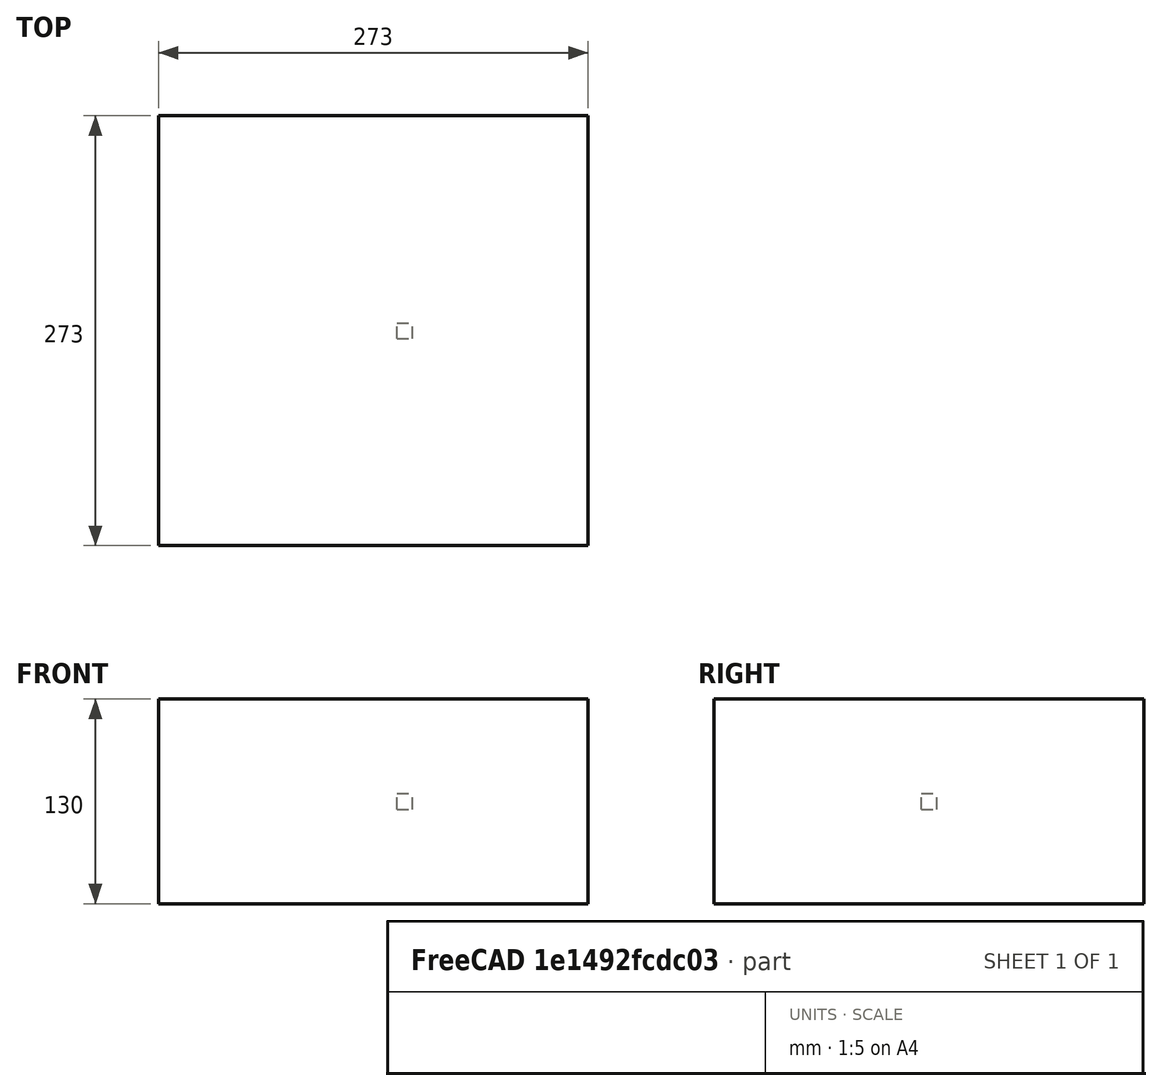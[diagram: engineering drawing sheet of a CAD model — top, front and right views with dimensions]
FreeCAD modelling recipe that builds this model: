
FCSTD DOCUMENT  (FreeCAD 0.20RUnknown)
Label: polarArray-4
License: All rights reserved
LicenseURL: http://en.wikipedia.org/wiki/All_rights_reserved
objects: App::DocumentObjectGroupPython×1251, Part::FeaturePython×3, App::Part×3
note: 2 computed .brp shape members not serialized (recipe doc carries the construction recipe); baked Part::Feature solids carry a one-line shape summary decoded from their .brp

FEATURE [App::DocumentObjectGroupPython] HALFPI  # scripted group (container) (typed FeaturePython)
  name = HALFPI
  value = pi/2.
FEATURE [App::DocumentObjectGroupPython] PI  # scripted group (container) (typed FeaturePython)
  name = PI
  value = 1.*pi
FEATURE [App::DocumentObjectGroupPython] TWOPI  # scripted group (container) (typed FeaturePython)
  name = TWOPI
  value = 2.*pi
FEATURE [App::DocumentObjectGroupPython] Constants  # scripted group (container) (typed FeaturePython)
  Group = -> [HALFPI,PI,TWOPI]
FEATURE [App::DocumentObjectGroupPython] Variables  # scripted group (container) (typed FeaturePython)
FEATURE [App::DocumentObjectGroupPython] Quantities  # scripted group (container) (typed FeaturePython)
FEATURE [App::DocumentObjectGroupPython] Isotopes  # scripted group (container) (typed FeaturePython)
FEATURE [App::DocumentObjectGroupPython] Elements  # scripted group (container) (typed FeaturePython)
FEATURE [App::DocumentObjectGroupPython] Matrix  # scripted group (container) (typed FeaturePython)
FEATURE [App::DocumentObjectGroupPython] Surfaces  # scripted group (container) (typed FeaturePython)
FEATURE [App::DocumentObjectGroupPython] Opticals  # scripted group (container) (typed FeaturePython)
  Group = -> [Matrix,Surfaces]
FEATURE [App::DocumentObjectGroupPython] G4Isotopes  # scripted group (container) (typed FeaturePython)
FEATURE [App::DocumentObjectGroupPython] H_element  # scripted group (container) (typed FeaturePython)
  Z = 1
  atom_value = 1.008
  formula = H
  name = H_element
FEATURE [App::DocumentObjectGroupPython] He_element  # scripted group (container) (typed FeaturePython)
  Z = 2
  atom_value = 4.0026
  formula = He
  name = He_element
FEATURE [App::DocumentObjectGroupPython] Li_element  # scripted group (container) (typed FeaturePython)
  Z = 3
  atom_value = 6.94
  formula = Li
  name = Li_element
FEATURE [App::DocumentObjectGroupPython] Be_element  # scripted group (container) (typed FeaturePython)
  Z = 4
  atom_value = 9.01218
  formula = Be
  name = Be_element
FEATURE [App::DocumentObjectGroupPython] B_element  # scripted group (container) (typed FeaturePython)
  Z = 5
  atom_value = 10.81
  formula = B
  name = B_element
FEATURE [App::DocumentObjectGroupPython] C_element  # scripted group (container) (typed FeaturePython)
  Z = 6
  atom_value = 12.011
  formula = C
  name = C_element
FEATURE [App::DocumentObjectGroupPython] N_element  # scripted group (container) (typed FeaturePython)
  Z = 7
  atom_value = 14.007
  formula = N
  name = N_element
FEATURE [App::DocumentObjectGroupPython] O_element  # scripted group (container) (typed FeaturePython)
  Z = 8
  atom_value = 15.999
  formula = O
  name = O_element
FEATURE [App::DocumentObjectGroupPython] F_element  # scripted group (container) (typed FeaturePython)
  Z = 9
  atom_value = 18.9984
  formula = F
  name = F_element
FEATURE [App::DocumentObjectGroupPython] Ne_element  # scripted group (container) (typed FeaturePython)
  Z = 10
  atom_value = 20.1797
  formula = Ne
  name = Ne_element
FEATURE [App::DocumentObjectGroupPython] Na_element  # scripted group (container) (typed FeaturePython)
  Z = 11
  atom_value = 22.9898
  formula = Na
  name = Na_element
FEATURE [App::DocumentObjectGroupPython] Mg_element  # scripted group (container) (typed FeaturePython)
  Z = 12
  atom_value = 24.305
  formula = Mg
  name = Mg_element
FEATURE [App::DocumentObjectGroupPython] Al_element  # scripted group (container) (typed FeaturePython)
  Z = 13
  atom_value = 26.9815
  formula = Al
  name = Al_element
FEATURE [App::DocumentObjectGroupPython] Si_element  # scripted group (container) (typed FeaturePython)
  Z = 14
  atom_value = 28.085
  formula = Si
  name = Si_element
FEATURE [App::DocumentObjectGroupPython] P_element  # scripted group (container) (typed FeaturePython)
  Z = 15
  atom_value = 30.9738
  formula = P
  name = P_element
FEATURE [App::DocumentObjectGroupPython] S_element  # scripted group (container) (typed FeaturePython)
  Z = 16
  atom_value = 32.06
  formula = S
  name = S_element
FEATURE [App::DocumentObjectGroupPython] Cl_element  # scripted group (container) (typed FeaturePython)
  Z = 17
  atom_value = 35.45
  formula = Cl
  name = Cl_element
FEATURE [App::DocumentObjectGroupPython] Ar_element  # scripted group (container) (typed FeaturePython)
  Z = 18
  atom_value = 39.95
  formula = Ar
  name = Ar_element
FEATURE [App::DocumentObjectGroupPython] K_element  # scripted group (container) (typed FeaturePython)
  Z = 19
  atom_value = 39.0983
  formula = K
  name = K_element
FEATURE [App::DocumentObjectGroupPython] Ca_element  # scripted group (container) (typed FeaturePython)
  Z = 20
  atom_value = 40.078
  formula = Ca
  name = Ca_element
FEATURE [App::DocumentObjectGroupPython] Sc_element  # scripted group (container) (typed FeaturePython)
  Z = 21
  atom_value = 44.9559
  formula = Sc
  name = Sc_element
FEATURE [App::DocumentObjectGroupPython] Ti_element  # scripted group (container) (typed FeaturePython)
  Z = 22
  atom_value = 47.867
  formula = Ti
  name = Ti_element
FEATURE [App::DocumentObjectGroupPython] V_element  # scripted group (container) (typed FeaturePython)
  Z = 23
  atom_value = 50.9415
  formula = V
  name = V_element
FEATURE [App::DocumentObjectGroupPython] Cr_element  # scripted group (container) (typed FeaturePython)
  Z = 24
  atom_value = 51.9961
  formula = Cr
  name = Cr_element
FEATURE [App::DocumentObjectGroupPython] Mn_element  # scripted group (container) (typed FeaturePython)
  Z = 25
  atom_value = 54.938
  formula = Mn
  name = Mn_element
FEATURE [App::DocumentObjectGroupPython] Fe_element  # scripted group (container) (typed FeaturePython)
  Z = 26
  atom_value = 55.845
  formula = Fe
  name = Fe_element
FEATURE [App::DocumentObjectGroupPython] Co_element  # scripted group (container) (typed FeaturePython)
  Z = 27
  atom_value = 58.9332
  formula = Co
  name = Co_element
FEATURE [App::DocumentObjectGroupPython] Ni_element  # scripted group (container) (typed FeaturePython)
  Z = 28
  atom_value = 58.6934
  formula = Ni
  name = Ni_element
FEATURE [App::DocumentObjectGroupPython] Cu_element  # scripted group (container) (typed FeaturePython)
  Z = 29
  atom_value = 63.546
  formula = Cu
  name = Cu_element
FEATURE [App::DocumentObjectGroupPython] Zn_element  # scripted group (container) (typed FeaturePython)
  Z = 30
  atom_value = 65.38
  formula = Zn
  name = Zn_element
FEATURE [App::DocumentObjectGroupPython] Ga_element  # scripted group (container) (typed FeaturePython)
  Z = 31
  atom_value = 69.723
  formula = Ga
  name = Ga_element
FEATURE [App::DocumentObjectGroupPython] Ge_element  # scripted group (container) (typed FeaturePython)
  Z = 32
  atom_value = 72.63
  formula = Ge
  name = Ge_element
FEATURE [App::DocumentObjectGroupPython] As_element  # scripted group (container) (typed FeaturePython)
  Z = 33
  atom_value = 74.9216
  formula = As
  name = As_element
FEATURE [App::DocumentObjectGroupPython] Se_element  # scripted group (container) (typed FeaturePython)
  Z = 34
  atom_value = 78.971
  formula = Se
  name = Se_element
FEATURE [App::DocumentObjectGroupPython] Br_element  # scripted group (container) (typed FeaturePython)
  Z = 35
  atom_value = 79.904
  formula = Br
  name = Br_element
FEATURE [App::DocumentObjectGroupPython] Kr_element  # scripted group (container) (typed FeaturePython)
  Z = 36
  atom_value = 83.798
  formula = Kr
  name = Kr_element
FEATURE [App::DocumentObjectGroupPython] Rb_element  # scripted group (container) (typed FeaturePython)
  Z = 37
  atom_value = 85.4678
  formula = Rb
  name = Rb_element
FEATURE [App::DocumentObjectGroupPython] Sr_element  # scripted group (container) (typed FeaturePython)
  Z = 38
  atom_value = 87.62
  formula = Sr
  name = Sr_element
FEATURE [App::DocumentObjectGroupPython] Y_element  # scripted group (container) (typed FeaturePython)
  Z = 39
  atom_value = 88.9058
  formula = Y
  name = Y_element
FEATURE [App::DocumentObjectGroupPython] Zr_element  # scripted group (container) (typed FeaturePython)
  Z = 40
  atom_value = 91.224
  formula = Zr
  name = Zr_element
FEATURE [App::DocumentObjectGroupPython] Nb_element  # scripted group (container) (typed FeaturePython)
  Z = 41
  atom_value = 92.9064
  formula = Nb
  name = Nb_element
FEATURE [App::DocumentObjectGroupPython] Mo_element  # scripted group (container) (typed FeaturePython)
  Z = 42
  atom_value = 95.95
  formula = Mo
  name = Mo_element
FEATURE [App::DocumentObjectGroupPython] Tc_element  # scripted group (container) (typed FeaturePython)
  Z = 43
  atom_value = 97
  formula = Tc
  name = Tc_element
FEATURE [App::DocumentObjectGroupPython] Ru_element  # scripted group (container) (typed FeaturePython)
  Z = 44
  atom_value = 101.07
  formula = Ru
  name = Ru_element
FEATURE [App::DocumentObjectGroupPython] Rh_element  # scripted group (container) (typed FeaturePython)
  Z = 45
  atom_value = 102.905
  formula = Rh
  name = Rh_element
FEATURE [App::DocumentObjectGroupPython] Pd_element  # scripted group (container) (typed FeaturePython)
  Z = 46
  atom_value = 106.42
  formula = Pd
  name = Pd_element
FEATURE [App::DocumentObjectGroupPython] Ag_element  # scripted group (container) (typed FeaturePython)
  Z = 47
  atom_value = 107.868
  formula = Ag
  name = Ag_element
FEATURE [App::DocumentObjectGroupPython] Cd_element  # scripted group (container) (typed FeaturePython)
  Z = 48
  atom_value = 112.414
  formula = Cd
  name = Cd_element
FEATURE [App::DocumentObjectGroupPython] In_element  # scripted group (container) (typed FeaturePython)
  Z = 49
  atom_value = 114.818
  formula = In
  name = In_element
FEATURE [App::DocumentObjectGroupPython] Sn_element  # scripted group (container) (typed FeaturePython)
  Z = 50
  atom_value = 118.71
  formula = Sn
  name = Sn_element
FEATURE [App::DocumentObjectGroupPython] Sb_element  # scripted group (container) (typed FeaturePython)
  Z = 51
  atom_value = 121.76
  formula = Sb
  name = Sb_element
FEATURE [App::DocumentObjectGroupPython] Te_element  # scripted group (container) (typed FeaturePython)
  Z = 52
  atom_value = 127.6
  formula = Te
  name = Te_element
FEATURE [App::DocumentObjectGroupPython] I_element  # scripted group (container) (typed FeaturePython)
  Z = 53
  atom_value = 126.904
  formula = I
  name = I_element
FEATURE [App::DocumentObjectGroupPython] Xe_element  # scripted group (container) (typed FeaturePython)
  Z = 54
  atom_value = 131.293
  formula = Xe
  name = Xe_element
FEATURE [App::DocumentObjectGroupPython] Cs_element  # scripted group (container) (typed FeaturePython)
  Z = 55
  atom_value = 132.905
  formula = Cs
  name = Cs_element
FEATURE [App::DocumentObjectGroupPython] Ba_element  # scripted group (container) (typed FeaturePython)
  Z = 56
  atom_value = 137.327
  formula = Ba
  name = Ba_element
FEATURE [App::DocumentObjectGroupPython] La_element  # scripted group (container) (typed FeaturePython)
  Z = 57
  atom_value = 138.905
  formula = La
  name = La_element
FEATURE [App::DocumentObjectGroupPython] Ce_element  # scripted group (container) (typed FeaturePython)
  Z = 58
  atom_value = 140.116
  formula = Ce
  name = Ce_element
FEATURE [App::DocumentObjectGroupPython] Pr_element  # scripted group (container) (typed FeaturePython)
  Z = 59
  atom_value = 140.908
  formula = Pr
  name = Pr_element
FEATURE [App::DocumentObjectGroupPython] Nd_element  # scripted group (container) (typed FeaturePython)
  Z = 60
  atom_value = 144.242
  formula = Nd
  name = Nd_element
FEATURE [App::DocumentObjectGroupPython] Pm_element  # scripted group (container) (typed FeaturePython)
  Z = 61
  atom_value = 145
  formula = Pm
  name = Pm_element
FEATURE [App::DocumentObjectGroupPython] Sm_element  # scripted group (container) (typed FeaturePython)
  Z = 62
  atom_value = 150.36
  formula = Sm
  name = Sm_element
FEATURE [App::DocumentObjectGroupPython] Eu_element  # scripted group (container) (typed FeaturePython)
  Z = 63
  atom_value = 151.964
  formula = Eu
  name = Eu_element
FEATURE [App::DocumentObjectGroupPython] Gd_element  # scripted group (container) (typed FeaturePython)
  Z = 64
  atom_value = 157.25
  formula = Gd
  name = Gd_element
FEATURE [App::DocumentObjectGroupPython] Tb_element  # scripted group (container) (typed FeaturePython)
  Z = 65
  atom_value = 158.925
  formula = Tb
  name = Tb_element
FEATURE [App::DocumentObjectGroupPython] Dy_element  # scripted group (container) (typed FeaturePython)
  Z = 66
  atom_value = 162.5
  formula = Dy
  name = Dy_element
FEATURE [App::DocumentObjectGroupPython] Ho_element  # scripted group (container) (typed FeaturePython)
  Z = 67
  atom_value = 164.93
  formula = Ho
  name = Ho_element
FEATURE [App::DocumentObjectGroupPython] Er_element  # scripted group (container) (typed FeaturePython)
  Z = 68
  atom_value = 167.259
  formula = Er
  name = Er_element
FEATURE [App::DocumentObjectGroupPython] Tm_element  # scripted group (container) (typed FeaturePython)
  Z = 69
  atom_value = 168.934
  formula = Tm
  name = Tm_element
FEATURE [App::DocumentObjectGroupPython] Yb_element  # scripted group (container) (typed FeaturePython)
  Z = 70
  atom_value = 173.045
  formula = Yb
  name = Yb_element
FEATURE [App::DocumentObjectGroupPython] Lu_element  # scripted group (container) (typed FeaturePython)
  Z = 71
  atom_value = 174.967
  formula = Lu
  name = Lu_element
FEATURE [App::DocumentObjectGroupPython] Hf_element  # scripted group (container) (typed FeaturePython)
  Z = 72
  atom_value = 178.49
  formula = Hf
  name = Hf_element
FEATURE [App::DocumentObjectGroupPython] Ta_element  # scripted group (container) (typed FeaturePython)
  Z = 73
  atom_value = 180.948
  formula = Ta
  name = Ta_element
FEATURE [App::DocumentObjectGroupPython] W_element  # scripted group (container) (typed FeaturePython)
  Z = 74
  atom_value = 183.84
  formula = W
  name = W_element
FEATURE [App::DocumentObjectGroupPython] Re_element  # scripted group (container) (typed FeaturePython)
  Z = 75
  atom_value = 186.207
  formula = Re
  name = Re_element
FEATURE [App::DocumentObjectGroupPython] Os_element  # scripted group (container) (typed FeaturePython)
  Z = 76
  atom_value = 190.23
  formula = Os
  name = Os_element
FEATURE [App::DocumentObjectGroupPython] Ir_element  # scripted group (container) (typed FeaturePython)
  Z = 77
  atom_value = 192.217
  formula = Ir
  name = Ir_element
FEATURE [App::DocumentObjectGroupPython] Pt_element  # scripted group (container) (typed FeaturePython)
  Z = 78
  atom_value = 195.084
  formula = Pt
  name = Pt_element
FEATURE [App::DocumentObjectGroupPython] Au_element  # scripted group (container) (typed FeaturePython)
  Z = 79
  atom_value = 196.967
  formula = Au
  name = Au_element
FEATURE [App::DocumentObjectGroupPython] Hg_element  # scripted group (container) (typed FeaturePython)
  Z = 80
  atom_value = 200.592
  formula = Hg
  name = Hg_element
FEATURE [App::DocumentObjectGroupPython] Tl_element  # scripted group (container) (typed FeaturePython)
  Z = 81
  atom_value = 204.38
  formula = Tl
  name = Tl_element
FEATURE [App::DocumentObjectGroupPython] Pb_element  # scripted group (container) (typed FeaturePython)
  Z = 82
  atom_value = 207.2
  formula = Pb
  name = Pb_element
FEATURE [App::DocumentObjectGroupPython] Bi_element  # scripted group (container) (typed FeaturePython)
  Z = 83
  atom_value = 208.98
  formula = Bi
  name = Bi_element
FEATURE [App::DocumentObjectGroupPython] Po_element  # scripted group (container) (typed FeaturePython)
  Z = 84
  atom_value = 209
  formula = Po
  name = Po_element
FEATURE [App::DocumentObjectGroupPython] At_element  # scripted group (container) (typed FeaturePython)
  Z = 85
  atom_value = 210
  formula = At
  name = At_element
FEATURE [App::DocumentObjectGroupPython] Rn_element  # scripted group (container) (typed FeaturePython)
  Z = 86
  atom_value = 222
  formula = Rn
  name = Rn_element
FEATURE [App::DocumentObjectGroupPython] Fr_element  # scripted group (container) (typed FeaturePython)
  Z = 87
  atom_value = 223
  formula = Fr
  name = Fr_element
FEATURE [App::DocumentObjectGroupPython] Ra_element  # scripted group (container) (typed FeaturePython)
  Z = 88
  atom_value = 226
  formula = Ra
  name = Ra_element
FEATURE [App::DocumentObjectGroupPython] Ac_element  # scripted group (container) (typed FeaturePython)
  Z = 89
  atom_value = 227
  formula = Ac
  name = Ac_element
FEATURE [App::DocumentObjectGroupPython] Th_element  # scripted group (container) (typed FeaturePython)
  Z = 90
  atom_value = 232.038
  formula = Th
  name = Th_element
FEATURE [App::DocumentObjectGroupPython] Pa_element  # scripted group (container) (typed FeaturePython)
  Z = 91
  atom_value = 231.036
  formula = Pa
  name = Pa_element
FEATURE [App::DocumentObjectGroupPython] U_element  # scripted group (container) (typed FeaturePython)
  Z = 92
  atom_value = 238.029
  formula = U
  name = U_element
FEATURE [App::DocumentObjectGroupPython] Np_element  # scripted group (container) (typed FeaturePython)
  Z = 93
  atom_value = 237
  formula = Np
  name = Np_element
FEATURE [App::DocumentObjectGroupPython] Pu_element  # scripted group (container) (typed FeaturePython)
  Z = 94
  atom_value = 244
  formula = Pu
  name = Pu_element
FEATURE [App::DocumentObjectGroupPython] Am_element  # scripted group (container) (typed FeaturePython)
  Z = 95
  atom_value = 243
  formula = Am
  name = Am_element
FEATURE [App::DocumentObjectGroupPython] Cm_element  # scripted group (container) (typed FeaturePython)
  Z = 96
  atom_value = 247
  formula = Cm
  name = Cm_element
FEATURE [App::DocumentObjectGroupPython] Bk_element  # scripted group (container) (typed FeaturePython)
  Z = 97
  atom_value = 247
  formula = Bk
  name = Bk_element
FEATURE [App::DocumentObjectGroupPython] Cf_element  # scripted group (container) (typed FeaturePython)
  Z = 98
  atom_value = 251
  formula = Cf
  name = Cf_element
FEATURE [App::DocumentObjectGroupPython] G4Elements  # scripted group (container) (typed FeaturePython)
  Group = -> [H_element,He_element,Li_element,Be_element,B_element,C_element,N_element,O_element,F_element,Ne_element,Na_element,Mg_element,Al_element,Si_element,P_element,S_element,Cl_element,Ar_element,K_element,Ca_element,Sc_element,Ti_element,V_element,Cr_element,Mn_element,Fe_element,Co_element,Ni_element,Cu_element,Zn_element,Ga_element,Ge_element,As_element,Se_element,Br_element,Kr_element,Rb_element,+61 more]
FEATURE [App::DocumentObjectGroupPython] H_element001  label="H_element : 0.101"  # scripted group (container) (typed FeaturePython)
  n = 0.101327
FEATURE [App::DocumentObjectGroupPython] C_element001  label="C_element : 0.775"  # scripted group (container) (typed FeaturePython)
  n = 0.7755
FEATURE [App::DocumentObjectGroupPython] N_element001  label="N_element : 0.035"  # scripted group (container) (typed FeaturePython)
  n = 0.035057
FEATURE [App::DocumentObjectGroupPython] O_element001  label="O_element : 0.052"  # scripted group (container) (typed FeaturePython)
  n = 0.0523159
FEATURE [App::DocumentObjectGroupPython] F_element001  label="F_element : 0.017"  # scripted group (container) (typed FeaturePython)
  n = 0.017422
FEATURE [App::DocumentObjectGroupPython] Ca_element001  label="Ca_element : 0.018"  # scripted group (container) (typed FeaturePython)
  n = 0.018378
FEATURE [App::DocumentObjectGroupPython] G4_A_150_TISSUE  label="G4_A-150_TISSUE"  # scripted group (container) (typed FeaturePython)
  Dunit = g/cm3
  Dvalue = 1.127
  Group = -> [H_element001,C_element001,N_element001,O_element001,F_element001,Ca_element001]
  conduct = 2
  density = 1
  expand = 3
  formula = G4_A-150_TISSUE
  name = G4_A-150_TISSUE
  specific = 4
FEATURE [App::DocumentObjectGroupPython] C_element002  label="C_element : 3"  # scripted group (container) (typed FeaturePython)
  n = 3
  ref = C_element
FEATURE [App::DocumentObjectGroupPython] H_element002  label="H_element : 6"  # scripted group (container) (typed FeaturePython)
  n = 6
  ref = H_element
FEATURE [App::DocumentObjectGroupPython] O_element002  label="O_element : 1"  # scripted group (container) (typed FeaturePython)
  n = 1
  ref = O_element
FEATURE [App::DocumentObjectGroupPython] G4_ACETONE  # scripted group (container) (typed FeaturePython)
  Dunit = g/cm3
  Dvalue = 0.7899
  Group = -> [C_element002,H_element002,O_element002]
  conduct = 2
  density = 1
  expand = 3
  formula = G4_ACETONE
  name = G4_ACETONE
  specific = 4
FEATURE [App::DocumentObjectGroupPython] C_element003  label="C_element : 2"  # scripted group (container) (typed FeaturePython)
  n = 2
  ref = C_element
FEATURE [App::DocumentObjectGroupPython] H_element003  label="H_element : 2"  # scripted group (container) (typed FeaturePython)
  n = 2
  ref = H_element
FEATURE [App::DocumentObjectGroupPython] G4_ACETYLENE  # scripted group (container) (typed FeaturePython)
  Dunit = g/cm3
  Dvalue = 0.0010967
  Group = -> [C_element003,H_element003]
  conduct = 2
  density = 1
  expand = 3
  formula = G4_ACETYLENE
  name = G4_ACETYLENE
  specific = 4
FEATURE [App::DocumentObjectGroupPython] C_element004  label="C_element : 5"  # scripted group (container) (typed FeaturePython)
  n = 5
  ref = C_element
FEATURE [App::DocumentObjectGroupPython] H_element004  label="H_element : 5"  # scripted group (container) (typed FeaturePython)
  n = 5
  ref = H_element
FEATURE [App::DocumentObjectGroupPython] N_element002  label="N_element : 5"  # scripted group (container) (typed FeaturePython)
  n = 5
  ref = N_element
FEATURE [App::DocumentObjectGroupPython] G4_ADENINE  # scripted group (container) (typed FeaturePython)
  Dunit = g/cm3
  Dvalue = 1.6
  Group = -> [C_element004,H_element004,N_element002]
  conduct = 2
  density = 1
  expand = 3
  formula = G4_ADENINE
  name = G4_ADENINE
  specific = 4
FEATURE [App::DocumentObjectGroupPython] H_element005  label="H_element : 0.114"  # scripted group (container) (typed FeaturePython)
  n = 0.114
FEATURE [App::DocumentObjectGroupPython] C_element005  label="C_element : 0.598"  # scripted group (container) (typed FeaturePython)
  n = 0.598
FEATURE [App::DocumentObjectGroupPython] N_element003  label="N_element : 0.007"  # scripted group (container) (typed FeaturePython)
  n = 0.007
FEATURE [App::DocumentObjectGroupPython] O_element003  label="O_element : 0.278"  # scripted group (container) (typed FeaturePython)
  n = 0.278
FEATURE [App::DocumentObjectGroupPython] Na_element001  label="Na_element : 0.001"  # scripted group (container) (typed FeaturePython)
  n = 0.001
FEATURE [App::DocumentObjectGroupPython] S_element001  label="S_element : 0.001"  # scripted group (container) (typed FeaturePython)
  n = 0.001
FEATURE [App::DocumentObjectGroupPython] Cl_element001  label="Cl_element : 0.001"  # scripted group (container) (typed FeaturePython)
  n = 0.001
FEATURE [App::DocumentObjectGroupPython] G4_ADIPOSE_TISSUE_ICRP  # scripted group (container) (typed FeaturePython)
  Dunit = g/cm3
  Dvalue = 0.95
  Group = -> [H_element005,C_element005,N_element003,O_element003,Na_element001,S_element001,Cl_element001]
  conduct = 2
  density = 1
  expand = 3
  formula = G4_ADIPOSE_TISSUE_ICRP
  name = G4_ADIPOSE_TISSUE_ICRP
  specific = 4
FEATURE [App::DocumentObjectGroupPython] C_element006  label="C_element : 0.000"  # scripted group (container) (typed FeaturePython)
  n = 0.000124
FEATURE [App::DocumentObjectGroupPython] N_element004  label="N_element : 0.755"  # scripted group (container) (typed FeaturePython)
  n = 0.755268
FEATURE [App::DocumentObjectGroupPython] O_element004  label="O_element : 0.232"  # scripted group (container) (typed FeaturePython)
  n = 0.231781
FEATURE [App::DocumentObjectGroupPython] Ar_element001  label="Ar_element : 0.013"  # scripted group (container) (typed FeaturePython)
  n = 0.012827
FEATURE [App::DocumentObjectGroupPython] G4_AIR  # scripted group (container) (typed FeaturePython)
  Dunit = g/cm3
  Dvalue = 0.00120479
  Group = -> [C_element006,N_element004,O_element004,Ar_element001]
  conduct = 2
  density = 1
  expand = 3
  formula = G4_AIR
  name = G4_AIR
  specific = 4
FEATURE [App::DocumentObjectGroupPython] C_element007  label="C_element : 006"  # scripted group (container) (typed FeaturePython)
  n = 3
  ref = C_element
FEATURE [App::DocumentObjectGroupPython] H_element006  label="H_element : 7"  # scripted group (container) (typed FeaturePython)
  n = 7
  ref = H_element
FEATURE [App::DocumentObjectGroupPython] N_element005  label="N_element : 1"  # scripted group (container) (typed FeaturePython)
  n = 1
  ref = N_element
FEATURE [App::DocumentObjectGroupPython] O_element005  label="O_element : 2"  # scripted group (container) (typed FeaturePython)
  n = 2
  ref = O_element
FEATURE [App::DocumentObjectGroupPython] G4_ALANINE  # scripted group (container) (typed FeaturePython)
  Dunit = g/cm3
  Dvalue = 1.42
  Group = -> [C_element007,H_element006,N_element005,O_element005]
  conduct = 2
  density = 1
  expand = 3
  formula = G4_ALANINE
  name = G4_ALANINE
  specific = 4
FEATURE [App::DocumentObjectGroupPython] Al_element001  label="Al_element : 2"  # scripted group (container) (typed FeaturePython)
  n = 2
  ref = Al_element
FEATURE [App::DocumentObjectGroupPython] O_element006  label="O_element : 3"  # scripted group (container) (typed FeaturePython)
  n = 3
  ref = O_element
FEATURE [App::DocumentObjectGroupPython] G4_ALUMINUM_OXIDE  # scripted group (container) (typed FeaturePython)
  Dunit = g/cm3
  Dvalue = 3.97
  Group = -> [Al_element001,O_element006]
  conduct = 2
  density = 1
  expand = 3
  formula = G4_ALUMINUM_OXIDE
  name = G4_ALUMINUM_OXIDE
  specific = 4
FEATURE [App::DocumentObjectGroupPython] H_element007  label="H_element : 0.106"  # scripted group (container) (typed FeaturePython)
  n = 0.10593
FEATURE [App::DocumentObjectGroupPython] C_element008  label="C_element : 0.789"  # scripted group (container) (typed FeaturePython)
  n = 0.788974
FEATURE [App::DocumentObjectGroupPython] O_element007  label="O_element : 0.105"  # scripted group (container) (typed FeaturePython)
  n = 0.105096
FEATURE [App::DocumentObjectGroupPython] G4_AMBER  # scripted group (container) (typed FeaturePython)
  Dunit = g/cm3
  Dvalue = 1.1
  Group = -> [H_element007,C_element008,O_element007]
  conduct = 2
  density = 1
  expand = 3
  formula = G4_AMBER
  name = G4_AMBER
  specific = 4
FEATURE [App::DocumentObjectGroupPython] N_element006  label="N_element : 006"  # scripted group (container) (typed FeaturePython)
  n = 1
  ref = N_element
FEATURE [App::DocumentObjectGroupPython] H_element008  label="H_element : 3"  # scripted group (container) (typed FeaturePython)
  n = 3
  ref = H_element
FEATURE [App::DocumentObjectGroupPython] G4_AMMONIA  # scripted group (container) (typed FeaturePython)
  Dunit = g/cm3
  Dvalue = 0.000826019
  Group = -> [N_element006,H_element008]
  conduct = 2
  density = 1
  expand = 3
  formula = G4_AMMONIA
  name = G4_AMMONIA
  specific = 4
FEATURE [App::DocumentObjectGroupPython] C_element009  label="C_element : 6"  # scripted group (container) (typed FeaturePython)
  n = 6
  ref = C_element
FEATURE [App::DocumentObjectGroupPython] H_element009  label="H_element : 008"  # scripted group (container) (typed FeaturePython)
  n = 7
  ref = H_element
FEATURE [App::DocumentObjectGroupPython] N_element007  label="N_element : 007"  # scripted group (container) (typed FeaturePython)
  n = 1
  ref = N_element
FEATURE [App::DocumentObjectGroupPython] G4_ANILINE  # scripted group (container) (typed FeaturePython)
  Dunit = g/cm3
  Dvalue = 1.0235
  Group = -> [C_element009,H_element009,N_element007]
  conduct = 2
  density = 1
  expand = 3
  formula = G4_ANILINE
  name = G4_ANILINE
  specific = 4
FEATURE [App::DocumentObjectGroupPython] C_element010  label="C_element : 14"  # scripted group (container) (typed FeaturePython)
  n = 14
  ref = C_element
FEATURE [App::DocumentObjectGroupPython] H_element010  label="H_element : 10"  # scripted group (container) (typed FeaturePython)
  n = 10
  ref = H_element
FEATURE [App::DocumentObjectGroupPython] G4_ANTHRACENE  # scripted group (container) (typed FeaturePython)
  Dunit = g/cm3
  Dvalue = 1.283
  Group = -> [C_element010,H_element010]
  conduct = 2
  density = 1
  expand = 3
  formula = G4_ANTHRACENE
  name = G4_ANTHRACENE
  specific = 4
FEATURE [App::DocumentObjectGroupPython] H_element011  label="H_element : 0.065"  # scripted group (container) (typed FeaturePython)
  n = 0.0654709
FEATURE [App::DocumentObjectGroupPython] C_element011  label="C_element : 0.537"  # scripted group (container) (typed FeaturePython)
  n = 0.536944
FEATURE [App::DocumentObjectGroupPython] N_element008  label="N_element : 0.021"  # scripted group (container) (typed FeaturePython)
  n = 0.0215
FEATURE [App::DocumentObjectGroupPython] O_element008  label="O_element : 0.032"  # scripted group (container) (typed FeaturePython)
  n = 0.032085
FEATURE [App::DocumentObjectGroupPython] F_element002  label="F_element : 0.167"  # scripted group (container) (typed FeaturePython)
  n = 0.167411
FEATURE [App::DocumentObjectGroupPython] Ca_element002  label="Ca_element : 0.177"  # scripted group (container) (typed FeaturePython)
  n = 0.176589
FEATURE [App::DocumentObjectGroupPython] G4_B_100_BONE  label="G4_B-100_BONE"  # scripted group (container) (typed FeaturePython)
  Dunit = g/cm3
  Dvalue = 1.45
  Group = -> [H_element011,C_element011,N_element008,O_element008,F_element002,Ca_element002]
  conduct = 2
  density = 1
  expand = 3
  formula = G4_B-100_BONE
  name = G4_B-100_BONE
  specific = 4
FEATURE [App::DocumentObjectGroupPython] H_element012  label="H_element : 0.057"  # scripted group (container) (typed FeaturePython)
  n = 0.057441
FEATURE [App::DocumentObjectGroupPython] C_element012  label="C_element : 0.790"  # scripted group (container) (typed FeaturePython)
  n = 0.774591
FEATURE [App::DocumentObjectGroupPython] O_element009  label="O_element : 0.168"  # scripted group (container) (typed FeaturePython)
  n = 0.167968
FEATURE [App::DocumentObjectGroupPython] G4_BAKELITE  # scripted group (container) (typed FeaturePython)
  Dunit = g/cm3
  Dvalue = 1.25
  Group = -> [H_element012,C_element012,O_element009]
  conduct = 2
  density = 1
  expand = 3
  formula = G4_BAKELITE
  name = G4_BAKELITE
  specific = 4
FEATURE [App::DocumentObjectGroupPython] Ba_element001  label="Ba_element : 1"  # scripted group (container) (typed FeaturePython)
  n = 1
  ref = Ba_element
FEATURE [App::DocumentObjectGroupPython] F_element003  label="F_element : 2"  # scripted group (container) (typed FeaturePython)
  n = 2
  ref = F_element
FEATURE [App::DocumentObjectGroupPython] G4_BARIUM_FLUORIDE  # scripted group (container) (typed FeaturePython)
  Dunit = g/cm3
  Dvalue = 4.89
  Group = -> [Ba_element001,F_element003]
  conduct = 2
  density = 1
  expand = 3
  formula = G4_BARIUM_FLUORIDE
  name = G4_BARIUM_FLUORIDE
  specific = 4
FEATURE [App::DocumentObjectGroupPython] Ba_element002  label="Ba_element : 002"  # scripted group (container) (typed FeaturePython)
  n = 1
  ref = Ba_element
FEATURE [App::DocumentObjectGroupPython] S_element002  label="S_element : 1"  # scripted group (container) (typed FeaturePython)
  n = 1
  ref = S_element
FEATURE [App::DocumentObjectGroupPython] O_element010  label="O_element : 4"  # scripted group (container) (typed FeaturePython)
  n = 4
  ref = O_element
FEATURE [App::DocumentObjectGroupPython] G4_BARIUM_SULFATE  # scripted group (container) (typed FeaturePython)
  Dunit = g/cm3
  Dvalue = 4.5
  Group = -> [Ba_element002,S_element002,O_element010]
  conduct = 2
  density = 1
  expand = 3
  formula = G4_BARIUM_SULFATE
  name = G4_BARIUM_SULFATE
  specific = 4
FEATURE [App::DocumentObjectGroupPython] C_element013  label="C_element : 007"  # scripted group (container) (typed FeaturePython)
  n = 6
  ref = C_element
FEATURE [App::DocumentObjectGroupPython] H_element013  label="H_element : 009"  # scripted group (container) (typed FeaturePython)
  n = 6
  ref = H_element
FEATURE [App::DocumentObjectGroupPython] G4_BENZENE  # scripted group (container) (typed FeaturePython)
  Dunit = g/cm3
  Dvalue = 0.87865
  Group = -> [C_element013,H_element013]
  conduct = 2
  density = 1
  expand = 3
  formula = G4_BENZENE
  name = G4_BENZENE
  specific = 4
FEATURE [App::DocumentObjectGroupPython] Be_element001  label="Be_element : 1"  # scripted group (container) (typed FeaturePython)
  n = 1
  ref = Be_element
FEATURE [App::DocumentObjectGroupPython] O_element011  label="O_element : 005"  # scripted group (container) (typed FeaturePython)
  n = 1
  ref = O_element
FEATURE [App::DocumentObjectGroupPython] G4_BERYLLIUM_OXIDE  # scripted group (container) (typed FeaturePython)
  Dunit = g/cm3
  Dvalue = 3.01
  Group = -> [Be_element001,O_element011]
  conduct = 2
  density = 1
  expand = 3
  formula = G4_BERYLLIUM_OXIDE
  name = G4_BERYLLIUM_OXIDE
  specific = 4
FEATURE [App::DocumentObjectGroupPython] Bi_element001  label="Bi_element : 4"  # scripted group (container) (typed FeaturePython)
  n = 4
  ref = Bi_element
FEATURE [App::DocumentObjectGroupPython] Ge_element001  label="Ge_element : 3"  # scripted group (container) (typed FeaturePython)
  n = 3
  ref = Ge_element
FEATURE [App::DocumentObjectGroupPython] O_element012  label="O_element : 12"  # scripted group (container) (typed FeaturePython)
  n = 12
  ref = O_element
FEATURE [App::DocumentObjectGroupPython] G4_BGO  # scripted group (container) (typed FeaturePython)
  Dunit = g/cm3
  Dvalue = 7.13
  Group = -> [Bi_element001,Ge_element001,O_element012]
  conduct = 2
  density = 1
  expand = 3
  formula = G4_BGO
  name = G4_BGO
  specific = 4
FEATURE [App::DocumentObjectGroupPython] H_element014  label="H_element : 0.102"  # scripted group (container) (typed FeaturePython)
  n = 0.102
FEATURE [App::DocumentObjectGroupPython] C_element014  label="C_element : 0.110"  # scripted group (container) (typed FeaturePython)
  n = 0.11
FEATURE [App::DocumentObjectGroupPython] N_element009  label="N_element : 0.033"  # scripted group (container) (typed FeaturePython)
  n = 0.033
FEATURE [App::DocumentObjectGroupPython] O_element013  label="O_element : 0.745"  # scripted group (container) (typed FeaturePython)
  n = 0.745
FEATURE [App::DocumentObjectGroupPython] Na_element002  label="Na_element : 0.002"  # scripted group (container) (typed FeaturePython)
  n = 0.001
FEATURE [App::DocumentObjectGroupPython] P_element001  label="P_element : 0.001"  # scripted group (container) (typed FeaturePython)
  n = 0.001
FEATURE [App::DocumentObjectGroupPython] S_element003  label="S_element : 0.002"  # scripted group (container) (typed FeaturePython)
  n = 0.002
FEATURE [App::DocumentObjectGroupPython] Cl_element002  label="Cl_element : 0.003"  # scripted group (container) (typed FeaturePython)
  n = 0.003
FEATURE [App::DocumentObjectGroupPython] K_element001  label="K_element : 0.002"  # scripted group (container) (typed FeaturePython)
  n = 0.002
FEATURE [App::DocumentObjectGroupPython] Fe_element001  label="Fe_element : 0.001"  # scripted group (container) (typed FeaturePython)
  n = 0.001
FEATURE [App::DocumentObjectGroupPython] G4_BLOOD_ICRP  # scripted group (container) (typed FeaturePython)
  Dunit = g/cm3
  Dvalue = 1.06
  Group = -> [H_element014,C_element014,N_element009,O_element013,Na_element002,P_element001,S_element003,Cl_element002,K_element001,Fe_element001]
  conduct = 2
  density = 1
  expand = 3
  formula = G4_BLOOD_ICRP
  name = G4_BLOOD_ICRP
  specific = 4
FEATURE [App::DocumentObjectGroupPython] H_element015  label="H_element : 0.064"  # scripted group (container) (typed FeaturePython)
  n = 0.064
FEATURE [App::DocumentObjectGroupPython] C_element015  label="C_element : 0.278"  # scripted group (container) (typed FeaturePython)
  n = 0.278
FEATURE [App::DocumentObjectGroupPython] N_element010  label="N_element : 0.027"  # scripted group (container) (typed FeaturePython)
  n = 0.027
FEATURE [App::DocumentObjectGroupPython] O_element014  label="O_element : 0.410"  # scripted group (container) (typed FeaturePython)
  n = 0.41
FEATURE [App::DocumentObjectGroupPython] Mg_element001  label="Mg_element : 0.002"  # scripted group (container) (typed FeaturePython)
  n = 0.002
FEATURE [App::DocumentObjectGroupPython] P_element002  label="P_element : 0.070"  # scripted group (container) (typed FeaturePython)
  n = 0.07
FEATURE [App::DocumentObjectGroupPython] S_element004  label="S_element : 0.003"  # scripted group (container) (typed FeaturePython)
  n = 0.002
FEATURE [App::DocumentObjectGroupPython] Ca_element003  label="Ca_element : 0.147"  # scripted group (container) (typed FeaturePython)
  n = 0.147
FEATURE [App::DocumentObjectGroupPython] G4_BONE_COMPACT_ICRU  # scripted group (container) (typed FeaturePython)
  Dunit = g/cm3
  Dvalue = 1.85
  Group = -> [H_element015,C_element015,N_element010,O_element014,Mg_element001,P_element002,S_element004,Ca_element003]
  conduct = 2
  density = 1
  expand = 3
  formula = G4_BONE_COMPACT_ICRU
  name = G4_BONE_COMPACT_ICRU
  specific = 4
FEATURE [App::DocumentObjectGroupPython] H_element016  label="H_element : 0.034"  # scripted group (container) (typed FeaturePython)
  n = 0.034
FEATURE [App::DocumentObjectGroupPython] C_element016  label="C_element : 0.155"  # scripted group (container) (typed FeaturePython)
  n = 0.155
FEATURE [App::DocumentObjectGroupPython] N_element011  label="N_element : 0.042"  # scripted group (container) (typed FeaturePython)
  n = 0.042
FEATURE [App::DocumentObjectGroupPython] O_element015  label="O_element : 0.435"  # scripted group (container) (typed FeaturePython)
  n = 0.435
FEATURE [App::DocumentObjectGroupPython] Na_element003  label="Na_element : 0.003"  # scripted group (container) (typed FeaturePython)
  n = 0.001
FEATURE [App::DocumentObjectGroupPython] Mg_element002  label="Mg_element : 0.003"  # scripted group (container) (typed FeaturePython)
  n = 0.002
FEATURE [App::DocumentObjectGroupPython] P_element003  label="P_element : 0.103"  # scripted group (container) (typed FeaturePython)
  n = 0.103
FEATURE [App::DocumentObjectGroupPython] S_element005  label="S_element : 0.004"  # scripted group (container) (typed FeaturePython)
  n = 0.003
FEATURE [App::DocumentObjectGroupPython] Ca_element004  label="Ca_element : 0.225"  # scripted group (container) (typed FeaturePython)
  n = 0.225
FEATURE [App::DocumentObjectGroupPython] G4_BONE_CORTICAL_ICRP  # scripted group (container) (typed FeaturePython)
  Dunit = g/cm3
  Dvalue = 1.92
  Group = -> [H_element016,C_element016,N_element011,O_element015,Na_element003,Mg_element002,P_element003,S_element005,Ca_element004]
  conduct = 2
  density = 1
  expand = 3
  formula = G4_BONE_CORTICAL_ICRP
  name = G4_BONE_CORTICAL_ICRP
  specific = 4
FEATURE [App::DocumentObjectGroupPython] B_element001  label="B_element : 4"  # scripted group (container) (typed FeaturePython)
  n = 4
  ref = B_element
FEATURE [App::DocumentObjectGroupPython] C_element017  label="C_element : 1"  # scripted group (container) (typed FeaturePython)
  n = 1
  ref = C_element
FEATURE [App::DocumentObjectGroupPython] G4_BORON_CARBIDE  # scripted group (container) (typed FeaturePython)
  Dunit = g/cm3
  Dvalue = 2.52
  Group = -> [B_element001,C_element017]
  conduct = 2
  density = 1
  expand = 3
  formula = G4_BORON_CARBIDE
  name = G4_BORON_CARBIDE
  specific = 4
FEATURE [App::DocumentObjectGroupPython] B_element002  label="B_element : 2"  # scripted group (container) (typed FeaturePython)
  n = 2
  ref = B_element
FEATURE [App::DocumentObjectGroupPython] O_element016  label="O_element : 006"  # scripted group (container) (typed FeaturePython)
  n = 3
  ref = O_element
FEATURE [App::DocumentObjectGroupPython] G4_BORON_OXIDE  # scripted group (container) (typed FeaturePython)
  Dunit = g/cm3
  Dvalue = 1.812
  Group = -> [B_element002,O_element016]
  conduct = 2
  density = 1
  expand = 3
  formula = G4_BORON_OXIDE
  name = G4_BORON_OXIDE
  specific = 4
FEATURE [App::DocumentObjectGroupPython] H_element017  label="H_element : 0.107"  # scripted group (container) (typed FeaturePython)
  n = 0.107
FEATURE [App::DocumentObjectGroupPython] C_element018  label="C_element : 0.145"  # scripted group (container) (typed FeaturePython)
  n = 0.145
FEATURE [App::DocumentObjectGroupPython] N_element012  label="N_element : 0.022"  # scripted group (container) (typed FeaturePython)
  n = 0.022
FEATURE [App::DocumentObjectGroupPython] O_element017  label="O_element : 0.712"  # scripted group (container) (typed FeaturePython)
  n = 0.712
FEATURE [App::DocumentObjectGroupPython] Na_element004  label="Na_element : 0.004"  # scripted group (container) (typed FeaturePython)
  n = 0.002
FEATURE [App::DocumentObjectGroupPython] P_element004  label="P_element : 0.004"  # scripted group (container) (typed FeaturePython)
  n = 0.004
FEATURE [App::DocumentObjectGroupPython] S_element006  label="S_element : 0.005"  # scripted group (container) (typed FeaturePython)
  n = 0.002
FEATURE [App::DocumentObjectGroupPython] Cl_element003  label="Cl_element : 0.004"  # scripted group (container) (typed FeaturePython)
  n = 0.003
FEATURE [App::DocumentObjectGroupPython] K_element002  label="K_element : 0.003"  # scripted group (container) (typed FeaturePython)
  n = 0.003
FEATURE [App::DocumentObjectGroupPython] G4_BRAIN_ICRP  # scripted group (container) (typed FeaturePython)
  Dunit = g/cm3
  Dvalue = 1.04
  Group = -> [H_element017,C_element018,N_element012,O_element017,Na_element004,P_element004,S_element006,Cl_element003,K_element002]
  conduct = 2
  density = 1
  expand = 3
  formula = G4_BRAIN_ICRP
  name = G4_BRAIN_ICRP
  specific = 4
FEATURE [App::DocumentObjectGroupPython] C_element019  label="C_element : 4"  # scripted group (container) (typed FeaturePython)
  n = 4
  ref = C_element
FEATURE [App::DocumentObjectGroupPython] H_element018  label="H_element : 010"  # scripted group (container) (typed FeaturePython)
  n = 10
  ref = H_element
FEATURE [App::DocumentObjectGroupPython] G4_BUTANE  # scripted group (container) (typed FeaturePython)
  Dunit = g/cm3
  Dvalue = 0.00249343
  Group = -> [C_element019,H_element018]
  conduct = 2
  density = 1
  expand = 3
  formula = G4_BUTANE
  name = G4_BUTANE
  specific = 4
FEATURE [App::DocumentObjectGroupPython] C_element020  label="C_element : 008"  # scripted group (container) (typed FeaturePython)
  n = 4
  ref = C_element
FEATURE [App::DocumentObjectGroupPython] H_element019  label="H_element : 011"  # scripted group (container) (typed FeaturePython)
  n = 10
  ref = H_element
FEATURE [App::DocumentObjectGroupPython] O_element018  label="O_element : 007"  # scripted group (container) (typed FeaturePython)
  n = 1
  ref = O_element
FEATURE [App::DocumentObjectGroupPython] G4_N_BUTYL_ALCOHOL  label="G4_N-BUTYL_ALCOHOL"  # scripted group (container) (typed FeaturePython)
  Dunit = g/cm3
  Dvalue = 0.8098
  Group = -> [C_element020,H_element019,O_element018]
  conduct = 2
  density = 1
  expand = 3
  formula = G4_N-BUTYL_ALCOHOL
  name = G4_N-BUTYL_ALCOHOL
  specific = 4
FEATURE [App::DocumentObjectGroupPython] H_element020  label="H_element : 0.025"  # scripted group (container) (typed FeaturePython)
  n = 0.02468
FEATURE [App::DocumentObjectGroupPython] C_element021  label="C_element : 0.502"  # scripted group (container) (typed FeaturePython)
  n = 0.501611
FEATURE [App::DocumentObjectGroupPython] O_element019  label="O_element : 0.005"  # scripted group (container) (typed FeaturePython)
  n = 0.004527
FEATURE [App::DocumentObjectGroupPython] F_element004  label="F_element : 0.465"  # scripted group (container) (typed FeaturePython)
  n = 0.465209
FEATURE [App::DocumentObjectGroupPython] Si_element001  label="Si_element : 0.004"  # scripted group (container) (typed FeaturePython)
  n = 0.003973
FEATURE [App::DocumentObjectGroupPython] G4_C_552  label="G4_C-552"  # scripted group (container) (typed FeaturePython)
  Dunit = g/cm3
  Dvalue = 1.76
  Group = -> [H_element020,C_element021,O_element019,F_element004,Si_element001]
  conduct = 2
  density = 1
  expand = 3
  formula = G4_C-552
  name = G4_C-552
  specific = 4
FEATURE [App::DocumentObjectGroupPython] Cd_element001  label="Cd_element : 1"  # scripted group (container) (typed FeaturePython)
  n = 1
  ref = Cd_element
FEATURE [App::DocumentObjectGroupPython] Te_element001  label="Te_element : 1"  # scripted group (container) (typed FeaturePython)
  n = 1
  ref = Te_element
FEATURE [App::DocumentObjectGroupPython] G4_CADMIUM_TELLURIDE  # scripted group (container) (typed FeaturePython)
  Dunit = g/cm3
  Dvalue = 6.2
  Group = -> [Cd_element001,Te_element001]
  conduct = 2
  density = 1
  expand = 3
  formula = G4_CADMIUM_TELLURIDE
  name = G4_CADMIUM_TELLURIDE
  specific = 4
FEATURE [App::DocumentObjectGroupPython] Cd_element002  label="Cd_element : 002"  # scripted group (container) (typed FeaturePython)
  n = 1
  ref = Cd_element
FEATURE [App::DocumentObjectGroupPython] W_element001  label="W_element : 1"  # scripted group (container) (typed FeaturePython)
  n = 1
  ref = W_element
FEATURE [App::DocumentObjectGroupPython] O_element020  label="O_element : 008"  # scripted group (container) (typed FeaturePython)
  n = 4
  ref = O_element
FEATURE [App::DocumentObjectGroupPython] G4_CADMIUM_TUNGSTATE  # scripted group (container) (typed FeaturePython)
  Dunit = g/cm3
  Dvalue = 7.9
  Group = -> [Cd_element002,W_element001,O_element020]
  conduct = 2
  density = 1
  expand = 3
  formula = G4_CADMIUM_TUNGSTATE
  name = G4_CADMIUM_TUNGSTATE
  specific = 4
FEATURE [App::DocumentObjectGroupPython] Ca_element005  label="Ca_element : 1"  # scripted group (container) (typed FeaturePython)
  n = 1
  ref = Ca_element
FEATURE [App::DocumentObjectGroupPython] C_element022  label="C_element : 009"  # scripted group (container) (typed FeaturePython)
  n = 1
  ref = C_element
FEATURE [App::DocumentObjectGroupPython] O_element021  label="O_element : 009"  # scripted group (container) (typed FeaturePython)
  n = 3
  ref = O_element
FEATURE [App::DocumentObjectGroupPython] G4_CALCIUM_CARBONATE  # scripted group (container) (typed FeaturePython)
  Dunit = g/cm3
  Dvalue = 2.8
  Group = -> [Ca_element005,C_element022,O_element021]
  conduct = 2
  density = 1
  expand = 3
  formula = G4_CALCIUM_CARBONATE
  name = G4_CALCIUM_CARBONATE
  specific = 4
FEATURE [App::DocumentObjectGroupPython] Ca_element006  label="Ca_element : 002"  # scripted group (container) (typed FeaturePython)
  n = 1
  ref = Ca_element
FEATURE [App::DocumentObjectGroupPython] F_element005  label="F_element : 003"  # scripted group (container) (typed FeaturePython)
  n = 2
  ref = F_element
FEATURE [App::DocumentObjectGroupPython] G4_CALCIUM_FLUORIDE  # scripted group (container) (typed FeaturePython)
  Dunit = g/cm3
  Dvalue = 3.18
  Group = -> [Ca_element006,F_element005]
  conduct = 2
  density = 1
  expand = 3
  formula = G4_CALCIUM_FLUORIDE
  name = G4_CALCIUM_FLUORIDE
  specific = 4
FEATURE [App::DocumentObjectGroupPython] Ca_element007  label="Ca_element : 003"  # scripted group (container) (typed FeaturePython)
  n = 1
  ref = Ca_element
FEATURE [App::DocumentObjectGroupPython] O_element022  label="O_element : 010"  # scripted group (container) (typed FeaturePython)
  n = 1
  ref = O_element
FEATURE [App::DocumentObjectGroupPython] G4_CALCIUM_OXIDE  # scripted group (container) (typed FeaturePython)
  Dunit = g/cm3
  Dvalue = 3.3
  Group = -> [Ca_element007,O_element022]
  conduct = 2
  density = 1
  expand = 3
  formula = G4_CALCIUM_OXIDE
  name = G4_CALCIUM_OXIDE
  specific = 4
FEATURE [App::DocumentObjectGroupPython] Ca_element008  label="Ca_element : 004"  # scripted group (container) (typed FeaturePython)
  n = 1
  ref = Ca_element
FEATURE [App::DocumentObjectGroupPython] S_element007  label="S_element : 002"  # scripted group (container) (typed FeaturePython)
  n = 1
  ref = S_element
FEATURE [App::DocumentObjectGroupPython] O_element023  label="O_element : 011"  # scripted group (container) (typed FeaturePython)
  n = 4
  ref = O_element
FEATURE [App::DocumentObjectGroupPython] G4_CALCIUM_SULFATE  # scripted group (container) (typed FeaturePython)
  Dunit = g/cm3
  Dvalue = 2.96
  Group = -> [Ca_element008,S_element007,O_element023]
  conduct = 2
  density = 1
  expand = 3
  formula = G4_CALCIUM_SULFATE
  name = G4_CALCIUM_SULFATE
  specific = 4
FEATURE [App::DocumentObjectGroupPython] Ca_element009  label="Ca_element : 005"  # scripted group (container) (typed FeaturePython)
  n = 1
  ref = Ca_element
FEATURE [App::DocumentObjectGroupPython] W_element002  label="W_element : 002"  # scripted group (container) (typed FeaturePython)
  n = 1
  ref = W_element
FEATURE [App::DocumentObjectGroupPython] O_element024  label="O_element : 012"  # scripted group (container) (typed FeaturePython)
  n = 4
  ref = O_element
FEATURE [App::DocumentObjectGroupPython] G4_CALCIUM_TUNGSTATE  # scripted group (container) (typed FeaturePython)
  Dunit = g/cm3
  Dvalue = 6.062
  Group = -> [Ca_element009,W_element002,O_element024]
  conduct = 2
  density = 1
  expand = 3
  formula = G4_CALCIUM_TUNGSTATE
  name = G4_CALCIUM_TUNGSTATE
  specific = 4
FEATURE [App::DocumentObjectGroupPython] C_element023  label="C_element : 010"  # scripted group (container) (typed FeaturePython)
  n = 1
  ref = C_element
FEATURE [App::DocumentObjectGroupPython] O_element025  label="O_element : 013"  # scripted group (container) (typed FeaturePython)
  n = 2
  ref = O_element
FEATURE [App::DocumentObjectGroupPython] G4_CARBON_DIOXIDE  # scripted group (container) (typed FeaturePython)
  Dunit = g/cm3
  Dvalue = 0.00184212
  Group = -> [C_element023,O_element025]
  conduct = 2
  density = 1
  expand = 3
  formula = G4_CARBON_DIOXIDE
  name = G4_CARBON_DIOXIDE
  specific = 4
FEATURE [App::DocumentObjectGroupPython] C_element024  label="C_element : 011"  # scripted group (container) (typed FeaturePython)
  n = 1
  ref = C_element
FEATURE [App::DocumentObjectGroupPython] Cl_element004  label="Cl_element : 4"  # scripted group (container) (typed FeaturePython)
  n = 4
  ref = Cl_element
FEATURE [App::DocumentObjectGroupPython] G4_CARBON_TETRACHLORIDE  # scripted group (container) (typed FeaturePython)
  Dunit = g/cm3
  Dvalue = 1.594
  Group = -> [C_element024,Cl_element004]
  conduct = 2
  density = 1
  expand = 3
  formula = G4_CARBON_TETRACHLORIDE
  name = G4_CARBON_TETRACHLORIDE
  specific = 4
FEATURE [App::DocumentObjectGroupPython] C_element025  label="C_element : 012"  # scripted group (container) (typed FeaturePython)
  n = 6
  ref = C_element
FEATURE [App::DocumentObjectGroupPython] H_element021  label="H_element : 012"  # scripted group (container) (typed FeaturePython)
  n = 10
  ref = H_element
FEATURE [App::DocumentObjectGroupPython] O_element026  label="O_element : 5"  # scripted group (container) (typed FeaturePython)
  n = 5
  ref = O_element
FEATURE [App::DocumentObjectGroupPython] G4_CELLULOSE_CELLOPHANE  # scripted group (container) (typed FeaturePython)
  Dunit = g/cm3
  Dvalue = 1.42
  Group = -> [C_element025,H_element021,O_element026]
  conduct = 2
  density = 1
  expand = 3
  formula = G4_CELLULOSE_CELLOPHANE
  name = G4_CELLULOSE_CELLOPHANE
  specific = 4
FEATURE [App::DocumentObjectGroupPython] H_element022  label="H_element : 0.067"  # scripted group (container) (typed FeaturePython)
  n = 0.067125
FEATURE [App::DocumentObjectGroupPython] C_element026  label="C_element : 0.545"  # scripted group (container) (typed FeaturePython)
  n = 0.545403
FEATURE [App::DocumentObjectGroupPython] O_element027  label="O_element : 0.387"  # scripted group (container) (typed FeaturePython)
  n = 0.387472
FEATURE [App::DocumentObjectGroupPython] G4_CELLULOSE_BUTYRATE  # scripted group (container) (typed FeaturePython)
  Dunit = g/cm3
  Dvalue = 1.2
  Group = -> [H_element022,C_element026,O_element027]
  conduct = 2
  density = 1
  expand = 3
  formula = G4_CELLULOSE_BUTYRATE
  name = G4_CELLULOSE_BUTYRATE
  specific = 4
FEATURE [App::DocumentObjectGroupPython] H_element023  label="H_element : 0.029"  # scripted group (container) (typed FeaturePython)
  n = 0.029216
FEATURE [App::DocumentObjectGroupPython] C_element027  label="C_element : 0.271"  # scripted group (container) (typed FeaturePython)
  n = 0.271296
FEATURE [App::DocumentObjectGroupPython] N_element013  label="N_element : 0.121"  # scripted group (container) (typed FeaturePython)
  n = 0.121276
FEATURE [App::DocumentObjectGroupPython] O_element028  label="O_element : 0.578"  # scripted group (container) (typed FeaturePython)
  n = 0.578212
FEATURE [App::DocumentObjectGroupPython] G4_CELLULOSE_NITRATE  # scripted group (container) (typed FeaturePython)
  Dunit = g/cm3
  Dvalue = 1.49
  Group = -> [H_element023,C_element027,N_element013,O_element028]
  conduct = 2
  density = 1
  expand = 3
  formula = G4_CELLULOSE_NITRATE
  name = G4_CELLULOSE_NITRATE
  specific = 4
FEATURE [App::DocumentObjectGroupPython] H_element024  label="H_element : 0.108"  # scripted group (container) (typed FeaturePython)
  n = 0.107596
FEATURE [App::DocumentObjectGroupPython] N_element014  label="N_element : 0.001"  # scripted group (container) (typed FeaturePython)
  n = 0.0008
FEATURE [App::DocumentObjectGroupPython] O_element029  label="O_element : 0.875"  # scripted group (container) (typed FeaturePython)
  n = 0.874976
FEATURE [App::DocumentObjectGroupPython] S_element008  label="S_element : 0.015"  # scripted group (container) (typed FeaturePython)
  n = 0.014627
FEATURE [App::DocumentObjectGroupPython] Ce_element001  label="Ce_element : 0.002"  # scripted group (container) (typed FeaturePython)
  n = 0.002001
FEATURE [App::DocumentObjectGroupPython] G4_CERIC_SULFATE  # scripted group (container) (typed FeaturePython)
  Dunit = g/cm3
  Dvalue = 1.03
  Group = -> [H_element024,N_element014,O_element029,S_element008,Ce_element001]
  conduct = 2
  density = 1
  expand = 3
  formula = G4_CERIC_SULFATE
  name = G4_CERIC_SULFATE
  specific = 4
FEATURE [App::DocumentObjectGroupPython] Cs_element001  label="Cs_element : 1"  # scripted group (container) (typed FeaturePython)
  n = 1
  ref = Cs_element
FEATURE [App::DocumentObjectGroupPython] F_element006  label="F_element : 1"  # scripted group (container) (typed FeaturePython)
  n = 1
  ref = F_element
FEATURE [App::DocumentObjectGroupPython] G4_CESIUM_FLUORIDE  # scripted group (container) (typed FeaturePython)
  Dunit = g/cm3
  Dvalue = 4.115
  Group = -> [Cs_element001,F_element006]
  conduct = 2
  density = 1
  expand = 3
  formula = G4_CESIUM_FLUORIDE
  name = G4_CESIUM_FLUORIDE
  specific = 4
FEATURE [App::DocumentObjectGroupPython] Cs_element002  label="Cs_element : 002"  # scripted group (container) (typed FeaturePython)
  n = 1
  ref = Cs_element
FEATURE [App::DocumentObjectGroupPython] I_element001  label="I_element : 1"  # scripted group (container) (typed FeaturePython)
  n = 1
  ref = I_element
FEATURE [App::DocumentObjectGroupPython] G4_CESIUM_IODIDE  # scripted group (container) (typed FeaturePython)
  Dunit = g/cm3
  Dvalue = 4.51
  Group = -> [Cs_element002,I_element001]
  conduct = 2
  density = 1
  expand = 3
  formula = G4_CESIUM_IODIDE
  name = G4_CESIUM_IODIDE
  specific = 4
FEATURE [App::DocumentObjectGroupPython] C_element028  label="C_element : 013"  # scripted group (container) (typed FeaturePython)
  n = 6
  ref = C_element
FEATURE [App::DocumentObjectGroupPython] H_element025  label="H_element : 013"  # scripted group (container) (typed FeaturePython)
  n = 5
  ref = H_element
FEATURE [App::DocumentObjectGroupPython] Cl_element005  label="Cl_element : 1"  # scripted group (container) (typed FeaturePython)
  n = 1
  ref = Cl_element
FEATURE [App::DocumentObjectGroupPython] G4_CHLOROBENZENE  # scripted group (container) (typed FeaturePython)
  Dunit = g/cm3
  Dvalue = 1.1058
  Group = -> [C_element028,H_element025,Cl_element005]
  conduct = 2
  density = 1
  expand = 3
  formula = G4_CHLOROBENZENE
  name = G4_CHLOROBENZENE
  specific = 4
FEATURE [App::DocumentObjectGroupPython] C_element029  label="C_element : 014"  # scripted group (container) (typed FeaturePython)
  n = 1
  ref = C_element
FEATURE [App::DocumentObjectGroupPython] H_element026  label="H_element : 1"  # scripted group (container) (typed FeaturePython)
  n = 1
  ref = H_element
FEATURE [App::DocumentObjectGroupPython] Cl_element006  label="Cl_element : 3"  # scripted group (container) (typed FeaturePython)
  n = 3
  ref = Cl_element
FEATURE [App::DocumentObjectGroupPython] G4_CHLOROFORM  # scripted group (container) (typed FeaturePython)
  Dunit = g/cm3
  Dvalue = 1.4832
  Group = -> [C_element029,H_element026,Cl_element006]
  conduct = 2
  density = 1
  expand = 3
  formula = G4_CHLOROFORM
  name = G4_CHLOROFORM
  specific = 4
FEATURE [App::DocumentObjectGroupPython] H_element027  label="H_element : 0.010"  # scripted group (container) (typed FeaturePython)
  n = 0.01
FEATURE [App::DocumentObjectGroupPython] C_element030  label="C_element : 0.001"  # scripted group (container) (typed FeaturePython)
  n = 0.001
FEATURE [App::DocumentObjectGroupPython] O_element030  label="O_element : 0.529"  # scripted group (container) (typed FeaturePython)
  n = 0.529107
FEATURE [App::DocumentObjectGroupPython] Na_element005  label="Na_element : 0.016"  # scripted group (container) (typed FeaturePython)
  n = 0.016
FEATURE [App::DocumentObjectGroupPython] Mg_element003  label="Mg_element : 0.004"  # scripted group (container) (typed FeaturePython)
  n = 0.002
FEATURE [App::DocumentObjectGroupPython] Al_element002  label="Al_element : 0.034"  # scripted group (container) (typed FeaturePython)
  n = 0.033872
FEATURE [App::DocumentObjectGroupPython] Si_element002  label="Si_element : 0.337"  # scripted group (container) (typed FeaturePython)
  n = 0.337021
FEATURE [App::DocumentObjectGroupPython] K_element003  label="K_element : 0.013"  # scripted group (container) (typed FeaturePython)
  n = 0.013
FEATURE [App::DocumentObjectGroupPython] Ca_element010  label="Ca_element : 0.044"  # scripted group (container) (typed FeaturePython)
  n = 0.044
FEATURE [App::DocumentObjectGroupPython] Fe_element002  label="Fe_element : 0.014"  # scripted group (container) (typed FeaturePython)
  n = 0.014
FEATURE [App::DocumentObjectGroupPython] G4_CONCRETE  # scripted group (container) (typed FeaturePython)
  Dunit = g/cm3
  Dvalue = 2.3
  Group = -> [H_element027,C_element030,O_element030,Na_element005,Mg_element003,Al_element002,Si_element002,K_element003,Ca_element010,Fe_element002]
  conduct = 2
  density = 1
  expand = 3
  formula = G4_CONCRETE
  name = G4_CONCRETE
  specific = 4
FEATURE [App::DocumentObjectGroupPython] C_element031  label="C_element : 015"  # scripted group (container) (typed FeaturePython)
  n = 6
  ref = C_element
FEATURE [App::DocumentObjectGroupPython] H_element028  label="H_element : 12"  # scripted group (container) (typed FeaturePython)
  n = 12
  ref = H_element
FEATURE [App::DocumentObjectGroupPython] G4_CYCLOHEXANE  # scripted group (container) (typed FeaturePython)
  Dunit = g/cm3
  Dvalue = 0.779
  Group = -> [C_element031,H_element028]
  conduct = 2
  density = 1
  expand = 3
  formula = G4_CYCLOHEXANE
  name = G4_CYCLOHEXANE
  specific = 4
FEATURE [App::DocumentObjectGroupPython] C_element032  label="C_element : 016"  # scripted group (container) (typed FeaturePython)
  n = 6
  ref = C_element
FEATURE [App::DocumentObjectGroupPython] H_element029  label="H_element : 4"  # scripted group (container) (typed FeaturePython)
  n = 4
  ref = H_element
FEATURE [App::DocumentObjectGroupPython] Cl_element007  label="Cl_element : 2"  # scripted group (container) (typed FeaturePython)
  n = 2
  ref = Cl_element
FEATURE [App::DocumentObjectGroupPython] G4_1_2_DICHLOROBENZENE  label="G4_1.2-DICHLOROBENZENE"  # scripted group (container) (typed FeaturePython)
  Dunit = g/cm3
  Dvalue = 1.3048
  Group = -> [C_element032,H_element029,Cl_element007]
  conduct = 2
  density = 1
  expand = 3
  formula = G4_1.2-DICHLOROBENZENE
  name = G4_1.2-DICHLOROBENZENE
  specific = 4
FEATURE [App::DocumentObjectGroupPython] C_element033  label="C_element : 017"  # scripted group (container) (typed FeaturePython)
  n = 4
  ref = C_element
FEATURE [App::DocumentObjectGroupPython] H_element030  label="H_element : 8"  # scripted group (container) (typed FeaturePython)
  n = 8
  ref = H_element
FEATURE [App::DocumentObjectGroupPython] O_element031  label="O_element : 014"  # scripted group (container) (typed FeaturePython)
  n = 1
  ref = O_element
FEATURE [App::DocumentObjectGroupPython] Cl_element008  label="Cl_element : 005"  # scripted group (container) (typed FeaturePython)
  n = 2
  ref = Cl_element
FEATURE [App::DocumentObjectGroupPython] G4_DICHLORODIETHYL_ETHER  # scripted group (container) (typed FeaturePython)
  Dunit = g/cm3
  Dvalue = 1.2199
  Group = -> [C_element033,H_element030,O_element031,Cl_element008]
  conduct = 2
  density = 1
  expand = 3
  formula = G4_DICHLORODIETHYL_ETHER
  name = G4_DICHLORODIETHYL_ETHER
  specific = 4
FEATURE [App::DocumentObjectGroupPython] C_element034  label="C_element : 018"  # scripted group (container) (typed FeaturePython)
  n = 2
  ref = C_element
FEATURE [App::DocumentObjectGroupPython] H_element031  label="H_element : 014"  # scripted group (container) (typed FeaturePython)
  n = 4
  ref = H_element
FEATURE [App::DocumentObjectGroupPython] Cl_element009  label="Cl_element : 006"  # scripted group (container) (typed FeaturePython)
  n = 2
  ref = Cl_element
FEATURE [App::DocumentObjectGroupPython] G4_1_2_DICHLOROETHANE  label="G4_1.2-DICHLOROETHANE"  # scripted group (container) (typed FeaturePython)
  Dunit = g/cm3
  Dvalue = 1.2351
  Group = -> [C_element034,H_element031,Cl_element009]
  conduct = 2
  density = 1
  expand = 3
  formula = G4_1.2-DICHLOROETHANE
  name = G4_1.2-DICHLOROETHANE
  specific = 4
FEATURE [App::DocumentObjectGroupPython] C_element035  label="C_element : 019"  # scripted group (container) (typed FeaturePython)
  n = 4
  ref = C_element
FEATURE [App::DocumentObjectGroupPython] H_element032  label="H_element : 015"  # scripted group (container) (typed FeaturePython)
  n = 10
  ref = H_element
FEATURE [App::DocumentObjectGroupPython] O_element032  label="O_element : 015"  # scripted group (container) (typed FeaturePython)
  n = 1
  ref = O_element
FEATURE [App::DocumentObjectGroupPython] G4_DIETHYL_ETHER  # scripted group (container) (typed FeaturePython)
  Dunit = g/cm3
  Dvalue = 0.71378
  Group = -> [C_element035,H_element032,O_element032]
  conduct = 2
  density = 1
  expand = 3
  formula = G4_DIETHYL_ETHER
  name = G4_DIETHYL_ETHER
  specific = 4
FEATURE [App::DocumentObjectGroupPython] C_element036  label="C_element : 020"  # scripted group (container) (typed FeaturePython)
  n = 3
  ref = C_element
FEATURE [App::DocumentObjectGroupPython] H_element033  label="H_element : 016"  # scripted group (container) (typed FeaturePython)
  n = 7
  ref = H_element
FEATURE [App::DocumentObjectGroupPython] N_element015  label="N_element : 008"  # scripted group (container) (typed FeaturePython)
  n = 1
  ref = N_element
FEATURE [App::DocumentObjectGroupPython] O_element033  label="O_element : 016"  # scripted group (container) (typed FeaturePython)
  n = 1
  ref = O_element
FEATURE [App::DocumentObjectGroupPython] G4_N_N_DIMETHYL_FORMAMIDE  label="G4_N.N-DIMETHYL_FORMAMIDE"  # scripted group (container) (typed FeaturePython)
  Dunit = g/cm3
  Dvalue = 0.9487
  Group = -> [C_element036,H_element033,N_element015,O_element033]
  conduct = 2
  density = 1
  expand = 3
  formula = G4_N.N-DIMETHYL_FORMAMIDE
  name = G4_N.N-DIMETHYL_FORMAMIDE
  specific = 4
FEATURE [App::DocumentObjectGroupPython] C_element037  label="C_element : 021"  # scripted group (container) (typed FeaturePython)
  n = 2
  ref = C_element
FEATURE [App::DocumentObjectGroupPython] H_element034  label="H_element : 017"  # scripted group (container) (typed FeaturePython)
  n = 6
  ref = H_element
FEATURE [App::DocumentObjectGroupPython] O_element034  label="O_element : 017"  # scripted group (container) (typed FeaturePython)
  n = 1
  ref = O_element
FEATURE [App::DocumentObjectGroupPython] S_element009  label="S_element : 003"  # scripted group (container) (typed FeaturePython)
  n = 1
  ref = S_element
FEATURE [App::DocumentObjectGroupPython] G4_DIMETHYL_SULFOXIDE  # scripted group (container) (typed FeaturePython)
  Dunit = g/cm3
  Dvalue = 1.1014
  Group = -> [C_element037,H_element034,O_element034,S_element009]
  conduct = 2
  density = 1
  expand = 3
  formula = G4_DIMETHYL_SULFOXIDE
  name = G4_DIMETHYL_SULFOXIDE
  specific = 4
FEATURE [App::DocumentObjectGroupPython] C_element038  label="C_element : 022"  # scripted group (container) (typed FeaturePython)
  n = 2
  ref = C_element
FEATURE [App::DocumentObjectGroupPython] H_element035  label="H_element : 018"  # scripted group (container) (typed FeaturePython)
  n = 6
  ref = H_element
FEATURE [App::DocumentObjectGroupPython] G4_ETHANE  # scripted group (container) (typed FeaturePython)
  Dunit = g/cm3
  Dvalue = 0.00125324
  Group = -> [C_element038,H_element035]
  conduct = 2
  density = 1
  expand = 3
  formula = G4_ETHANE
  name = G4_ETHANE
  specific = 4
FEATURE [App::DocumentObjectGroupPython] C_element039  label="C_element : 023"  # scripted group (container) (typed FeaturePython)
  n = 2
  ref = C_element
FEATURE [App::DocumentObjectGroupPython] H_element036  label="H_element : 019"  # scripted group (container) (typed FeaturePython)
  n = 6
  ref = H_element
FEATURE [App::DocumentObjectGroupPython] O_element035  label="O_element : 018"  # scripted group (container) (typed FeaturePython)
  n = 1
  ref = O_element
FEATURE [App::DocumentObjectGroupPython] G4_ETHYL_ALCOHOL  # scripted group (container) (typed FeaturePython)
  Dunit = g/cm3
  Dvalue = 0.7893
  Group = -> [C_element039,H_element036,O_element035]
  conduct = 2
  density = 1
  expand = 3
  formula = G4_ETHYL_ALCOHOL
  name = G4_ETHYL_ALCOHOL
  specific = 4
FEATURE [App::DocumentObjectGroupPython] H_element037  label="H_element : 0.090"  # scripted group (container) (typed FeaturePython)
  n = 0.090027
FEATURE [App::DocumentObjectGroupPython] C_element040  label="C_element : 0.585"  # scripted group (container) (typed FeaturePython)
  n = 0.585182
FEATURE [App::DocumentObjectGroupPython] O_element036  label="O_element : 0.325"  # scripted group (container) (typed FeaturePython)
  n = 0.324791
FEATURE [App::DocumentObjectGroupPython] G4_ETHYL_CELLULOSE  # scripted group (container) (typed FeaturePython)
  Dunit = g/cm3
  Dvalue = 1.13
  Group = -> [H_element037,C_element040,O_element036]
  conduct = 2
  density = 1
  expand = 3
  formula = G4_ETHYL_CELLULOSE
  name = G4_ETHYL_CELLULOSE
  specific = 4
FEATURE [App::DocumentObjectGroupPython] C_element041  label="C_element : 024"  # scripted group (container) (typed FeaturePython)
  n = 2
  ref = C_element
FEATURE [App::DocumentObjectGroupPython] H_element038  label="H_element : 020"  # scripted group (container) (typed FeaturePython)
  n = 4
  ref = H_element
FEATURE [App::DocumentObjectGroupPython] G4_ETHYLENE  # scripted group (container) (typed FeaturePython)
  Dunit = g/cm3
  Dvalue = 0.00117497
  Group = -> [C_element041,H_element038]
  conduct = 2
  density = 1
  expand = 3
  formula = G4_ETHYLENE
  name = G4_ETHYLENE
  specific = 4
FEATURE [App::DocumentObjectGroupPython] H_element039  label="H_element : 0.096"  # scripted group (container) (typed FeaturePython)
  n = 0.096
FEATURE [App::DocumentObjectGroupPython] C_element042  label="C_element : 0.195"  # scripted group (container) (typed FeaturePython)
  n = 0.195
FEATURE [App::DocumentObjectGroupPython] N_element016  label="N_element : 0.057"  # scripted group (container) (typed FeaturePython)
  n = 0.057
FEATURE [App::DocumentObjectGroupPython] O_element037  label="O_element : 0.646"  # scripted group (container) (typed FeaturePython)
  n = 0.646
FEATURE [App::DocumentObjectGroupPython] Na_element006  label="Na_element : 0.017"  # scripted group (container) (typed FeaturePython)
  n = 0.001
FEATURE [App::DocumentObjectGroupPython] P_element005  label="P_element : 0.104"  # scripted group (container) (typed FeaturePython)
  n = 0.001
FEATURE [App::DocumentObjectGroupPython] S_element010  label="S_element : 0.016"  # scripted group (container) (typed FeaturePython)
  n = 0.003
FEATURE [App::DocumentObjectGroupPython] Cl_element010  label="Cl_element : 0.005"  # scripted group (container) (typed FeaturePython)
  n = 0.001
FEATURE [App::DocumentObjectGroupPython] G4_EYE_LENS_ICRP  # scripted group (container) (typed FeaturePython)
  Dunit = g/cm3
  Dvalue = 1.07
  Group = -> [H_element039,C_element042,N_element016,O_element037,Na_element006,P_element005,S_element010,Cl_element010]
  conduct = 2
  density = 1
  expand = 3
  formula = G4_EYE_LENS_ICRP
  name = G4_EYE_LENS_ICRP
  specific = 4
FEATURE [App::DocumentObjectGroupPython] Fe_element003  label="Fe_element : 2"  # scripted group (container) (typed FeaturePython)
  n = 2
  ref = Fe_element
FEATURE [App::DocumentObjectGroupPython] O_element038  label="O_element : 019"  # scripted group (container) (typed FeaturePython)
  n = 3
  ref = O_element
FEATURE [App::DocumentObjectGroupPython] G4_FERRIC_OXIDE  # scripted group (container) (typed FeaturePython)
  Dunit = g/cm3
  Dvalue = 5.2
  Group = -> [Fe_element003,O_element038]
  conduct = 2
  density = 1
  expand = 3
  formula = G4_FERRIC_OXIDE
  name = G4_FERRIC_OXIDE
  specific = 4
FEATURE [App::DocumentObjectGroupPython] Fe_element004  label="Fe_element : 1"  # scripted group (container) (typed FeaturePython)
  n = 1
  ref = Fe_element
FEATURE [App::DocumentObjectGroupPython] B_element003  label="B_element : 1"  # scripted group (container) (typed FeaturePython)
  n = 1
  ref = B_element
FEATURE [App::DocumentObjectGroupPython] G4_FERROBORIDE  # scripted group (container) (typed FeaturePython)
  Dunit = g/cm3
  Dvalue = 7.15
  Group = -> [Fe_element004,B_element003]
  conduct = 2
  density = 1
  expand = 3
  formula = G4_FERROBORIDE
  name = G4_FERROBORIDE
  specific = 4
FEATURE [App::DocumentObjectGroupPython] Fe_element005  label="Fe_element : 003"  # scripted group (container) (typed FeaturePython)
  n = 1
  ref = Fe_element
FEATURE [App::DocumentObjectGroupPython] O_element039  label="O_element : 020"  # scripted group (container) (typed FeaturePython)
  n = 1
  ref = O_element
FEATURE [App::DocumentObjectGroupPython] G4_FERROUS_OXIDE  # scripted group (container) (typed FeaturePython)
  Dunit = g/cm3
  Dvalue = 5.7
  Group = -> [Fe_element005,O_element039]
  conduct = 2
  density = 1
  expand = 3
  formula = G4_FERROUS_OXIDE
  name = G4_FERROUS_OXIDE
  specific = 4
FEATURE [App::DocumentObjectGroupPython] H_element040  label="H_element : 0.115"  # scripted group (container) (typed FeaturePython)
  n = 0.108259
FEATURE [App::DocumentObjectGroupPython] N_element017  label="N_element : 0.000"  # scripted group (container) (typed FeaturePython)
  n = 2.7e-05
FEATURE [App::DocumentObjectGroupPython] O_element040  label="O_element : 0.879"  # scripted group (container) (typed FeaturePython)
  n = 0.878636
FEATURE [App::DocumentObjectGroupPython] Na_element007  label="Na_element : 0.000"  # scripted group (container) (typed FeaturePython)
  n = 2.2e-05
FEATURE [App::DocumentObjectGroupPython] S_element011  label="S_element : 0.013"  # scripted group (container) (typed FeaturePython)
  n = 0.012968
FEATURE [App::DocumentObjectGroupPython] Cl_element011  label="Cl_element : 0.000"  # scripted group (container) (typed FeaturePython)
  n = 3.4e-05
FEATURE [App::DocumentObjectGroupPython] Fe_element006  label="Fe_element : 0.000"  # scripted group (container) (typed FeaturePython)
  n = 5.4e-05
FEATURE [App::DocumentObjectGroupPython] G4_FERROUS_SULFATE  # scripted group (container) (typed FeaturePython)
  Dunit = g/cm3
  Dvalue = 1.024
  Group = -> [H_element040,N_element017,O_element040,Na_element007,S_element011,Cl_element011,Fe_element006]
  conduct = 2
  density = 1
  expand = 3
  formula = G4_FERROUS_SULFATE
  name = G4_FERROUS_SULFATE
  specific = 4
FEATURE [App::DocumentObjectGroupPython] C_element043  label="C_element : 0.099"  # scripted group (container) (typed FeaturePython)
  n = 0.099335
FEATURE [App::DocumentObjectGroupPython] F_element007  label="F_element : 0.314"  # scripted group (container) (typed FeaturePython)
  n = 0.314247
FEATURE [App::DocumentObjectGroupPython] Cl_element012  label="Cl_element : 0.586"  # scripted group (container) (typed FeaturePython)
  n = 0.586418
FEATURE [App::DocumentObjectGroupPython] G4_FREON_12  label="G4_FREON-12"  # scripted group (container) (typed FeaturePython)
  Dunit = g/cm3
  Dvalue = 1.12
  Group = -> [C_element043,F_element007,Cl_element012]
  conduct = 2
  density = 1
  expand = 3
  formula = G4_FREON-12
  name = G4_FREON-12
  specific = 4
FEATURE [App::DocumentObjectGroupPython] C_element044  label="C_element : 0.057"  # scripted group (container) (typed FeaturePython)
  n = 0.057245
FEATURE [App::DocumentObjectGroupPython] F_element008  label="F_element : 0.181"  # scripted group (container) (typed FeaturePython)
  n = 0.181096
FEATURE [App::DocumentObjectGroupPython] Br_element001  label="Br_element : 0.762"  # scripted group (container) (typed FeaturePython)
  n = 0.761659
FEATURE [App::DocumentObjectGroupPython] G4_FREON_12B2  label="G4_FREON-12B2"  # scripted group (container) (typed FeaturePython)
  Dunit = g/cm3
  Dvalue = 1.8
  Group = -> [C_element044,F_element008,Br_element001]
  conduct = 2
  density = 1
  expand = 3
  formula = G4_FREON-12B2
  name = G4_FREON-12B2
  specific = 4
FEATURE [App::DocumentObjectGroupPython] C_element045  label="C_element : 0.115"  # scripted group (container) (typed FeaturePython)
  n = 0.114983
FEATURE [App::DocumentObjectGroupPython] F_element009  label="F_element : 0.546"  # scripted group (container) (typed FeaturePython)
  n = 0.545621
FEATURE [App::DocumentObjectGroupPython] Cl_element013  label="Cl_element : 0.339"  # scripted group (container) (typed FeaturePython)
  n = 0.339396
FEATURE [App::DocumentObjectGroupPython] G4_FREON_13  label="G4_FREON-13"  # scripted group (container) (typed FeaturePython)
  Dunit = g/cm3
  Dvalue = 0.95
  Group = -> [C_element045,F_element009,Cl_element013]
  conduct = 2
  density = 1
  expand = 3
  formula = G4_FREON-13
  name = G4_FREON-13
  specific = 4
FEATURE [App::DocumentObjectGroupPython] C_element046  label="C_element : 025"  # scripted group (container) (typed FeaturePython)
  n = 1
  ref = C_element
FEATURE [App::DocumentObjectGroupPython] F_element010  label="F_element : 3"  # scripted group (container) (typed FeaturePython)
  n = 3
  ref = F_element
FEATURE [App::DocumentObjectGroupPython] Br_element002  label="Br_element : 1"  # scripted group (container) (typed FeaturePython)
  n = 1
  ref = Br_element
FEATURE [App::DocumentObjectGroupPython] G4_FREON_13B1  label="G4_FREON-13B1"  # scripted group (container) (typed FeaturePython)
  Dunit = g/cm3
  Dvalue = 1.5
  Group = -> [C_element046,F_element010,Br_element002]
  conduct = 2
  density = 1
  expand = 3
  formula = G4_FREON-13B1
  name = G4_FREON-13B1
  specific = 4
FEATURE [App::DocumentObjectGroupPython] C_element047  label="C_element : 0.061"  # scripted group (container) (typed FeaturePython)
  n = 0.061309
FEATURE [App::DocumentObjectGroupPython] F_element011  label="F_element : 0.291"  # scripted group (container) (typed FeaturePython)
  n = 0.290924
FEATURE [App::DocumentObjectGroupPython] I_element002  label="I_element : 0.648"  # scripted group (container) (typed FeaturePython)
  n = 0.647767
FEATURE [App::DocumentObjectGroupPython] G4_FREON_13I1  label="G4_FREON-13I1"  # scripted group (container) (typed FeaturePython)
  Dunit = g/cm3
  Dvalue = 1.8
  Group = -> [C_element047,F_element011,I_element002]
  conduct = 2
  density = 1
  expand = 3
  formula = G4_FREON-13I1
  name = G4_FREON-13I1
  specific = 4
FEATURE [App::DocumentObjectGroupPython] Gd_element001  label="Gd_element : 2"  # scripted group (container) (typed FeaturePython)
  n = 2
  ref = Gd_element
FEATURE [App::DocumentObjectGroupPython] O_element041  label="O_element : 021"  # scripted group (container) (typed FeaturePython)
  n = 2
  ref = O_element
FEATURE [App::DocumentObjectGroupPython] S_element012  label="S_element : 004"  # scripted group (container) (typed FeaturePython)
  n = 1
  ref = S_element
FEATURE [App::DocumentObjectGroupPython] G4_GADOLINIUM_OXYSULFIDE  # scripted group (container) (typed FeaturePython)
  Dunit = g/cm3
  Dvalue = 7.44
  Group = -> [Gd_element001,O_element041,S_element012]
  conduct = 2
  density = 1
  expand = 3
  formula = G4_GADOLINIUM_OXYSULFIDE
  name = G4_GADOLINIUM_OXYSULFIDE
  specific = 4
FEATURE [App::DocumentObjectGroupPython] Ga_element001  label="Ga_element : 1"  # scripted group (container) (typed FeaturePython)
  n = 1
  ref = Ga_element
FEATURE [App::DocumentObjectGroupPython] As_element001  label="As_element : 1"  # scripted group (container) (typed FeaturePython)
  n = 1
  ref = As_element
FEATURE [App::DocumentObjectGroupPython] G4_GALLIUM_ARSENIDE  # scripted group (container) (typed FeaturePython)
  Dunit = g/cm3
  Dvalue = 5.31
  Group = -> [Ga_element001,As_element001]
  conduct = 2
  density = 1
  expand = 3
  formula = G4_GALLIUM_ARSENIDE
  name = G4_GALLIUM_ARSENIDE
  specific = 4
FEATURE [App::DocumentObjectGroupPython] H_element041  label="H_element : 0.081"  # scripted group (container) (typed FeaturePython)
  n = 0.08118
FEATURE [App::DocumentObjectGroupPython] C_element048  label="C_element : 0.416"  # scripted group (container) (typed FeaturePython)
  n = 0.41606
FEATURE [App::DocumentObjectGroupPython] N_element018  label="N_element : 0.111"  # scripted group (container) (typed FeaturePython)
  n = 0.11124
FEATURE [App::DocumentObjectGroupPython] O_element042  label="O_element : 0.381"  # scripted group (container) (typed FeaturePython)
  n = 0.38064
FEATURE [App::DocumentObjectGroupPython] S_element013  label="S_element : 0.011"  # scripted group (container) (typed FeaturePython)
  n = 0.01088
FEATURE [App::DocumentObjectGroupPython] G4_GEL_PHOTO_EMULSION  # scripted group (container) (typed FeaturePython)
  Dunit = g/cm3
  Dvalue = 1.2914
  Group = -> [H_element041,C_element048,N_element018,O_element042,S_element013]
  conduct = 2
  density = 1
  expand = 3
  formula = G4_GEL_PHOTO_EMULSION
  name = G4_GEL_PHOTO_EMULSION
  specific = 4
FEATURE [App::DocumentObjectGroupPython] B_element004  label="B_element : 0.040"  # scripted group (container) (typed FeaturePython)
  n = 0.0400639
FEATURE [App::DocumentObjectGroupPython] O_element043  label="O_element : 0.540"  # scripted group (container) (typed FeaturePython)
  n = 0.539561
FEATURE [App::DocumentObjectGroupPython] Na_element008  label="Na_element : 0.028"  # scripted group (container) (typed FeaturePython)
  n = 0.0281909
FEATURE [App::DocumentObjectGroupPython] Al_element003  label="Al_element : 0.012"  # scripted group (container) (typed FeaturePython)
  n = 0.011644
FEATURE [App::DocumentObjectGroupPython] Si_element003  label="Si_element : 0.377"  # scripted group (container) (typed FeaturePython)
  n = 0.377219
FEATURE [App::DocumentObjectGroupPython] K_element004  label="K_element : 0.014"  # scripted group (container) (typed FeaturePython)
  n = 0.00332099
FEATURE [App::DocumentObjectGroupPython] G4_Pyrex_Glass  # scripted group (container) (typed FeaturePython)
  Dunit = g/cm3
  Dvalue = 2.23
  Group = -> [B_element004,O_element043,Na_element008,Al_element003,Si_element003,K_element004]
  conduct = 2
  density = 1
  expand = 3
  formula = G4_Pyrex_Glass
  name = G4_Pyrex_Glass
  specific = 4
FEATURE [App::DocumentObjectGroupPython] O_element044  label="O_element : 0.156"  # scripted group (container) (typed FeaturePython)
  n = 0.156453
FEATURE [App::DocumentObjectGroupPython] Si_element004  label="Si_element : 0.081"  # scripted group (container) (typed FeaturePython)
  n = 0.080866
FEATURE [App::DocumentObjectGroupPython] Ti_element001  label="Ti_element : 0.008"  # scripted group (container) (typed FeaturePython)
  n = 0.008092
FEATURE [App::DocumentObjectGroupPython] As_element002  label="As_element : 0.003"  # scripted group (container) (typed FeaturePython)
  n = 0.002651
FEATURE [App::DocumentObjectGroupPython] Pb_element001  label="Pb_element : 0.752"  # scripted group (container) (typed FeaturePython)
  n = 0.751938
FEATURE [App::DocumentObjectGroupPython] G4_GLASS_LEAD  # scripted group (container) (typed FeaturePython)
  Dunit = g/cm3
  Dvalue = 6.22
  Group = -> [O_element044,Si_element004,Ti_element001,As_element002,Pb_element001]
  conduct = 2
  density = 1
  expand = 3
  formula = G4_GLASS_LEAD
  name = G4_GLASS_LEAD
  specific = 4
FEATURE [App::DocumentObjectGroupPython] O_element045  label="O_element : 0.460"  # scripted group (container) (typed FeaturePython)
  n = 0.4598
FEATURE [App::DocumentObjectGroupPython] Na_element009  label="Na_element : 0.096"  # scripted group (container) (typed FeaturePython)
  n = 0.0964411
FEATURE [App::DocumentObjectGroupPython] Si_element005  label="Si_element : 0.378"  # scripted group (container) (typed FeaturePython)
  n = 0.336553
FEATURE [App::DocumentObjectGroupPython] Ca_element011  label="Ca_element : 0.107"  # scripted group (container) (typed FeaturePython)
  n = 0.107205
FEATURE [App::DocumentObjectGroupPython] G4_GLASS_PLATE  # scripted group (container) (typed FeaturePython)
  Dunit = g/cm3
  Dvalue = 2.4
  Group = -> [O_element045,Na_element009,Si_element005,Ca_element011]
  conduct = 2
  density = 1
  expand = 3
  formula = G4_GLASS_PLATE
  name = G4_GLASS_PLATE
  specific = 4
FEATURE [App::DocumentObjectGroupPython] C_element049  label="C_element : 026"  # scripted group (container) (typed FeaturePython)
  n = 5
  ref = C_element
FEATURE [App::DocumentObjectGroupPython] H_element042  label="H_element : 021"  # scripted group (container) (typed FeaturePython)
  n = 10
  ref = H_element
FEATURE [App::DocumentObjectGroupPython] N_element019  label="N_element : 2"  # scripted group (container) (typed FeaturePython)
  n = 2
  ref = N_element
FEATURE [App::DocumentObjectGroupPython] O_element046  label="O_element : 022"  # scripted group (container) (typed FeaturePython)
  n = 3
  ref = O_element
FEATURE [App::DocumentObjectGroupPython] G4_GLUTAMINE  # scripted group (container) (typed FeaturePython)
  Dunit = g/cm3
  Dvalue = 1.46
  Group = -> [C_element049,H_element042,N_element019,O_element046]
  conduct = 2
  density = 1
  expand = 3
  formula = G4_GLUTAMINE
  name = G4_GLUTAMINE
  specific = 4
FEATURE [App::DocumentObjectGroupPython] C_element050  label="C_element : 027"  # scripted group (container) (typed FeaturePython)
  n = 3
  ref = C_element
FEATURE [App::DocumentObjectGroupPython] H_element043  label="H_element : 022"  # scripted group (container) (typed FeaturePython)
  n = 8
  ref = H_element
FEATURE [App::DocumentObjectGroupPython] O_element047  label="O_element : 023"  # scripted group (container) (typed FeaturePython)
  n = 3
  ref = O_element
FEATURE [App::DocumentObjectGroupPython] G4_GLYCEROL  # scripted group (container) (typed FeaturePython)
  Dunit = g/cm3
  Dvalue = 1.2613
  Group = -> [C_element050,H_element043,O_element047]
  conduct = 2
  density = 1
  expand = 3
  formula = G4_GLYCEROL
  name = G4_GLYCEROL
  specific = 4
FEATURE [App::DocumentObjectGroupPython] C_element051  label="C_element : 028"  # scripted group (container) (typed FeaturePython)
  n = 5
  ref = C_element
FEATURE [App::DocumentObjectGroupPython] H_element044  label="H_element : 023"  # scripted group (container) (typed FeaturePython)
  n = 5
  ref = H_element
FEATURE [App::DocumentObjectGroupPython] N_element020  label="N_element : 009"  # scripted group (container) (typed FeaturePython)
  n = 5
  ref = N_element
FEATURE [App::DocumentObjectGroupPython] O_element048  label="O_element : 024"  # scripted group (container) (typed FeaturePython)
  n = 1
  ref = O_element
FEATURE [App::DocumentObjectGroupPython] G4_GUANINE  # scripted group (container) (typed FeaturePython)
  Dunit = g/cm3
  Dvalue = 2.2
  Group = -> [C_element051,H_element044,N_element020,O_element048]
  conduct = 2
  density = 1
  expand = 3
  formula = G4_GUANINE
  name = G4_GUANINE
  specific = 4
FEATURE [App::DocumentObjectGroupPython] Ca_element012  label="Ca_element : 006"  # scripted group (container) (typed FeaturePython)
  n = 1
  ref = Ca_element
FEATURE [App::DocumentObjectGroupPython] S_element014  label="S_element : 005"  # scripted group (container) (typed FeaturePython)
  n = 1
  ref = S_element
FEATURE [App::DocumentObjectGroupPython] O_element049  label="O_element : 6"  # scripted group (container) (typed FeaturePython)
  n = 6
  ref = O_element
FEATURE [App::DocumentObjectGroupPython] H_element045  label="H_element : 024"  # scripted group (container) (typed FeaturePython)
  n = 4
  ref = H_element
FEATURE [App::DocumentObjectGroupPython] G4_GYPSUM  # scripted group (container) (typed FeaturePython)
  Dunit = g/cm3
  Dvalue = 2.32
  Group = -> [Ca_element012,S_element014,O_element049,H_element045]
  conduct = 2
  density = 1
  expand = 3
  formula = G4_GYPSUM
  name = G4_GYPSUM
  specific = 4
FEATURE [App::DocumentObjectGroupPython] C_element052  label="C_element : 7"  # scripted group (container) (typed FeaturePython)
  n = 7
  ref = C_element
FEATURE [App::DocumentObjectGroupPython] H_element046  label="H_element : 16"  # scripted group (container) (typed FeaturePython)
  n = 16
  ref = H_element
FEATURE [App::DocumentObjectGroupPython] G4_N_HEPTANE  label="G4_N-HEPTANE"  # scripted group (container) (typed FeaturePython)
  Dunit = g/cm3
  Dvalue = 0.68376
  Group = -> [C_element052,H_element046]
  conduct = 2
  density = 1
  expand = 3
  formula = G4_N-HEPTANE
  name = G4_N-HEPTANE
  specific = 4
FEATURE [App::DocumentObjectGroupPython] C_element053  label="C_element : 029"  # scripted group (container) (typed FeaturePython)
  n = 6
  ref = C_element
FEATURE [App::DocumentObjectGroupPython] H_element047  label="H_element : 14"  # scripted group (container) (typed FeaturePython)
  n = 14
  ref = H_element
FEATURE [App::DocumentObjectGroupPython] G4_N_HEXANE  label="G4_N-HEXANE"  # scripted group (container) (typed FeaturePython)
  Dunit = g/cm3
  Dvalue = 0.6603
  Group = -> [C_element053,H_element047]
  conduct = 2
  density = 1
  expand = 3
  formula = G4_N-HEXANE
  name = G4_N-HEXANE
  specific = 4
FEATURE [App::DocumentObjectGroupPython] C_element054  label="C_element : 22"  # scripted group (container) (typed FeaturePython)
  n = 22
  ref = C_element
FEATURE [App::DocumentObjectGroupPython] H_element048  label="H_element : 025"  # scripted group (container) (typed FeaturePython)
  n = 10
  ref = H_element
FEATURE [App::DocumentObjectGroupPython] N_element021  label="N_element : 010"  # scripted group (container) (typed FeaturePython)
  n = 2
  ref = N_element
FEATURE [App::DocumentObjectGroupPython] O_element050  label="O_element : 025"  # scripted group (container) (typed FeaturePython)
  n = 5
  ref = O_element
FEATURE [App::DocumentObjectGroupPython] G4_KAPTON  # scripted group (container) (typed FeaturePython)
  Dunit = g/cm3
  Dvalue = 1.42
  Group = -> [C_element054,H_element048,N_element021,O_element050]
  conduct = 2
  density = 1
  expand = 3
  formula = G4_KAPTON
  name = G4_KAPTON
  specific = 4
FEATURE [App::DocumentObjectGroupPython] La_element001  label="La_element : 1"  # scripted group (container) (typed FeaturePython)
  n = 1
  ref = La_element
FEATURE [App::DocumentObjectGroupPython] Br_element003  label="Br_element : 002"  # scripted group (container) (typed FeaturePython)
  n = 1
  ref = Br_element
FEATURE [App::DocumentObjectGroupPython] O_element051  label="O_element : 026"  # scripted group (container) (typed FeaturePython)
  n = 1
  ref = O_element
FEATURE [App::DocumentObjectGroupPython] G4_LANTHANUM_OXYBROMIDE  # scripted group (container) (typed FeaturePython)
  Dunit = g/cm3
  Dvalue = 6.28
  Group = -> [La_element001,Br_element003,O_element051]
  conduct = 2
  density = 1
  expand = 3
  formula = G4_LANTHANUM_OXYBROMIDE
  name = G4_LANTHANUM_OXYBROMIDE
  specific = 4
FEATURE [App::DocumentObjectGroupPython] La_element002  label="La_element : 2"  # scripted group (container) (typed FeaturePython)
  n = 2
  ref = La_element
FEATURE [App::DocumentObjectGroupPython] O_element052  label="O_element : 027"  # scripted group (container) (typed FeaturePython)
  n = 2
  ref = O_element
FEATURE [App::DocumentObjectGroupPython] S_element015  label="S_element : 006"  # scripted group (container) (typed FeaturePython)
  n = 1
  ref = S_element
FEATURE [App::DocumentObjectGroupPython] G4_LANTHANUM_OXYSULFIDE  # scripted group (container) (typed FeaturePython)
  Dunit = g/cm3
  Dvalue = 5.86
  Group = -> [La_element002,O_element052,S_element015]
  conduct = 2
  density = 1
  expand = 3
  formula = G4_LANTHANUM_OXYSULFIDE
  name = G4_LANTHANUM_OXYSULFIDE
  specific = 4
FEATURE [App::DocumentObjectGroupPython] O_element053  label="O_element : 0.072"  # scripted group (container) (typed FeaturePython)
  n = 0.071682
FEATURE [App::DocumentObjectGroupPython] Pb_element002  label="Pb_element : 0.928"  # scripted group (container) (typed FeaturePython)
  n = 0.928318
FEATURE [App::DocumentObjectGroupPython] G4_LEAD_OXIDE  # scripted group (container) (typed FeaturePython)
  Dunit = g/cm3
  Dvalue = 9.53
  Group = -> [O_element053,Pb_element002]
  conduct = 2
  density = 1
  expand = 3
  formula = G4_LEAD_OXIDE
  name = G4_LEAD_OXIDE
  specific = 4
FEATURE [App::DocumentObjectGroupPython] Li_element001  label="Li_element : 1"  # scripted group (container) (typed FeaturePython)
  n = 1
  ref = Li_element
FEATURE [App::DocumentObjectGroupPython] N_element022  label="N_element : 011"  # scripted group (container) (typed FeaturePython)
  n = 1
  ref = N_element
FEATURE [App::DocumentObjectGroupPython] H_element049  label="H_element : 026"  # scripted group (container) (typed FeaturePython)
  n = 2
  ref = H_element
FEATURE [App::DocumentObjectGroupPython] G4_LITHIUM_AMIDE  # scripted group (container) (typed FeaturePython)
  Dunit = g/cm3
  Dvalue = 1.178
  Group = -> [Li_element001,N_element022,H_element049]
  conduct = 2
  density = 1
  expand = 3
  formula = G4_LITHIUM_AMIDE
  name = G4_LITHIUM_AMIDE
  specific = 4
FEATURE [App::DocumentObjectGroupPython] Li_element002  label="Li_element : 2"  # scripted group (container) (typed FeaturePython)
  n = 2
  ref = Li_element
FEATURE [App::DocumentObjectGroupPython] C_element055  label="C_element : 030"  # scripted group (container) (typed FeaturePython)
  n = 1
  ref = C_element
FEATURE [App::DocumentObjectGroupPython] O_element054  label="O_element : 028"  # scripted group (container) (typed FeaturePython)
  n = 3
  ref = O_element
FEATURE [App::DocumentObjectGroupPython] G4_LITHIUM_CARBONATE  # scripted group (container) (typed FeaturePython)
  Dunit = g/cm3
  Dvalue = 2.11
  Group = -> [Li_element002,C_element055,O_element054]
  conduct = 2
  density = 1
  expand = 3
  formula = G4_LITHIUM_CARBONATE
  name = G4_LITHIUM_CARBONATE
  specific = 4
FEATURE [App::DocumentObjectGroupPython] Li_element003  label="Li_element : 003"  # scripted group (container) (typed FeaturePython)
  n = 1
  ref = Li_element
FEATURE [App::DocumentObjectGroupPython] F_element012  label="F_element : 004"  # scripted group (container) (typed FeaturePython)
  n = 1
  ref = F_element
FEATURE [App::DocumentObjectGroupPython] G4_LITHIUM_FLUORIDE  # scripted group (container) (typed FeaturePython)
  Dunit = g/cm3
  Dvalue = 2.635
  Group = -> [Li_element003,F_element012]
  conduct = 2
  density = 1
  expand = 3
  formula = G4_LITHIUM_FLUORIDE
  name = G4_LITHIUM_FLUORIDE
  specific = 4
FEATURE [App::DocumentObjectGroupPython] Li_element004  label="Li_element : 004"  # scripted group (container) (typed FeaturePython)
  n = 1
  ref = Li_element
FEATURE [App::DocumentObjectGroupPython] H_element050  label="H_element : 027"  # scripted group (container) (typed FeaturePython)
  n = 1
  ref = H_element
FEATURE [App::DocumentObjectGroupPython] G4_LITHIUM_HYDRIDE  # scripted group (container) (typed FeaturePython)
  Dunit = g/cm3
  Dvalue = 0.82
  Group = -> [Li_element004,H_element050]
  conduct = 2
  density = 1
  expand = 3
  formula = G4_LITHIUM_HYDRIDE
  name = G4_LITHIUM_HYDRIDE
  specific = 4
FEATURE [App::DocumentObjectGroupPython] Li_element005  label="Li_element : 005"  # scripted group (container) (typed FeaturePython)
  n = 1
  ref = Li_element
FEATURE [App::DocumentObjectGroupPython] I_element003  label="I_element : 002"  # scripted group (container) (typed FeaturePython)
  n = 1
  ref = I_element
FEATURE [App::DocumentObjectGroupPython] G4_LITHIUM_IODIDE  # scripted group (container) (typed FeaturePython)
  Dunit = g/cm3
  Dvalue = 3.494
  Group = -> [Li_element005,I_element003]
  conduct = 2
  density = 1
  expand = 3
  formula = G4_LITHIUM_IODIDE
  name = G4_LITHIUM_IODIDE
  specific = 4
FEATURE [App::DocumentObjectGroupPython] Li_element006  label="Li_element : 006"  # scripted group (container) (typed FeaturePython)
  n = 2
  ref = Li_element
FEATURE [App::DocumentObjectGroupPython] O_element055  label="O_element : 029"  # scripted group (container) (typed FeaturePython)
  n = 1
  ref = O_element
FEATURE [App::DocumentObjectGroupPython] G4_LITHIUM_OXIDE  # scripted group (container) (typed FeaturePython)
  Dunit = g/cm3
  Dvalue = 2.013
  Group = -> [Li_element006,O_element055]
  conduct = 2
  density = 1
  expand = 3
  formula = G4_LITHIUM_OXIDE
  name = G4_LITHIUM_OXIDE
  specific = 4
FEATURE [App::DocumentObjectGroupPython] Li_element007  label="Li_element : 007"  # scripted group (container) (typed FeaturePython)
  n = 2
  ref = Li_element
FEATURE [App::DocumentObjectGroupPython] B_element005  label="B_element : 005"  # scripted group (container) (typed FeaturePython)
  n = 4
  ref = B_element
FEATURE [App::DocumentObjectGroupPython] O_element056  label="O_element : 7"  # scripted group (container) (typed FeaturePython)
  n = 7
  ref = O_element
FEATURE [App::DocumentObjectGroupPython] G4_LITHIUM_TETRABORATE  # scripted group (container) (typed FeaturePython)
  Dunit = g/cm3
  Dvalue = 2.44
  Group = -> [Li_element007,B_element005,O_element056]
  conduct = 2
  density = 1
  expand = 3
  formula = G4_LITHIUM_TETRABORATE
  name = G4_LITHIUM_TETRABORATE
  specific = 4
FEATURE [App::DocumentObjectGroupPython] H_element051  label="H_element : 0.105"  # scripted group (container) (typed FeaturePython)
  n = 0.105
FEATURE [App::DocumentObjectGroupPython] C_element056  label="C_element : 0.083"  # scripted group (container) (typed FeaturePython)
  n = 0.083
FEATURE [App::DocumentObjectGroupPython] N_element023  label="N_element : 0.023"  # scripted group (container) (typed FeaturePython)
  n = 0.023
FEATURE [App::DocumentObjectGroupPython] O_element057  label="O_element : 0.779"  # scripted group (container) (typed FeaturePython)
  n = 0.779
FEATURE [App::DocumentObjectGroupPython] Na_element010  label="Na_element : 0.097"  # scripted group (container) (typed FeaturePython)
  n = 0.002
FEATURE [App::DocumentObjectGroupPython] P_element006  label="P_element : 0.105"  # scripted group (container) (typed FeaturePython)
  n = 0.001
FEATURE [App::DocumentObjectGroupPython] S_element016  label="S_element : 0.017"  # scripted group (container) (typed FeaturePython)
  n = 0.002
FEATURE [App::DocumentObjectGroupPython] Cl_element014  label="Cl_element : 0.587"  # scripted group (container) (typed FeaturePython)
  n = 0.003
FEATURE [App::DocumentObjectGroupPython] K_element005  label="K_element : 0.015"  # scripted group (container) (typed FeaturePython)
  n = 0.002
FEATURE [App::DocumentObjectGroupPython] G4_LUNG_ICRP  # scripted group (container) (typed FeaturePython)
  Dunit = g/cm3
  Dvalue = 1.04
  Group = -> [H_element051,C_element056,N_element023,O_element057,Na_element010,P_element006,S_element016,Cl_element014,K_element005]
  conduct = 2
  density = 1
  expand = 3
  formula = G4_LUNG_ICRP
  name = G4_LUNG_ICRP
  specific = 4
FEATURE [App::DocumentObjectGroupPython] H_element052  label="H_element : 0.116"  # scripted group (container) (typed FeaturePython)
  n = 0.114318
FEATURE [App::DocumentObjectGroupPython] C_element057  label="C_element : 0.656"  # scripted group (container) (typed FeaturePython)
  n = 0.655824
FEATURE [App::DocumentObjectGroupPython] O_element058  label="O_element : 0.092"  # scripted group (container) (typed FeaturePython)
  n = 0.0921831
FEATURE [App::DocumentObjectGroupPython] Mg_element004  label="Mg_element : 0.135"  # scripted group (container) (typed FeaturePython)
  n = 0.134792
FEATURE [App::DocumentObjectGroupPython] Ca_element013  label="Ca_element : 0.003"  # scripted group (container) (typed FeaturePython)
  n = 0.002883
FEATURE [App::DocumentObjectGroupPython] G4_M3_WAX  # scripted group (container) (typed FeaturePython)
  Dunit = g/cm3
  Dvalue = 1.05
  Group = -> [H_element052,C_element057,O_element058,Mg_element004,Ca_element013]
  conduct = 2
  density = 1
  expand = 3
  formula = G4_M3_WAX
  name = G4_M3_WAX
  specific = 4
FEATURE [App::DocumentObjectGroupPython] Mg_element005  label="Mg_element : 1"  # scripted group (container) (typed FeaturePython)
  n = 1
  ref = Mg_element
FEATURE [App::DocumentObjectGroupPython] C_element058  label="C_element : 031"  # scripted group (container) (typed FeaturePython)
  n = 1
  ref = C_element
FEATURE [App::DocumentObjectGroupPython] O_element059  label="O_element : 030"  # scripted group (container) (typed FeaturePython)
  n = 3
  ref = O_element
FEATURE [App::DocumentObjectGroupPython] G4_MAGNESIUM_CARBONATE  # scripted group (container) (typed FeaturePython)
  Dunit = g/cm3
  Dvalue = 2.958
  Group = -> [Mg_element005,C_element058,O_element059]
  conduct = 2
  density = 1
  expand = 3
  formula = G4_MAGNESIUM_CARBONATE
  name = G4_MAGNESIUM_CARBONATE
  specific = 4
FEATURE [App::DocumentObjectGroupPython] Mg_element006  label="Mg_element : 002"  # scripted group (container) (typed FeaturePython)
  n = 1
  ref = Mg_element
FEATURE [App::DocumentObjectGroupPython] F_element013  label="F_element : 005"  # scripted group (container) (typed FeaturePython)
  n = 2
  ref = F_element
FEATURE [App::DocumentObjectGroupPython] G4_MAGNESIUM_FLUORIDE  # scripted group (container) (typed FeaturePython)
  Dunit = g/cm3
  Dvalue = 3
  Group = -> [Mg_element006,F_element013]
  conduct = 2
  density = 1
  expand = 3
  formula = G4_MAGNESIUM_FLUORIDE
  name = G4_MAGNESIUM_FLUORIDE
  specific = 4
FEATURE [App::DocumentObjectGroupPython] Mg_element007  label="Mg_element : 003"  # scripted group (container) (typed FeaturePython)
  n = 1
  ref = Mg_element
FEATURE [App::DocumentObjectGroupPython] O_element060  label="O_element : 031"  # scripted group (container) (typed FeaturePython)
  n = 1
  ref = O_element
FEATURE [App::DocumentObjectGroupPython] G4_MAGNESIUM_OXIDE  # scripted group (container) (typed FeaturePython)
  Dunit = g/cm3
  Dvalue = 3.58
  Group = -> [Mg_element007,O_element060]
  conduct = 2
  density = 1
  expand = 3
  formula = G4_MAGNESIUM_OXIDE
  name = G4_MAGNESIUM_OXIDE
  specific = 4
FEATURE [App::DocumentObjectGroupPython] Mg_element008  label="Mg_element : 004"  # scripted group (container) (typed FeaturePython)
  n = 1
  ref = Mg_element
FEATURE [App::DocumentObjectGroupPython] B_element006  label="B_element : 006"  # scripted group (container) (typed FeaturePython)
  n = 4
  ref = B_element
FEATURE [App::DocumentObjectGroupPython] O_element061  label="O_element : 032"  # scripted group (container) (typed FeaturePython)
  n = 7
  ref = O_element
FEATURE [App::DocumentObjectGroupPython] G4_MAGNESIUM_TETRABORATE  # scripted group (container) (typed FeaturePython)
  Dunit = g/cm3
  Dvalue = 2.53
  Group = -> [Mg_element008,B_element006,O_element061]
  conduct = 2
  density = 1
  expand = 3
  formula = G4_MAGNESIUM_TETRABORATE
  name = G4_MAGNESIUM_TETRABORATE
  specific = 4
FEATURE [App::DocumentObjectGroupPython] Hg_element001  label="Hg_element : 1"  # scripted group (container) (typed FeaturePython)
  n = 1
  ref = Hg_element
FEATURE [App::DocumentObjectGroupPython] I_element004  label="I_element : 2"  # scripted group (container) (typed FeaturePython)
  n = 2
  ref = I_element
FEATURE [App::DocumentObjectGroupPython] G4_MERCURIC_IODIDE  # scripted group (container) (typed FeaturePython)
  Dunit = g/cm3
  Dvalue = 6.36
  Group = -> [Hg_element001,I_element004]
  conduct = 2
  density = 1
  expand = 3
  formula = G4_MERCURIC_IODIDE
  name = G4_MERCURIC_IODIDE
  specific = 4
FEATURE [App::DocumentObjectGroupPython] C_element059  label="C_element : 032"  # scripted group (container) (typed FeaturePython)
  n = 1
  ref = C_element
FEATURE [App::DocumentObjectGroupPython] H_element053  label="H_element : 028"  # scripted group (container) (typed FeaturePython)
  n = 4
  ref = H_element
FEATURE [App::DocumentObjectGroupPython] G4_METHANE  # scripted group (container) (typed FeaturePython)
  Dunit = g/cm3
  Dvalue = 0.000667151
  Group = -> [C_element059,H_element053]
  conduct = 2
  density = 1
  expand = 3
  formula = G4_METHANE
  name = G4_METHANE
  specific = 4
FEATURE [App::DocumentObjectGroupPython] C_element060  label="C_element : 033"  # scripted group (container) (typed FeaturePython)
  n = 1
  ref = C_element
FEATURE [App::DocumentObjectGroupPython] H_element054  label="H_element : 029"  # scripted group (container) (typed FeaturePython)
  n = 4
  ref = H_element
FEATURE [App::DocumentObjectGroupPython] O_element062  label="O_element : 033"  # scripted group (container) (typed FeaturePython)
  n = 1
  ref = O_element
FEATURE [App::DocumentObjectGroupPython] G4_METHANOL  # scripted group (container) (typed FeaturePython)
  Dunit = g/cm3
  Dvalue = 0.7914
  Group = -> [C_element060,H_element054,O_element062]
  conduct = 2
  density = 1
  expand = 3
  formula = G4_METHANOL
  name = G4_METHANOL
  specific = 4
FEATURE [App::DocumentObjectGroupPython] H_element055  label="H_element : 0.134"  # scripted group (container) (typed FeaturePython)
  n = 0.13404
FEATURE [App::DocumentObjectGroupPython] C_element061  label="C_element : 0.778"  # scripted group (container) (typed FeaturePython)
  n = 0.77796
FEATURE [App::DocumentObjectGroupPython] O_element063  label="O_element : 0.035"  # scripted group (container) (typed FeaturePython)
  n = 0.03502
FEATURE [App::DocumentObjectGroupPython] Mg_element009  label="Mg_element : 0.039"  # scripted group (container) (typed FeaturePython)
  n = 0.038594
FEATURE [App::DocumentObjectGroupPython] Ti_element002  label="Ti_element : 0.014"  # scripted group (container) (typed FeaturePython)
  n = 0.014386
FEATURE [App::DocumentObjectGroupPython] G4_MIX_D_WAX  # scripted group (container) (typed FeaturePython)
  Dunit = g/cm3
  Dvalue = 0.99
  Group = -> [H_element055,C_element061,O_element063,Mg_element009,Ti_element002]
  conduct = 2
  density = 1
  expand = 3
  formula = G4_MIX_D_WAX
  name = G4_MIX_D_WAX
  specific = 4
FEATURE [App::DocumentObjectGroupPython] H_element056  label="H_element : 0.135"  # scripted group (container) (typed FeaturePython)
  n = 0.081192
FEATURE [App::DocumentObjectGroupPython] C_element062  label="C_element : 0.583"  # scripted group (container) (typed FeaturePython)
  n = 0.583442
FEATURE [App::DocumentObjectGroupPython] N_element024  label="N_element : 0.018"  # scripted group (container) (typed FeaturePython)
  n = 0.017798
FEATURE [App::DocumentObjectGroupPython] O_element064  label="O_element : 0.186"  # scripted group (container) (typed FeaturePython)
  n = 0.186381
FEATURE [App::DocumentObjectGroupPython] Mg_element010  label="Mg_element : 0.130"  # scripted group (container) (typed FeaturePython)
  n = 0.130287
FEATURE [App::DocumentObjectGroupPython] Cl_element015  label="Cl_element : 0.588"  # scripted group (container) (typed FeaturePython)
  n = 0.0009
FEATURE [App::DocumentObjectGroupPython] G4_MS20_TISSUE  # scripted group (container) (typed FeaturePython)
  Dunit = g/cm3
  Dvalue = 1
  Group = -> [H_element056,C_element062,N_element024,O_element064,Mg_element010,Cl_element015]
  conduct = 2
  density = 1
  expand = 3
  formula = G4_MS20_TISSUE
  name = G4_MS20_TISSUE
  specific = 4
FEATURE [App::DocumentObjectGroupPython] H_element057  label="H_element : 0.136"  # scripted group (container) (typed FeaturePython)
  n = 0.102
FEATURE [App::DocumentObjectGroupPython] C_element063  label="C_element : 0.143"  # scripted group (container) (typed FeaturePython)
  n = 0.143
FEATURE [App::DocumentObjectGroupPython] N_element025  label="N_element : 0.034"  # scripted group (container) (typed FeaturePython)
  n = 0.034
FEATURE [App::DocumentObjectGroupPython] O_element065  label="O_element : 0.710"  # scripted group (container) (typed FeaturePython)
  n = 0.71
FEATURE [App::DocumentObjectGroupPython] Na_element011  label="Na_element : 0.098"  # scripted group (container) (typed FeaturePython)
  n = 0.001
FEATURE [App::DocumentObjectGroupPython] P_element007  label="P_element : 0.002"  # scripted group (container) (typed FeaturePython)
  n = 0.002
FEATURE [App::DocumentObjectGroupPython] S_element017  label="S_element : 0.018"  # scripted group (container) (typed FeaturePython)
  n = 0.003
FEATURE [App::DocumentObjectGroupPython] Cl_element016  label="Cl_element : 0.589"  # scripted group (container) (typed FeaturePython)
  n = 0.001
FEATURE [App::DocumentObjectGroupPython] K_element006  label="K_element : 0.004"  # scripted group (container) (typed FeaturePython)
  n = 0.004
FEATURE [App::DocumentObjectGroupPython] G4_MUSCLE_SKELETAL_ICRP  # scripted group (container) (typed FeaturePython)
  Dunit = g/cm3
  Dvalue = 1.05
  Group = -> [H_element057,C_element063,N_element025,O_element065,Na_element011,P_element007,S_element017,Cl_element016,K_element006]
  conduct = 2
  density = 1
  expand = 3
  formula = G4_MUSCLE_SKELETAL_ICRP
  name = G4_MUSCLE_SKELETAL_ICRP
  specific = 4
FEATURE [App::DocumentObjectGroupPython] H_element058  label="H_element : 0.137"  # scripted group (container) (typed FeaturePython)
  n = 0.102102
FEATURE [App::DocumentObjectGroupPython] C_element064  label="C_element : 0.123"  # scripted group (container) (typed FeaturePython)
  n = 0.123123
FEATURE [App::DocumentObjectGroupPython] N_element026  label="N_element : 0.756"  # scripted group (container) (typed FeaturePython)
  n = 0.035035
FEATURE [App::DocumentObjectGroupPython] O_element066  label="O_element : 0.730"  # scripted group (container) (typed FeaturePython)
  n = 0.72973
FEATURE [App::DocumentObjectGroupPython] Na_element012  label="Na_element : 0.099"  # scripted group (container) (typed FeaturePython)
  n = 0.001001
FEATURE [App::DocumentObjectGroupPython] P_element008  label="P_element : 0.106"  # scripted group (container) (typed FeaturePython)
  n = 0.002002
FEATURE [App::DocumentObjectGroupPython] S_element018  label="S_element : 0.019"  # scripted group (container) (typed FeaturePython)
  n = 0.004004
FEATURE [App::DocumentObjectGroupPython] K_element007  label="K_element : 0.016"  # scripted group (container) (typed FeaturePython)
  n = 0.003003
FEATURE [App::DocumentObjectGroupPython] G4_MUSCLE_STRIATED_ICRU  # scripted group (container) (typed FeaturePython)
  Dunit = g/cm3
  Dvalue = 1.04
  Group = -> [H_element058,C_element064,N_element026,O_element066,Na_element012,P_element008,S_element018,K_element007]
  conduct = 2
  density = 1
  expand = 3
  formula = G4_MUSCLE_STRIATED_ICRU
  name = G4_MUSCLE_STRIATED_ICRU
  specific = 4
FEATURE [App::DocumentObjectGroupPython] H_element059  label="H_element : 0.098"  # scripted group (container) (typed FeaturePython)
  n = 0.0982341
FEATURE [App::DocumentObjectGroupPython] C_element065  label="C_element : 0.156"  # scripted group (container) (typed FeaturePython)
  n = 0.156214
FEATURE [App::DocumentObjectGroupPython] N_element027  label="N_element : 0.757"  # scripted group (container) (typed FeaturePython)
  n = 0.035451
FEATURE [App::DocumentObjectGroupPython] O_element067  label="O_element : 0.880"  # scripted group (container) (typed FeaturePython)
  n = 0.710101
FEATURE [App::DocumentObjectGroupPython] G4_MUSCLE_WITH_SUCROSE  # scripted group (container) (typed FeaturePython)
  Dunit = g/cm3
  Dvalue = 1.11
  Group = -> [H_element059,C_element065,N_element027,O_element067]
  conduct = 2
  density = 1
  expand = 3
  formula = G4_MUSCLE_WITH_SUCROSE
  name = G4_MUSCLE_WITH_SUCROSE
  specific = 4
FEATURE [App::DocumentObjectGroupPython] H_element060  label="H_element : 0.138"  # scripted group (container) (typed FeaturePython)
  n = 0.101969
FEATURE [App::DocumentObjectGroupPython] C_element066  label="C_element : 0.120"  # scripted group (container) (typed FeaturePython)
  n = 0.120058
FEATURE [App::DocumentObjectGroupPython] N_element028  label="N_element : 0.758"  # scripted group (container) (typed FeaturePython)
  n = 0.035451
FEATURE [App::DocumentObjectGroupPython] O_element068  label="O_element : 0.743"  # scripted group (container) (typed FeaturePython)
  n = 0.742522
FEATURE [App::DocumentObjectGroupPython] G4_MUSCLE_WITHOUT_SUCROSE  # scripted group (container) (typed FeaturePython)
  Dunit = g/cm3
  Dvalue = 1.07
  Group = -> [H_element060,C_element066,N_element028,O_element068]
  conduct = 2
  density = 1
  expand = 3
  formula = G4_MUSCLE_WITHOUT_SUCROSE
  name = G4_MUSCLE_WITHOUT_SUCROSE
  specific = 4
FEATURE [App::DocumentObjectGroupPython] C_element067  label="C_element : 10"  # scripted group (container) (typed FeaturePython)
  n = 10
  ref = C_element
FEATURE [App::DocumentObjectGroupPython] H_element061  label="H_element : 030"  # scripted group (container) (typed FeaturePython)
  n = 8
  ref = H_element
FEATURE [App::DocumentObjectGroupPython] G4_NAPHTHALENE  # scripted group (container) (typed FeaturePython)
  Dunit = g/cm3
  Dvalue = 1.145
  Group = -> [C_element067,H_element061]
  conduct = 2
  density = 1
  expand = 3
  formula = G4_NAPHTHALENE
  name = G4_NAPHTHALENE
  specific = 4
FEATURE [App::DocumentObjectGroupPython] C_element068  label="C_element : 034"  # scripted group (container) (typed FeaturePython)
  n = 6
  ref = C_element
FEATURE [App::DocumentObjectGroupPython] H_element062  label="H_element : 031"  # scripted group (container) (typed FeaturePython)
  n = 5
  ref = H_element
FEATURE [App::DocumentObjectGroupPython] N_element029  label="N_element : 012"  # scripted group (container) (typed FeaturePython)
  n = 1
  ref = N_element
FEATURE [App::DocumentObjectGroupPython] O_element069  label="O_element : 034"  # scripted group (container) (typed FeaturePython)
  n = 2
  ref = O_element
FEATURE [App::DocumentObjectGroupPython] G4_NITROBENZENE  # scripted group (container) (typed FeaturePython)
  Dunit = g/cm3
  Dvalue = 1.19867
  Group = -> [C_element068,H_element062,N_element029,O_element069]
  conduct = 2
  density = 1
  expand = 3
  formula = G4_NITROBENZENE
  name = G4_NITROBENZENE
  specific = 4
FEATURE [App::DocumentObjectGroupPython] N_element030  label="N_element : 013"  # scripted group (container) (typed FeaturePython)
  n = 2
  ref = N_element
FEATURE [App::DocumentObjectGroupPython] O_element070  label="O_element : 035"  # scripted group (container) (typed FeaturePython)
  n = 1
  ref = O_element
FEATURE [App::DocumentObjectGroupPython] G4_NITROUS_OXIDE  # scripted group (container) (typed FeaturePython)
  Dunit = g/cm3
  Dvalue = 0.00183094
  Group = -> [N_element030,O_element070]
  conduct = 2
  density = 1
  expand = 3
  formula = G4_NITROUS_OXIDE
  name = G4_NITROUS_OXIDE
  specific = 4
FEATURE [App::DocumentObjectGroupPython] H_element063  label="H_element : 0.104"  # scripted group (container) (typed FeaturePython)
  n = 0.103509
FEATURE [App::DocumentObjectGroupPython] C_element069  label="C_element : 0.648"  # scripted group (container) (typed FeaturePython)
  n = 0.648416
FEATURE [App::DocumentObjectGroupPython] N_element031  label="N_element : 0.100"  # scripted group (container) (typed FeaturePython)
  n = 0.0995361
FEATURE [App::DocumentObjectGroupPython] O_element071  label="O_element : 0.149"  # scripted group (container) (typed FeaturePython)
  n = 0.148539
FEATURE [App::DocumentObjectGroupPython] G4_NYLON_8062  label="G4_NYLON-8062"  # scripted group (container) (typed FeaturePython)
  Dunit = g/cm3
  Dvalue = 1.08
  Group = -> [H_element063,C_element069,N_element031,O_element071]
  conduct = 2
  density = 1
  expand = 3
  formula = G4_NYLON-8062
  name = G4_NYLON-8062
  specific = 4
FEATURE [App::DocumentObjectGroupPython] C_element070  label="C_element : 035"  # scripted group (container) (typed FeaturePython)
  n = 6
  ref = C_element
FEATURE [App::DocumentObjectGroupPython] H_element064  label="H_element : 11"  # scripted group (container) (typed FeaturePython)
  n = 11
  ref = H_element
FEATURE [App::DocumentObjectGroupPython] N_element032  label="N_element : 014"  # scripted group (container) (typed FeaturePython)
  n = 1
  ref = N_element
FEATURE [App::DocumentObjectGroupPython] O_element072  label="O_element : 036"  # scripted group (container) (typed FeaturePython)
  n = 1
  ref = O_element
FEATURE [App::DocumentObjectGroupPython] G4_NYLON_6_6  label="G4_NYLON-6-6"  # scripted group (container) (typed FeaturePython)
  Dunit = g/cm3
  Dvalue = 1.14
  Group = -> [C_element070,H_element064,N_element032,O_element072]
  conduct = 2
  density = 1
  expand = 3
  formula = G4_NYLON-6-6
  name = G4_NYLON-6-6
  specific = 4
FEATURE [App::DocumentObjectGroupPython] H_element065  label="H_element : 0.139"  # scripted group (container) (typed FeaturePython)
  n = 0.107062
FEATURE [App::DocumentObjectGroupPython] C_element071  label="C_element : 0.680"  # scripted group (container) (typed FeaturePython)
  n = 0.680449
FEATURE [App::DocumentObjectGroupPython] N_element033  label="N_element : 0.099"  # scripted group (container) (typed FeaturePython)
  n = 0.099189
FEATURE [App::DocumentObjectGroupPython] O_element073  label="O_element : 0.113"  # scripted group (container) (typed FeaturePython)
  n = 0.1133
FEATURE [App::DocumentObjectGroupPython] G4_NYLON_6_10  label="G4_NYLON-6-10"  # scripted group (container) (typed FeaturePython)
  Dunit = g/cm3
  Dvalue = 1.14
  Group = -> [H_element065,C_element071,N_element033,O_element073]
  conduct = 2
  density = 1
  expand = 3
  formula = G4_NYLON-6-10
  name = G4_NYLON-6-10
  specific = 4
FEATURE [App::DocumentObjectGroupPython] H_element066  label="H_element : 0.140"  # scripted group (container) (typed FeaturePython)
  n = 0.115476
FEATURE [App::DocumentObjectGroupPython] C_element072  label="C_element : 0.721"  # scripted group (container) (typed FeaturePython)
  n = 0.720818
FEATURE [App::DocumentObjectGroupPython] N_element034  label="N_element : 0.076"  # scripted group (container) (typed FeaturePython)
  n = 0.0764169
FEATURE [App::DocumentObjectGroupPython] O_element074  label="O_element : 0.087"  # scripted group (container) (typed FeaturePython)
  n = 0.0872889
FEATURE [App::DocumentObjectGroupPython] G4_NYLON_11_RILSAN  label="G4_NYLON-11_RILSAN"  # scripted group (container) (typed FeaturePython)
  Dunit = g/cm3
  Dvalue = 1.425
  Group = -> [H_element066,C_element072,N_element034,O_element074]
  conduct = 2
  density = 1
  expand = 3
  formula = G4_NYLON-11_RILSAN
  name = G4_NYLON-11_RILSAN
  specific = 4
FEATURE [App::DocumentObjectGroupPython] C_element073  label="C_element : 8"  # scripted group (container) (typed FeaturePython)
  n = 8
  ref = C_element
FEATURE [App::DocumentObjectGroupPython] H_element067  label="H_element : 18"  # scripted group (container) (typed FeaturePython)
  n = 18
  ref = H_element
FEATURE [App::DocumentObjectGroupPython] G4_OCTANE  # scripted group (container) (typed FeaturePython)
  Dunit = g/cm3
  Dvalue = 0.7026
  Group = -> [C_element073,H_element067]
  conduct = 2
  density = 1
  expand = 3
  formula = G4_OCTANE
  name = G4_OCTANE
  specific = 4
FEATURE [App::DocumentObjectGroupPython] C_element074  label="C_element : 25"  # scripted group (container) (typed FeaturePython)
  n = 25
  ref = C_element
FEATURE [App::DocumentObjectGroupPython] H_element068  label="H_element : 52"  # scripted group (container) (typed FeaturePython)
  n = 52
  ref = H_element
FEATURE [App::DocumentObjectGroupPython] G4_PARAFFIN  # scripted group (container) (typed FeaturePython)
  Dunit = g/cm3
  Dvalue = 0.93
  Group = -> [C_element074,H_element068]
  conduct = 2
  density = 1
  expand = 3
  formula = G4_PARAFFIN
  name = G4_PARAFFIN
  specific = 4
FEATURE [App::DocumentObjectGroupPython] C_element075  label="C_element : 036"  # scripted group (container) (typed FeaturePython)
  n = 5
  ref = C_element
FEATURE [App::DocumentObjectGroupPython] H_element069  label="H_element : 032"  # scripted group (container) (typed FeaturePython)
  n = 12
  ref = H_element
FEATURE [App::DocumentObjectGroupPython] G4_N_PENTANE  label="G4_N-PENTANE"  # scripted group (container) (typed FeaturePython)
  Dunit = g/cm3
  Dvalue = 0.6262
  Group = -> [C_element075,H_element069]
  conduct = 2
  density = 1
  expand = 3
  formula = G4_N-PENTANE
  name = G4_N-PENTANE
  specific = 4
FEATURE [App::DocumentObjectGroupPython] H_element070  label="H_element : 0.014"  # scripted group (container) (typed FeaturePython)
  n = 0.0141
FEATURE [App::DocumentObjectGroupPython] C_element076  label="C_element : 0.072"  # scripted group (container) (typed FeaturePython)
  n = 0.072261
FEATURE [App::DocumentObjectGroupPython] N_element035  label="N_element : 0.019"  # scripted group (container) (typed FeaturePython)
  n = 0.01932
FEATURE [App::DocumentObjectGroupPython] O_element075  label="O_element : 0.066"  # scripted group (container) (typed FeaturePython)
  n = 0.066101
FEATURE [App::DocumentObjectGroupPython] S_element019  label="S_element : 0.020"  # scripted group (container) (typed FeaturePython)
  n = 0.00189
FEATURE [App::DocumentObjectGroupPython] Br_element004  label="Br_element : 0.349"  # scripted group (container) (typed FeaturePython)
  n = 0.349103
FEATURE [App::DocumentObjectGroupPython] Ag_element001  label="Ag_element : 0.474"  # scripted group (container) (typed FeaturePython)
  n = 0.474105
FEATURE [App::DocumentObjectGroupPython] I_element005  label="I_element : 0.003"  # scripted group (container) (typed FeaturePython)
  n = 0.00312
FEATURE [App::DocumentObjectGroupPython] G4_PHOTO_EMULSION  # scripted group (container) (typed FeaturePython)
  Dunit = g/cm3
  Dvalue = 3.815
  Group = -> [H_element070,C_element076,N_element035,O_element075,S_element019,Br_element004,Ag_element001,I_element005]
  conduct = 2
  density = 1
  expand = 3
  formula = G4_PHOTO_EMULSION
  name = G4_PHOTO_EMULSION
  specific = 4
FEATURE [App::DocumentObjectGroupPython] C_element077  label="C_element : 9"  # scripted group (container) (typed FeaturePython)
  n = 9
  ref = C_element
FEATURE [App::DocumentObjectGroupPython] H_element071  label="H_element : 033"  # scripted group (container) (typed FeaturePython)
  n = 10
  ref = H_element
FEATURE [App::DocumentObjectGroupPython] G4_PLASTIC_SC_VINYLTOLUENE  # scripted group (container) (typed FeaturePython)
  Dunit = g/cm3
  Dvalue = 1.032
  Group = -> [C_element077,H_element071]
  conduct = 2
  density = 1
  expand = 3
  formula = G4_PLASTIC_SC_VINYLTOLUENE
  name = G4_PLASTIC_SC_VINYLTOLUENE
  specific = 4
FEATURE [App::DocumentObjectGroupPython] Pu_element001  label="Pu_element : 1"  # scripted group (container) (typed FeaturePython)
  n = 1
  ref = Pu_element
FEATURE [App::DocumentObjectGroupPython] O_element076  label="O_element : 037"  # scripted group (container) (typed FeaturePython)
  n = 2
  ref = O_element
FEATURE [App::DocumentObjectGroupPython] G4_PLUTONIUM_DIOXIDE  # scripted group (container) (typed FeaturePython)
  Dunit = g/cm3
  Dvalue = 11.46
  Group = -> [Pu_element001,O_element076]
  conduct = 2
  density = 1
  expand = 3
  formula = G4_PLUTONIUM_DIOXIDE
  name = G4_PLUTONIUM_DIOXIDE
  specific = 4
FEATURE [App::DocumentObjectGroupPython] C_element078  label="C_element : 037"  # scripted group (container) (typed FeaturePython)
  n = 3
  ref = C_element
FEATURE [App::DocumentObjectGroupPython] H_element072  label="H_element : 034"  # scripted group (container) (typed FeaturePython)
  n = 3
  ref = H_element
FEATURE [App::DocumentObjectGroupPython] N_element036  label="N_element : 015"  # scripted group (container) (typed FeaturePython)
  n = 1
  ref = N_element
FEATURE [App::DocumentObjectGroupPython] G4_POLYACRYLONITRILE  # scripted group (container) (typed FeaturePython)
  Dunit = g/cm3
  Dvalue = 1.17
  Group = -> [C_element078,H_element072,N_element036]
  conduct = 2
  density = 1
  expand = 3
  formula = G4_POLYACRYLONITRILE
  name = G4_POLYACRYLONITRILE
  specific = 4
FEATURE [App::DocumentObjectGroupPython] C_element079  label="C_element : 16"  # scripted group (container) (typed FeaturePython)
  n = 16
  ref = C_element
FEATURE [App::DocumentObjectGroupPython] H_element073  label="H_element : 035"  # scripted group (container) (typed FeaturePython)
  n = 14
  ref = H_element
FEATURE [App::DocumentObjectGroupPython] O_element077  label="O_element : 038"  # scripted group (container) (typed FeaturePython)
  n = 3
  ref = O_element
FEATURE [App::DocumentObjectGroupPython] G4_POLYCARBONATE  # scripted group (container) (typed FeaturePython)
  Dunit = g/cm3
  Dvalue = 1.2
  Group = -> [C_element079,H_element073,O_element077]
  conduct = 2
  density = 1
  expand = 3
  formula = G4_POLYCARBONATE
  name = G4_POLYCARBONATE
  specific = 4
FEATURE [App::DocumentObjectGroupPython] C_element080  label="C_element : 038"  # scripted group (container) (typed FeaturePython)
  n = 8
  ref = C_element
FEATURE [App::DocumentObjectGroupPython] H_element074  label="H_element : 036"  # scripted group (container) (typed FeaturePython)
  n = 7
  ref = H_element
FEATURE [App::DocumentObjectGroupPython] Cl_element017  label="Cl_element : 007"  # scripted group (container) (typed FeaturePython)
  n = 1
  ref = Cl_element
FEATURE [App::DocumentObjectGroupPython] G4_POLYCHLOROSTYRENE  # scripted group (container) (typed FeaturePython)
  Dunit = g/cm3
  Dvalue = 1.3
  Group = -> [C_element080,H_element074,Cl_element017]
  conduct = 2
  density = 1
  expand = 3
  formula = G4_POLYCHLOROSTYRENE
  name = G4_POLYCHLOROSTYRENE
  specific = 4
FEATURE [App::DocumentObjectGroupPython] C_element081  label="C_element : 039"  # scripted group (container) (typed FeaturePython)
  n = 1
  ref = C_element
FEATURE [App::DocumentObjectGroupPython] H_element075  label="H_element : 037"  # scripted group (container) (typed FeaturePython)
  n = 2
  ref = H_element
FEATURE [App::DocumentObjectGroupPython] G4_POLYETHYLENE  # scripted group (container) (typed FeaturePython)
  Dunit = g/cm3
  Dvalue = 0.94
  Group = -> [C_element081,H_element075]
  conduct = 2
  density = 1
  expand = 3
  formula = G4_POLYETHYLENE
  name = G4_POLYETHYLENE
  specific = 4
FEATURE [App::DocumentObjectGroupPython] C_element082  label="C_element : 040"  # scripted group (container) (typed FeaturePython)
  n = 10
  ref = C_element
FEATURE [App::DocumentObjectGroupPython] H_element076  label="H_element : 038"  # scripted group (container) (typed FeaturePython)
  n = 8
  ref = H_element
FEATURE [App::DocumentObjectGroupPython] O_element078  label="O_element : 039"  # scripted group (container) (typed FeaturePython)
  n = 4
  ref = O_element
FEATURE [App::DocumentObjectGroupPython] G4_MYLAR  # scripted group (container) (typed FeaturePython)
  Dunit = g/cm3
  Dvalue = 1.4
  Group = -> [C_element082,H_element076,O_element078]
  conduct = 2
  density = 1
  expand = 3
  formula = G4_MYLAR
  name = G4_MYLAR
  specific = 4
FEATURE [App::DocumentObjectGroupPython] C_element083  label="C_element : 041"  # scripted group (container) (typed FeaturePython)
  n = 5
  ref = C_element
FEATURE [App::DocumentObjectGroupPython] H_element077  label="H_element : 039"  # scripted group (container) (typed FeaturePython)
  n = 8
  ref = H_element
FEATURE [App::DocumentObjectGroupPython] O_element079  label="O_element : 040"  # scripted group (container) (typed FeaturePython)
  n = 2
  ref = O_element
FEATURE [App::DocumentObjectGroupPython] G4_PLEXIGLASS  # scripted group (container) (typed FeaturePython)
  Dunit = g/cm3
  Dvalue = 1.19
  Group = -> [C_element083,H_element077,O_element079]
  conduct = 2
  density = 1
  expand = 3
  formula = G4_PLEXIGLASS
  name = G4_PLEXIGLASS
  specific = 4
FEATURE [App::DocumentObjectGroupPython] C_element084  label="C_element : 042"  # scripted group (container) (typed FeaturePython)
  n = 1
  ref = C_element
FEATURE [App::DocumentObjectGroupPython] H_element078  label="H_element : 040"  # scripted group (container) (typed FeaturePython)
  n = 2
  ref = H_element
FEATURE [App::DocumentObjectGroupPython] O_element080  label="O_element : 041"  # scripted group (container) (typed FeaturePython)
  n = 1
  ref = O_element
FEATURE [App::DocumentObjectGroupPython] G4_POLYOXYMETHYLENE  # scripted group (container) (typed FeaturePython)
  Dunit = g/cm3
  Dvalue = 1.425
  Group = -> [C_element084,H_element078,O_element080]
  conduct = 2
  density = 1
  expand = 3
  formula = G4_POLYOXYMETHYLENE
  name = G4_POLYOXYMETHYLENE
  specific = 4
FEATURE [App::DocumentObjectGroupPython] C_element085  label="C_element : 043"  # scripted group (container) (typed FeaturePython)
  n = 2
  ref = C_element
FEATURE [App::DocumentObjectGroupPython] H_element079  label="H_element : 041"  # scripted group (container) (typed FeaturePython)
  n = 4
  ref = H_element
FEATURE [App::DocumentObjectGroupPython] G4_POLYPROPYLENE  # scripted group (container) (typed FeaturePython)
  Dunit = g/cm3
  Dvalue = 0.9
  Group = -> [C_element085,H_element079]
  conduct = 2
  density = 1
  expand = 3
  formula = G4_POLYPROPYLENE
  name = G4_POLYPROPYLENE
  specific = 4
FEATURE [App::DocumentObjectGroupPython] C_element086  label="C_element : 044"  # scripted group (container) (typed FeaturePython)
  n = 8
  ref = C_element
FEATURE [App::DocumentObjectGroupPython] H_element080  label="H_element : 042"  # scripted group (container) (typed FeaturePython)
  n = 8
  ref = H_element
FEATURE [App::DocumentObjectGroupPython] G4_POLYSTYRENE  # scripted group (container) (typed FeaturePython)
  Dunit = g/cm3
  Dvalue = 1.06
  Group = -> [C_element086,H_element080]
  conduct = 2
  density = 1
  expand = 3
  formula = G4_POLYSTYRENE
  name = G4_POLYSTYRENE
  specific = 4
FEATURE [App::DocumentObjectGroupPython] C_element087  label="C_element : 045"  # scripted group (container) (typed FeaturePython)
  n = 2
  ref = C_element
FEATURE [App::DocumentObjectGroupPython] F_element014  label="F_element : 4"  # scripted group (container) (typed FeaturePython)
  n = 4
  ref = F_element
FEATURE [App::DocumentObjectGroupPython] G4_TEFLON  # scripted group (container) (typed FeaturePython)
  Dunit = g/cm3
  Dvalue = 2.2
  Group = -> [C_element087,F_element014]
  conduct = 2
  density = 1
  expand = 3
  formula = G4_TEFLON
  name = G4_TEFLON
  specific = 4
FEATURE [App::DocumentObjectGroupPython] C_element088  label="C_element : 046"  # scripted group (container) (typed FeaturePython)
  n = 2
  ref = C_element
FEATURE [App::DocumentObjectGroupPython] F_element015  label="F_element : 006"  # scripted group (container) (typed FeaturePython)
  n = 3
  ref = F_element
FEATURE [App::DocumentObjectGroupPython] Cl_element018  label="Cl_element : 008"  # scripted group (container) (typed FeaturePython)
  n = 1
  ref = Cl_element
FEATURE [App::DocumentObjectGroupPython] G4_POLYTRIFLUOROCHLOROETHYLENE  # scripted group (container) (typed FeaturePython)
  Dunit = g/cm3
  Dvalue = 2.1
  Group = -> [C_element088,F_element015,Cl_element018]
  conduct = 2
  density = 1
  expand = 3
  formula = G4_POLYTRIFLUOROCHLOROETHYLENE
  name = G4_POLYTRIFLUOROCHLOROETHYLENE
  specific = 4
FEATURE [App::DocumentObjectGroupPython] C_element089  label="C_element : 047"  # scripted group (container) (typed FeaturePython)
  n = 4
  ref = C_element
FEATURE [App::DocumentObjectGroupPython] H_element081  label="H_element : 043"  # scripted group (container) (typed FeaturePython)
  n = 6
  ref = H_element
FEATURE [App::DocumentObjectGroupPython] O_element081  label="O_element : 042"  # scripted group (container) (typed FeaturePython)
  n = 2
  ref = O_element
FEATURE [App::DocumentObjectGroupPython] G4_POLYVINYL_ACETATE  # scripted group (container) (typed FeaturePython)
  Dunit = g/cm3
  Dvalue = 1.19
  Group = -> [C_element089,H_element081,O_element081]
  conduct = 2
  density = 1
  expand = 3
  formula = G4_POLYVINYL_ACETATE
  name = G4_POLYVINYL_ACETATE
  specific = 4
FEATURE [App::DocumentObjectGroupPython] C_element090  label="C_element : 048"  # scripted group (container) (typed FeaturePython)
  n = 2
  ref = C_element
FEATURE [App::DocumentObjectGroupPython] H_element082  label="H_element : 044"  # scripted group (container) (typed FeaturePython)
  n = 4
  ref = H_element
FEATURE [App::DocumentObjectGroupPython] O_element082  label="O_element : 043"  # scripted group (container) (typed FeaturePython)
  n = 1
  ref = O_element
FEATURE [App::DocumentObjectGroupPython] G4_POLYVINYL_ALCOHOL  # scripted group (container) (typed FeaturePython)
  Dunit = g/cm3
  Dvalue = 1.3
  Group = -> [C_element090,H_element082,O_element082]
  conduct = 2
  density = 1
  expand = 3
  formula = G4_POLYVINYL_ALCOHOL
  name = G4_POLYVINYL_ALCOHOL
  specific = 4
FEATURE [App::DocumentObjectGroupPython] C_element091  label="C_element : 049"  # scripted group (container) (typed FeaturePython)
  n = 8
  ref = C_element
FEATURE [App::DocumentObjectGroupPython] H_element083  label="H_element : 045"  # scripted group (container) (typed FeaturePython)
  n = 14
  ref = H_element
FEATURE [App::DocumentObjectGroupPython] O_element083  label="O_element : 044"  # scripted group (container) (typed FeaturePython)
  n = 2
  ref = O_element
FEATURE [App::DocumentObjectGroupPython] G4_POLYVINYL_BUTYRAL  # scripted group (container) (typed FeaturePython)
  Dunit = g/cm3
  Dvalue = 1.12
  Group = -> [C_element091,H_element083,O_element083]
  conduct = 2
  density = 1
  expand = 3
  formula = G4_POLYVINYL_BUTYRAL
  name = G4_POLYVINYL_BUTYRAL
  specific = 4
FEATURE [App::DocumentObjectGroupPython] C_element092  label="C_element : 050"  # scripted group (container) (typed FeaturePython)
  n = 2
  ref = C_element
FEATURE [App::DocumentObjectGroupPython] H_element084  label="H_element : 046"  # scripted group (container) (typed FeaturePython)
  n = 3
  ref = H_element
FEATURE [App::DocumentObjectGroupPython] Cl_element019  label="Cl_element : 009"  # scripted group (container) (typed FeaturePython)
  n = 1
  ref = Cl_element
FEATURE [App::DocumentObjectGroupPython] G4_POLYVINYL_CHLORIDE  # scripted group (container) (typed FeaturePython)
  Dunit = g/cm3
  Dvalue = 1.3
  Group = -> [C_element092,H_element084,Cl_element019]
  conduct = 2
  density = 1
  expand = 3
  formula = G4_POLYVINYL_CHLORIDE
  name = G4_POLYVINYL_CHLORIDE
  specific = 4
FEATURE [App::DocumentObjectGroupPython] C_element093  label="C_element : 051"  # scripted group (container) (typed FeaturePython)
  n = 2
  ref = C_element
FEATURE [App::DocumentObjectGroupPython] H_element085  label="H_element : 047"  # scripted group (container) (typed FeaturePython)
  n = 2
  ref = H_element
FEATURE [App::DocumentObjectGroupPython] Cl_element020  label="Cl_element : 010"  # scripted group (container) (typed FeaturePython)
  n = 2
  ref = Cl_element
FEATURE [App::DocumentObjectGroupPython] G4_POLYVINYLIDENE_CHLORIDE  # scripted group (container) (typed FeaturePython)
  Dunit = g/cm3
  Dvalue = 1.7
  Group = -> [C_element093,H_element085,Cl_element020]
  conduct = 2
  density = 1
  expand = 3
  formula = G4_POLYVINYLIDENE_CHLORIDE
  name = G4_POLYVINYLIDENE_CHLORIDE
  specific = 4
FEATURE [App::DocumentObjectGroupPython] C_element094  label="C_element : 052"  # scripted group (container) (typed FeaturePython)
  n = 2
  ref = C_element
FEATURE [App::DocumentObjectGroupPython] H_element086  label="H_element : 048"  # scripted group (container) (typed FeaturePython)
  n = 2
  ref = H_element
FEATURE [App::DocumentObjectGroupPython] F_element016  label="F_element : 007"  # scripted group (container) (typed FeaturePython)
  n = 2
  ref = F_element
FEATURE [App::DocumentObjectGroupPython] G4_POLYVINYLIDENE_FLUORIDE  # scripted group (container) (typed FeaturePython)
  Dunit = g/cm3
  Dvalue = 1.76
  Group = -> [C_element094,H_element086,F_element016]
  conduct = 2
  density = 1
  expand = 3
  formula = G4_POLYVINYLIDENE_FLUORIDE
  name = G4_POLYVINYLIDENE_FLUORIDE
  specific = 4
FEATURE [App::DocumentObjectGroupPython] C_element095  label="C_element : 053"  # scripted group (container) (typed FeaturePython)
  n = 6
  ref = C_element
FEATURE [App::DocumentObjectGroupPython] H_element087  label="H_element : 9"  # scripted group (container) (typed FeaturePython)
  n = 9
  ref = H_element
FEATURE [App::DocumentObjectGroupPython] N_element037  label="N_element : 016"  # scripted group (container) (typed FeaturePython)
  n = 1
  ref = N_element
FEATURE [App::DocumentObjectGroupPython] O_element084  label="O_element : 045"  # scripted group (container) (typed FeaturePython)
  n = 1
  ref = O_element
FEATURE [App::DocumentObjectGroupPython] G4_POLYVINYL_PYRROLIDONE  # scripted group (container) (typed FeaturePython)
  Dunit = g/cm3
  Dvalue = 1.25
  Group = -> [C_element095,H_element087,N_element037,O_element084]
  conduct = 2
  density = 1
  expand = 3
  formula = G4_POLYVINYL_PYRROLIDONE
  name = G4_POLYVINYL_PYRROLIDONE
  specific = 4
FEATURE [App::DocumentObjectGroupPython] K_element008  label="K_element : 1"  # scripted group (container) (typed FeaturePython)
  n = 1
  ref = K_element
FEATURE [App::DocumentObjectGroupPython] I_element006  label="I_element : 003"  # scripted group (container) (typed FeaturePython)
  n = 1
  ref = I_element
FEATURE [App::DocumentObjectGroupPython] G4_POTASSIUM_IODIDE  # scripted group (container) (typed FeaturePython)
  Dunit = g/cm3
  Dvalue = 3.13
  Group = -> [K_element008,I_element006]
  conduct = 2
  density = 1
  expand = 3
  formula = G4_POTASSIUM_IODIDE
  name = G4_POTASSIUM_IODIDE
  specific = 4
FEATURE [App::DocumentObjectGroupPython] K_element009  label="K_element : 2"  # scripted group (container) (typed FeaturePython)
  n = 2
  ref = K_element
FEATURE [App::DocumentObjectGroupPython] O_element085  label="O_element : 046"  # scripted group (container) (typed FeaturePython)
  n = 1
  ref = O_element
FEATURE [App::DocumentObjectGroupPython] G4_POTASSIUM_OXIDE  # scripted group (container) (typed FeaturePython)
  Dunit = g/cm3
  Dvalue = 2.32
  Group = -> [K_element009,O_element085]
  conduct = 2
  density = 1
  expand = 3
  formula = G4_POTASSIUM_OXIDE
  name = G4_POTASSIUM_OXIDE
  specific = 4
FEATURE [App::DocumentObjectGroupPython] C_element096  label="C_element : 054"  # scripted group (container) (typed FeaturePython)
  n = 3
  ref = C_element
FEATURE [App::DocumentObjectGroupPython] H_element088  label="H_element : 049"  # scripted group (container) (typed FeaturePython)
  n = 8
  ref = H_element
FEATURE [App::DocumentObjectGroupPython] G4_PROPANE  # scripted group (container) (typed FeaturePython)
  Dunit = g/cm3
  Dvalue = 0.00187939
  Group = -> [C_element096,H_element088]
  conduct = 2
  density = 1
  expand = 3
  formula = G4_PROPANE
  name = G4_PROPANE
  specific = 4
FEATURE [App::DocumentObjectGroupPython] C_element097  label="C_element : 055"  # scripted group (container) (typed FeaturePython)
  n = 3
  ref = C_element
FEATURE [App::DocumentObjectGroupPython] H_element089  label="H_element : 050"  # scripted group (container) (typed FeaturePython)
  n = 8
  ref = H_element
FEATURE [App::DocumentObjectGroupPython] G4_lPROPANE  # scripted group (container) (typed FeaturePython)
  Dunit = g/cm3
  Dvalue = 0.43
  Group = -> [C_element097,H_element089]
  conduct = 2
  density = 1
  expand = 3
  formula = G4_lPROPANE
  name = G4_lPROPANE
  specific = 4
FEATURE [App::DocumentObjectGroupPython] C_element098  label="C_element : 056"  # scripted group (container) (typed FeaturePython)
  n = 3
  ref = C_element
FEATURE [App::DocumentObjectGroupPython] H_element090  label="H_element : 051"  # scripted group (container) (typed FeaturePython)
  n = 8
  ref = H_element
FEATURE [App::DocumentObjectGroupPython] O_element086  label="O_element : 047"  # scripted group (container) (typed FeaturePython)
  n = 1
  ref = O_element
FEATURE [App::DocumentObjectGroupPython] G4_N_PROPYL_ALCOHOL  label="G4_N-PROPYL_ALCOHOL"  # scripted group (container) (typed FeaturePython)
  Dunit = g/cm3
  Dvalue = 0.8035
  Group = -> [C_element098,H_element090,O_element086]
  conduct = 2
  density = 1
  expand = 3
  formula = G4_N-PROPYL_ALCOHOL
  name = G4_N-PROPYL_ALCOHOL
  specific = 4
FEATURE [App::DocumentObjectGroupPython] C_element099  label="C_element : 057"  # scripted group (container) (typed FeaturePython)
  n = 5
  ref = C_element
FEATURE [App::DocumentObjectGroupPython] H_element091  label="H_element : 052"  # scripted group (container) (typed FeaturePython)
  n = 5
  ref = H_element
FEATURE [App::DocumentObjectGroupPython] N_element038  label="N_element : 017"  # scripted group (container) (typed FeaturePython)
  n = 1
  ref = N_element
FEATURE [App::DocumentObjectGroupPython] G4_PYRIDINE  # scripted group (container) (typed FeaturePython)
  Dunit = g/cm3
  Dvalue = 0.9819
  Group = -> [C_element099,H_element091,N_element038]
  conduct = 2
  density = 1
  expand = 3
  formula = G4_PYRIDINE
  name = G4_PYRIDINE
  specific = 4
FEATURE [App::DocumentObjectGroupPython] H_element092  label="H_element : 0.144"  # scripted group (container) (typed FeaturePython)
  n = 0.143711
FEATURE [App::DocumentObjectGroupPython] C_element100  label="C_element : 0.856"  # scripted group (container) (typed FeaturePython)
  n = 0.856289
FEATURE [App::DocumentObjectGroupPython] G4_RUBBER_BUTYL  # scripted group (container) (typed FeaturePython)
  Dunit = g/cm3
  Dvalue = 0.92
  Group = -> [H_element092,C_element100]
  conduct = 2
  density = 1
  expand = 3
  formula = G4_RUBBER_BUTYL
  name = G4_RUBBER_BUTYL
  specific = 4
FEATURE [App::DocumentObjectGroupPython] H_element093  label="H_element : 0.118"  # scripted group (container) (typed FeaturePython)
  n = 0.118371
FEATURE [App::DocumentObjectGroupPython] C_element101  label="C_element : 0.882"  # scripted group (container) (typed FeaturePython)
  n = 0.881629
FEATURE [App::DocumentObjectGroupPython] G4_RUBBER_NATURAL  # scripted group (container) (typed FeaturePython)
  Dunit = g/cm3
  Dvalue = 0.92
  Group = -> [H_element093,C_element101]
  conduct = 2
  density = 1
  expand = 3
  formula = G4_RUBBER_NATURAL
  name = G4_RUBBER_NATURAL
  specific = 4
FEATURE [App::DocumentObjectGroupPython] H_element094  label="H_element : 0.145"  # scripted group (container) (typed FeaturePython)
  n = 0.05692
FEATURE [App::DocumentObjectGroupPython] C_element102  label="C_element : 0.543"  # scripted group (container) (typed FeaturePython)
  n = 0.542646
FEATURE [App::DocumentObjectGroupPython] Cl_element021  label="Cl_element : 0.400"  # scripted group (container) (typed FeaturePython)
  n = 0.400434
FEATURE [App::DocumentObjectGroupPython] G4_RUBBER_NEOPRENE  # scripted group (container) (typed FeaturePython)
  Dunit = g/cm3
  Dvalue = 1.23
  Group = -> [H_element094,C_element102,Cl_element021]
  conduct = 2
  density = 1
  expand = 3
  formula = G4_RUBBER_NEOPRENE
  name = G4_RUBBER_NEOPRENE
  specific = 4
FEATURE [App::DocumentObjectGroupPython] Si_element006  label="Si_element : 1"  # scripted group (container) (typed FeaturePython)
  n = 1
  ref = Si_element
FEATURE [App::DocumentObjectGroupPython] O_element087  label="O_element : 048"  # scripted group (container) (typed FeaturePython)
  n = 2
  ref = O_element
FEATURE [App::DocumentObjectGroupPython] G4_SILICON_DIOXIDE  # scripted group (container) (typed FeaturePython)
  Dunit = g/cm3
  Dvalue = 2.32
  Group = -> [Si_element006,O_element087]
  conduct = 2
  density = 1
  expand = 3
  formula = G4_SILICON_DIOXIDE
  name = G4_SILICON_DIOXIDE
  specific = 4
FEATURE [App::DocumentObjectGroupPython] Ag_element002  label="Ag_element : 1"  # scripted group (container) (typed FeaturePython)
  n = 1
  ref = Ag_element
FEATURE [App::DocumentObjectGroupPython] Br_element005  label="Br_element : 003"  # scripted group (container) (typed FeaturePython)
  n = 1
  ref = Br_element
FEATURE [App::DocumentObjectGroupPython] G4_SILVER_BROMIDE  # scripted group (container) (typed FeaturePython)
  Dunit = g/cm3
  Dvalue = 6.473
  Group = -> [Ag_element002,Br_element005]
  conduct = 2
  density = 1
  expand = 3
  formula = G4_SILVER_BROMIDE
  name = G4_SILVER_BROMIDE
  specific = 4
FEATURE [App::DocumentObjectGroupPython] Ag_element003  label="Ag_element : 002"  # scripted group (container) (typed FeaturePython)
  n = 1
  ref = Ag_element
FEATURE [App::DocumentObjectGroupPython] Cl_element022  label="Cl_element : 011"  # scripted group (container) (typed FeaturePython)
  n = 1
  ref = Cl_element
FEATURE [App::DocumentObjectGroupPython] G4_SILVER_CHLORIDE  # scripted group (container) (typed FeaturePython)
  Dunit = g/cm3
  Dvalue = 5.56
  Group = -> [Ag_element003,Cl_element022]
  conduct = 2
  density = 1
  expand = 3
  formula = G4_SILVER_CHLORIDE
  name = G4_SILVER_CHLORIDE
  specific = 4
FEATURE [App::DocumentObjectGroupPython] Br_element006  label="Br_element : 0.423"  # scripted group (container) (typed FeaturePython)
  n = 0.422895
FEATURE [App::DocumentObjectGroupPython] Ag_element004  label="Ag_element : 0.574"  # scripted group (container) (typed FeaturePython)
  n = 0.573748
FEATURE [App::DocumentObjectGroupPython] I_element007  label="I_element : 0.649"  # scripted group (container) (typed FeaturePython)
  n = 0.003357
FEATURE [App::DocumentObjectGroupPython] G4_SILVER_HALIDES  # scripted group (container) (typed FeaturePython)
  Dunit = g/cm3
  Dvalue = 6.47
  Group = -> [Br_element006,Ag_element004,I_element007]
  conduct = 2
  density = 1
  expand = 3
  formula = G4_SILVER_HALIDES
  name = G4_SILVER_HALIDES
  specific = 4
FEATURE [App::DocumentObjectGroupPython] Ag_element005  label="Ag_element : 003"  # scripted group (container) (typed FeaturePython)
  n = 1
  ref = Ag_element
FEATURE [App::DocumentObjectGroupPython] I_element008  label="I_element : 004"  # scripted group (container) (typed FeaturePython)
  n = 1
  ref = I_element
FEATURE [App::DocumentObjectGroupPython] G4_SILVER_IODIDE  # scripted group (container) (typed FeaturePython)
  Dunit = g/cm3
  Dvalue = 6.01
  Group = -> [Ag_element005,I_element008]
  conduct = 2
  density = 1
  expand = 3
  formula = G4_SILVER_IODIDE
  name = G4_SILVER_IODIDE
  specific = 4
FEATURE [App::DocumentObjectGroupPython] H_element095  label="H_element : 0.100"  # scripted group (container) (typed FeaturePython)
  n = 0.1
FEATURE [App::DocumentObjectGroupPython] C_element103  label="C_element : 0.204"  # scripted group (container) (typed FeaturePython)
  n = 0.204
FEATURE [App::DocumentObjectGroupPython] N_element039  label="N_element : 0.759"  # scripted group (container) (typed FeaturePython)
  n = 0.042
FEATURE [App::DocumentObjectGroupPython] O_element088  label="O_element : 0.645"  # scripted group (container) (typed FeaturePython)
  n = 0.645
FEATURE [App::DocumentObjectGroupPython] Na_element013  label="Na_element : 0.100"  # scripted group (container) (typed FeaturePython)
  n = 0.002
FEATURE [App::DocumentObjectGroupPython] P_element009  label="P_element : 0.107"  # scripted group (container) (typed FeaturePython)
  n = 0.001
FEATURE [App::DocumentObjectGroupPython] S_element020  label="S_element : 0.021"  # scripted group (container) (typed FeaturePython)
  n = 0.002
FEATURE [App::DocumentObjectGroupPython] Cl_element023  label="Cl_element : 0.590"  # scripted group (container) (typed FeaturePython)
  n = 0.003
FEATURE [App::DocumentObjectGroupPython] K_element010  label="K_element : 0.001"  # scripted group (container) (typed FeaturePython)
  n = 0.001
FEATURE [App::DocumentObjectGroupPython] G4_SKIN_ICRP  # scripted group (container) (typed FeaturePython)
  Dunit = g/cm3
  Dvalue = 1.09
  Group = -> [H_element095,C_element103,N_element039,O_element088,Na_element013,P_element009,S_element020,Cl_element023,K_element010]
  conduct = 2
  density = 1
  expand = 3
  formula = G4_SKIN_ICRP
  name = G4_SKIN_ICRP
  specific = 4
FEATURE [App::DocumentObjectGroupPython] Na_element014  label="Na_element : 2"  # scripted group (container) (typed FeaturePython)
  n = 2
  ref = Na_element
FEATURE [App::DocumentObjectGroupPython] C_element104  label="C_element : 058"  # scripted group (container) (typed FeaturePython)
  n = 1
  ref = C_element
FEATURE [App::DocumentObjectGroupPython] O_element089  label="O_element : 049"  # scripted group (container) (typed FeaturePython)
  n = 3
  ref = O_element
FEATURE [App::DocumentObjectGroupPython] G4_SODIUM_CARBONATE  # scripted group (container) (typed FeaturePython)
  Dunit = g/cm3
  Dvalue = 2.532
  Group = -> [Na_element014,C_element104,O_element089]
  conduct = 2
  density = 1
  expand = 3
  formula = G4_SODIUM_CARBONATE
  name = G4_SODIUM_CARBONATE
  specific = 4
FEATURE [App::DocumentObjectGroupPython] Na_element015  label="Na_element : 1"  # scripted group (container) (typed FeaturePython)
  n = 1
  ref = Na_element
FEATURE [App::DocumentObjectGroupPython] I_element009  label="I_element : 005"  # scripted group (container) (typed FeaturePython)
  n = 1
  ref = I_element
FEATURE [App::DocumentObjectGroupPython] G4_SODIUM_IODIDE  # scripted group (container) (typed FeaturePython)
  Dunit = g/cm3
  Dvalue = 3.667
  Group = -> [Na_element015,I_element009]
  conduct = 2
  density = 1
  expand = 3
  formula = G4_SODIUM_IODIDE
  name = G4_SODIUM_IODIDE
  specific = 4
FEATURE [App::DocumentObjectGroupPython] Na_element016  label="Na_element : 003"  # scripted group (container) (typed FeaturePython)
  n = 2
  ref = Na_element
FEATURE [App::DocumentObjectGroupPython] O_element090  label="O_element : 050"  # scripted group (container) (typed FeaturePython)
  n = 1
  ref = O_element
FEATURE [App::DocumentObjectGroupPython] G4_SODIUM_MONOXIDE  # scripted group (container) (typed FeaturePython)
  Dunit = g/cm3
  Dvalue = 2.27
  Group = -> [Na_element016,O_element090]
  conduct = 2
  density = 1
  expand = 3
  formula = G4_SODIUM_MONOXIDE
  name = G4_SODIUM_MONOXIDE
  specific = 4
FEATURE [App::DocumentObjectGroupPython] Na_element017  label="Na_element : 004"  # scripted group (container) (typed FeaturePython)
  n = 1
  ref = Na_element
FEATURE [App::DocumentObjectGroupPython] N_element040  label="N_element : 018"  # scripted group (container) (typed FeaturePython)
  n = 1
  ref = N_element
FEATURE [App::DocumentObjectGroupPython] O_element091  label="O_element : 051"  # scripted group (container) (typed FeaturePython)
  n = 3
  ref = O_element
FEATURE [App::DocumentObjectGroupPython] G4_SODIUM_NITRATE  # scripted group (container) (typed FeaturePython)
  Dunit = g/cm3
  Dvalue = 2.261
  Group = -> [Na_element017,N_element040,O_element091]
  conduct = 2
  density = 1
  expand = 3
  formula = G4_SODIUM_NITRATE
  name = G4_SODIUM_NITRATE
  specific = 4
FEATURE [App::DocumentObjectGroupPython] C_element105  label="C_element : 059"  # scripted group (container) (typed FeaturePython)
  n = 14
  ref = C_element
FEATURE [App::DocumentObjectGroupPython] H_element096  label="H_element : 053"  # scripted group (container) (typed FeaturePython)
  n = 12
  ref = H_element
FEATURE [App::DocumentObjectGroupPython] G4_STILBENE  # scripted group (container) (typed FeaturePython)
  Dunit = g/cm3
  Dvalue = 0.9707
  Group = -> [C_element105,H_element096]
  conduct = 2
  density = 1
  expand = 3
  formula = G4_STILBENE
  name = G4_STILBENE
  specific = 4
FEATURE [App::DocumentObjectGroupPython] C_element106  label="C_element : 12"  # scripted group (container) (typed FeaturePython)
  n = 12
  ref = C_element
FEATURE [App::DocumentObjectGroupPython] H_element097  label="H_element : 22"  # scripted group (container) (typed FeaturePython)
  n = 22
  ref = H_element
FEATURE [App::DocumentObjectGroupPython] O_element092  label="O_element : 11"  # scripted group (container) (typed FeaturePython)
  n = 11
  ref = O_element
FEATURE [App::DocumentObjectGroupPython] G4_SUCROSE  # scripted group (container) (typed FeaturePython)
  Dunit = g/cm3
  Dvalue = 1.5805
  Group = -> [C_element106,H_element097,O_element092]
  conduct = 2
  density = 1
  expand = 3
  formula = G4_SUCROSE
  name = G4_SUCROSE
  specific = 4
FEATURE [App::DocumentObjectGroupPython] C_element107  label="C_element : 18"  # scripted group (container) (typed FeaturePython)
  n = 18
  ref = C_element
FEATURE [App::DocumentObjectGroupPython] H_element098  label="H_element : 054"  # scripted group (container) (typed FeaturePython)
  n = 14
  ref = H_element
FEATURE [App::DocumentObjectGroupPython] G4_TERPHENYL  # scripted group (container) (typed FeaturePython)
  Dunit = g/cm3
  Dvalue = 1.24
  Group = -> [C_element107,H_element098]
  conduct = 2
  density = 1
  expand = 3
  formula = G4_TERPHENYL
  name = G4_TERPHENYL
  specific = 4
FEATURE [App::DocumentObjectGroupPython] H_element099  label="H_element : 0.146"  # scripted group (container) (typed FeaturePython)
  n = 0.106
FEATURE [App::DocumentObjectGroupPython] C_element108  label="C_element : 0.883"  # scripted group (container) (typed FeaturePython)
  n = 0.099
FEATURE [App::DocumentObjectGroupPython] N_element041  label="N_element : 0.020"  # scripted group (container) (typed FeaturePython)
  n = 0.02
FEATURE [App::DocumentObjectGroupPython] O_element093  label="O_element : 0.766"  # scripted group (container) (typed FeaturePython)
  n = 0.766
FEATURE [App::DocumentObjectGroupPython] Na_element018  label="Na_element : 0.101"  # scripted group (container) (typed FeaturePython)
  n = 0.002
FEATURE [App::DocumentObjectGroupPython] P_element010  label="P_element : 0.108"  # scripted group (container) (typed FeaturePython)
  n = 0.001
FEATURE [App::DocumentObjectGroupPython] S_element021  label="S_element : 0.022"  # scripted group (container) (typed FeaturePython)
  n = 0.002
FEATURE [App::DocumentObjectGroupPython] Cl_element024  label="Cl_element : 0.002"  # scripted group (container) (typed FeaturePython)
  n = 0.002
FEATURE [App::DocumentObjectGroupPython] K_element011  label="K_element : 0.017"  # scripted group (container) (typed FeaturePython)
  n = 0.002
FEATURE [App::DocumentObjectGroupPython] G4_TESTIS_ICRP  # scripted group (container) (typed FeaturePython)
  Dunit = g/cm3
  Dvalue = 1.04
  Group = -> [H_element099,C_element108,N_element041,O_element093,Na_element018,P_element010,S_element021,Cl_element024,K_element011]
  conduct = 2
  density = 1
  expand = 3
  formula = G4_TESTIS_ICRP
  name = G4_TESTIS_ICRP
  specific = 4
FEATURE [App::DocumentObjectGroupPython] C_element109  label="C_element : 060"  # scripted group (container) (typed FeaturePython)
  n = 2
  ref = C_element
FEATURE [App::DocumentObjectGroupPython] Cl_element025  label="Cl_element : 012"  # scripted group (container) (typed FeaturePython)
  n = 4
  ref = Cl_element
FEATURE [App::DocumentObjectGroupPython] G4_TETRACHLOROETHYLENE  # scripted group (container) (typed FeaturePython)
  Dunit = g/cm3
  Dvalue = 1.625
  Group = -> [C_element109,Cl_element025]
  conduct = 2
  density = 1
  expand = 3
  formula = G4_TETRACHLOROETHYLENE
  name = G4_TETRACHLOROETHYLENE
  specific = 4
FEATURE [App::DocumentObjectGroupPython] Tl_element001  label="Tl_element : 1"  # scripted group (container) (typed FeaturePython)
  n = 1
  ref = Tl_element
FEATURE [App::DocumentObjectGroupPython] Cl_element026  label="Cl_element : 013"  # scripted group (container) (typed FeaturePython)
  n = 1
  ref = Cl_element
FEATURE [App::DocumentObjectGroupPython] G4_THALLIUM_CHLORIDE  # scripted group (container) (typed FeaturePython)
  Dunit = g/cm3
  Dvalue = 7.004
  Group = -> [Tl_element001,Cl_element026]
  conduct = 2
  density = 1
  expand = 3
  formula = G4_THALLIUM_CHLORIDE
  name = G4_THALLIUM_CHLORIDE
  specific = 4
FEATURE [App::DocumentObjectGroupPython] H_element100  label="H_element : 0.147"  # scripted group (container) (typed FeaturePython)
  n = 0.105
FEATURE [App::DocumentObjectGroupPython] C_element110  label="C_element : 0.256"  # scripted group (container) (typed FeaturePython)
  n = 0.256
FEATURE [App::DocumentObjectGroupPython] N_element042  label="N_element : 0.760"  # scripted group (container) (typed FeaturePython)
  n = 0.027
FEATURE [App::DocumentObjectGroupPython] O_element094  label="O_element : 0.602"  # scripted group (container) (typed FeaturePython)
  n = 0.602
FEATURE [App::DocumentObjectGroupPython] Na_element019  label="Na_element : 0.102"  # scripted group (container) (typed FeaturePython)
  n = 0.001
FEATURE [App::DocumentObjectGroupPython] P_element011  label="P_element : 0.109"  # scripted group (container) (typed FeaturePython)
  n = 0.002
FEATURE [App::DocumentObjectGroupPython] S_element022  label="S_element : 0.023"  # scripted group (container) (typed FeaturePython)
  n = 0.003
FEATURE [App::DocumentObjectGroupPython] Cl_element027  label="Cl_element : 0.591"  # scripted group (container) (typed FeaturePython)
  n = 0.002
FEATURE [App::DocumentObjectGroupPython] K_element012  label="K_element : 0.018"  # scripted group (container) (typed FeaturePython)
  n = 0.002
FEATURE [App::DocumentObjectGroupPython] G4_TISSUE_SOFT_ICRP  # scripted group (container) (typed FeaturePython)
  Dunit = g/cm3
  Dvalue = 1.03
  Group = -> [H_element100,C_element110,N_element042,O_element094,Na_element019,P_element011,S_element022,Cl_element027,K_element012]
  conduct = 2
  density = 1
  expand = 3
  formula = G4_TISSUE_SOFT_ICRP
  name = G4_TISSUE_SOFT_ICRP
  specific = 4
FEATURE [App::DocumentObjectGroupPython] H_element101  label="H_element : 0.148"  # scripted group (container) (typed FeaturePython)
  n = 0.101
FEATURE [App::DocumentObjectGroupPython] C_element111  label="C_element : 0.111"  # scripted group (container) (typed FeaturePython)
  n = 0.111
FEATURE [App::DocumentObjectGroupPython] N_element043  label="N_element : 0.026"  # scripted group (container) (typed FeaturePython)
  n = 0.026
FEATURE [App::DocumentObjectGroupPython] O_element095  label="O_element : 0.762"  # scripted group (container) (typed FeaturePython)
  n = 0.762
FEATURE [App::DocumentObjectGroupPython] G4_TISSUE_SOFT_ICRU_4  label="G4_TISSUE_SOFT_ICRU-4"  # scripted group (container) (typed FeaturePython)
  Dunit = g/cm3
  Dvalue = 1
  Group = -> [H_element101,C_element111,N_element043,O_element095]
  conduct = 2
  density = 1
  expand = 3
  formula = G4_TISSUE_SOFT_ICRU-4
  name = G4_TISSUE_SOFT_ICRU-4
  specific = 4
FEATURE [App::DocumentObjectGroupPython] H_element102  label="H_element : 0.149"  # scripted group (container) (typed FeaturePython)
  n = 0.101869
FEATURE [App::DocumentObjectGroupPython] C_element112  label="C_element : 0.456"  # scripted group (container) (typed FeaturePython)
  n = 0.456179
FEATURE [App::DocumentObjectGroupPython] N_element044  label="N_element : 0.761"  # scripted group (container) (typed FeaturePython)
  n = 0.035172
FEATURE [App::DocumentObjectGroupPython] O_element096  label="O_element : 0.407"  # scripted group (container) (typed FeaturePython)
  n = 0.40678
FEATURE [App::DocumentObjectGroupPython] G4_TISSUE_METHANE  label="G4_TISSUE-METHANE"  # scripted group (container) (typed FeaturePython)
  Dunit = g/cm3
  Dvalue = 0.00106409
  Group = -> [H_element102,C_element112,N_element044,O_element096]
  conduct = 2
  density = 1
  expand = 3
  formula = G4_TISSUE-METHANE
  name = G4_TISSUE-METHANE
  specific = 4
FEATURE [App::DocumentObjectGroupPython] H_element103  label="H_element : 0.103"  # scripted group (container) (typed FeaturePython)
  n = 0.102672
FEATURE [App::DocumentObjectGroupPython] C_element113  label="C_element : 0.569"  # scripted group (container) (typed FeaturePython)
  n = 0.56894
FEATURE [App::DocumentObjectGroupPython] N_element045  label="N_element : 0.762"  # scripted group (container) (typed FeaturePython)
  n = 0.035022
FEATURE [App::DocumentObjectGroupPython] O_element097  label="O_element : 0.293"  # scripted group (container) (typed FeaturePython)
  n = 0.293366
FEATURE [App::DocumentObjectGroupPython] G4_TISSUE_PROPANE  label="G4_TISSUE-PROPANE"  # scripted group (container) (typed FeaturePython)
  Dunit = g/cm3
  Dvalue = 0.00182628
  Group = -> [H_element103,C_element113,N_element045,O_element097]
  conduct = 2
  density = 1
  expand = 3
  formula = G4_TISSUE-PROPANE
  name = G4_TISSUE-PROPANE
  specific = 4
FEATURE [App::DocumentObjectGroupPython] Ti_element003  label="Ti_element : 1"  # scripted group (container) (typed FeaturePython)
  n = 1
  ref = Ti_element
FEATURE [App::DocumentObjectGroupPython] O_element098  label="O_element : 052"  # scripted group (container) (typed FeaturePython)
  n = 2
  ref = O_element
FEATURE [App::DocumentObjectGroupPython] G4_TITANIUM_DIOXIDE  # scripted group (container) (typed FeaturePython)
  Dunit = g/cm3
  Dvalue = 4.26
  Group = -> [Ti_element003,O_element098]
  conduct = 2
  density = 1
  expand = 3
  formula = G4_TITANIUM_DIOXIDE
  name = G4_TITANIUM_DIOXIDE
  specific = 4
FEATURE [App::DocumentObjectGroupPython] C_element114  label="C_element : 061"  # scripted group (container) (typed FeaturePython)
  n = 7
  ref = C_element
FEATURE [App::DocumentObjectGroupPython] H_element104  label="H_element : 055"  # scripted group (container) (typed FeaturePython)
  n = 8
  ref = H_element
FEATURE [App::DocumentObjectGroupPython] G4_TOLUENE  # scripted group (container) (typed FeaturePython)
  Dunit = g/cm3
  Dvalue = 0.8669
  Group = -> [C_element114,H_element104]
  conduct = 2
  density = 1
  expand = 3
  formula = G4_TOLUENE
  name = G4_TOLUENE
  specific = 4
FEATURE [App::DocumentObjectGroupPython] C_element115  label="C_element : 062"  # scripted group (container) (typed FeaturePython)
  n = 2
  ref = C_element
FEATURE [App::DocumentObjectGroupPython] H_element105  label="H_element : 056"  # scripted group (container) (typed FeaturePython)
  n = 1
  ref = H_element
FEATURE [App::DocumentObjectGroupPython] Cl_element028  label="Cl_element : 014"  # scripted group (container) (typed FeaturePython)
  n = 3
  ref = Cl_element
FEATURE [App::DocumentObjectGroupPython] G4_TRICHLOROETHYLENE  # scripted group (container) (typed FeaturePython)
  Dunit = g/cm3
  Dvalue = 1.46
  Group = -> [C_element115,H_element105,Cl_element028]
  conduct = 2
  density = 1
  expand = 3
  formula = G4_TRICHLOROETHYLENE
  name = G4_TRICHLOROETHYLENE
  specific = 4
FEATURE [App::DocumentObjectGroupPython] C_element116  label="C_element : 063"  # scripted group (container) (typed FeaturePython)
  n = 6
  ref = C_element
FEATURE [App::DocumentObjectGroupPython] H_element106  label="H_element : 15"  # scripted group (container) (typed FeaturePython)
  n = 15
  ref = H_element
FEATURE [App::DocumentObjectGroupPython] O_element099  label="O_element : 053"  # scripted group (container) (typed FeaturePython)
  n = 4
  ref = O_element
FEATURE [App::DocumentObjectGroupPython] P_element012  label="P_element : 1"  # scripted group (container) (typed FeaturePython)
  n = 1
  ref = P_element
FEATURE [App::DocumentObjectGroupPython] G4_TRIETHYL_PHOSPHATE  # scripted group (container) (typed FeaturePython)
  Dunit = g/cm3
  Dvalue = 1.07
  Group = -> [C_element116,H_element106,O_element099,P_element012]
  conduct = 2
  density = 1
  expand = 3
  formula = G4_TRIETHYL_PHOSPHATE
  name = G4_TRIETHYL_PHOSPHATE
  specific = 4
FEATURE [App::DocumentObjectGroupPython] W_element003  label="W_element : 003"  # scripted group (container) (typed FeaturePython)
  n = 1
  ref = W_element
FEATURE [App::DocumentObjectGroupPython] F_element017  label="F_element : 6"  # scripted group (container) (typed FeaturePython)
  n = 6
  ref = F_element
FEATURE [App::DocumentObjectGroupPython] G4_TUNGSTEN_HEXAFLUORIDE  # scripted group (container) (typed FeaturePython)
  Dunit = g/cm3
  Dvalue = 2.4
  Group = -> [W_element003,F_element017]
  conduct = 2
  density = 1
  expand = 3
  formula = G4_TUNGSTEN_HEXAFLUORIDE
  name = G4_TUNGSTEN_HEXAFLUORIDE
  specific = 4
FEATURE [App::DocumentObjectGroupPython] U_element001  label="U_element : 1"  # scripted group (container) (typed FeaturePython)
  n = 1
  ref = U_element
FEATURE [App::DocumentObjectGroupPython] C_element117  label="C_element : 064"  # scripted group (container) (typed FeaturePython)
  n = 2
  ref = C_element
FEATURE [App::DocumentObjectGroupPython] G4_URANIUM_DICARBIDE  # scripted group (container) (typed FeaturePython)
  Dunit = g/cm3
  Dvalue = 11.28
  Group = -> [U_element001,C_element117]
  conduct = 2
  density = 1
  expand = 3
  formula = G4_URANIUM_DICARBIDE
  name = G4_URANIUM_DICARBIDE
  specific = 4
FEATURE [App::DocumentObjectGroupPython] U_element002  label="U_element : 002"  # scripted group (container) (typed FeaturePython)
  n = 1
  ref = U_element
FEATURE [App::DocumentObjectGroupPython] C_element118  label="C_element : 065"  # scripted group (container) (typed FeaturePython)
  n = 1
  ref = C_element
FEATURE [App::DocumentObjectGroupPython] G4_URANIUM_MONOCARBIDE  # scripted group (container) (typed FeaturePython)
  Dunit = g/cm3
  Dvalue = 13.63
  Group = -> [U_element002,C_element118]
  conduct = 2
  density = 1
  expand = 3
  formula = G4_URANIUM_MONOCARBIDE
  name = G4_URANIUM_MONOCARBIDE
  specific = 4
FEATURE [App::DocumentObjectGroupPython] U_element003  label="U_element : 003"  # scripted group (container) (typed FeaturePython)
  n = 1
  ref = U_element
FEATURE [App::DocumentObjectGroupPython] O_element100  label="O_element : 054"  # scripted group (container) (typed FeaturePython)
  n = 2
  ref = O_element
FEATURE [App::DocumentObjectGroupPython] G4_URANIUM_OXIDE  # scripted group (container) (typed FeaturePython)
  Dunit = g/cm3
  Dvalue = 10.96
  Group = -> [U_element003,O_element100]
  conduct = 2
  density = 1
  expand = 3
  formula = G4_URANIUM_OXIDE
  name = G4_URANIUM_OXIDE
  specific = 4
FEATURE [App::DocumentObjectGroupPython] C_element119  label="C_element : 066"  # scripted group (container) (typed FeaturePython)
  n = 1
  ref = C_element
FEATURE [App::DocumentObjectGroupPython] H_element107  label="H_element : 057"  # scripted group (container) (typed FeaturePython)
  n = 4
  ref = H_element
FEATURE [App::DocumentObjectGroupPython] N_element046  label="N_element : 019"  # scripted group (container) (typed FeaturePython)
  n = 2
  ref = N_element
FEATURE [App::DocumentObjectGroupPython] O_element101  label="O_element : 055"  # scripted group (container) (typed FeaturePython)
  n = 1
  ref = O_element
FEATURE [App::DocumentObjectGroupPython] G4_UREA  # scripted group (container) (typed FeaturePython)
  Dunit = g/cm3
  Dvalue = 1.323
  Group = -> [C_element119,H_element107,N_element046,O_element101]
  conduct = 2
  density = 1
  expand = 3
  formula = G4_UREA
  name = G4_UREA
  specific = 4
FEATURE [App::DocumentObjectGroupPython] C_element120  label="C_element : 067"  # scripted group (container) (typed FeaturePython)
  n = 5
  ref = C_element
FEATURE [App::DocumentObjectGroupPython] H_element108  label="H_element : 058"  # scripted group (container) (typed FeaturePython)
  n = 11
  ref = H_element
FEATURE [App::DocumentObjectGroupPython] N_element047  label="N_element : 020"  # scripted group (container) (typed FeaturePython)
  n = 1
  ref = N_element
FEATURE [App::DocumentObjectGroupPython] O_element102  label="O_element : 056"  # scripted group (container) (typed FeaturePython)
  n = 2
  ref = O_element
FEATURE [App::DocumentObjectGroupPython] G4_VALINE  # scripted group (container) (typed FeaturePython)
  Dunit = g/cm3
  Dvalue = 1.23
  Group = -> [C_element120,H_element108,N_element047,O_element102]
  conduct = 2
  density = 1
  expand = 3
  formula = G4_VALINE
  name = G4_VALINE
  specific = 4
FEATURE [App::DocumentObjectGroupPython] H_element109  label="H_element : 0.009"  # scripted group (container) (typed FeaturePython)
  n = 0.009417
FEATURE [App::DocumentObjectGroupPython] C_element121  label="C_element : 0.281"  # scripted group (container) (typed FeaturePython)
  n = 0.280555
FEATURE [App::DocumentObjectGroupPython] F_element018  label="F_element : 0.710"  # scripted group (container) (typed FeaturePython)
  n = 0.710028
FEATURE [App::DocumentObjectGroupPython] G4_VITON  # scripted group (container) (typed FeaturePython)
  Dunit = g/cm3
  Dvalue = 1.8
  Group = -> [H_element109,C_element121,F_element018]
  conduct = 2
  density = 1
  expand = 3
  formula = G4_VITON
  name = G4_VITON
  specific = 4
FEATURE [App::DocumentObjectGroupPython] H_element110  label="H_element : 059"  # scripted group (container) (typed FeaturePython)
  n = 2
  ref = H_element
FEATURE [App::DocumentObjectGroupPython] O_element103  label="O_element : 057"  # scripted group (container) (typed FeaturePython)
  n = 1
  ref = O_element
FEATURE [App::DocumentObjectGroupPython] G4_WATER  # scripted group (container) (typed FeaturePython)
  Dunit = g/cm3
  Dvalue = 1
  Group = -> [H_element110,O_element103]
  conduct = 2
  density = 1
  expand = 3
  formula = G4_WATER
  name = G4_WATER
  specific = 4
FEATURE [App::DocumentObjectGroupPython] H_element111  label="H_element : 060"  # scripted group (container) (typed FeaturePython)
  n = 2
  ref = H_element
FEATURE [App::DocumentObjectGroupPython] O_element104  label="O_element : 058"  # scripted group (container) (typed FeaturePython)
  n = 1
  ref = O_element
FEATURE [App::DocumentObjectGroupPython] G4_WATER_VAPOR  # scripted group (container) (typed FeaturePython)
  Dunit = g/cm3
  Dvalue = 0.000756182
  Group = -> [H_element111,O_element104]
  conduct = 2
  density = 1
  expand = 3
  formula = G4_WATER_VAPOR
  name = G4_WATER_VAPOR
  specific = 4
FEATURE [App::DocumentObjectGroupPython] C_element122  label="C_element : 068"  # scripted group (container) (typed FeaturePython)
  n = 8
  ref = C_element
FEATURE [App::DocumentObjectGroupPython] H_element112  label="H_element : 061"  # scripted group (container) (typed FeaturePython)
  n = 10
  ref = H_element
FEATURE [App::DocumentObjectGroupPython] G4_XYLENE  # scripted group (container) (typed FeaturePython)
  Dunit = g/cm3
  Dvalue = 0.87
  Group = -> [C_element122,H_element112]
  conduct = 2
  density = 1
  expand = 3
  formula = G4_XYLENE
  name = G4_XYLENE
  specific = 4
FEATURE [App::DocumentObjectGroupPython] C_element123  label="C_element : 069"  # scripted group (container) (typed FeaturePython)
  n = 1
  ref = C_element
FEATURE [App::DocumentObjectGroupPython] G4_GRAPHITE  # scripted group (container) (typed FeaturePython)
  Dunit = g/cm3
  Dvalue = 2.21
  Group = -> [C_element123]
  conduct = 2
  density = 1
  expand = 3
  formula = G4_GRAPHITE
  name = G4_GRAPHITE
  specific = 4
FEATURE [App::DocumentObjectGroupPython] NIST  # scripted group (container) (typed FeaturePython)
  Group = -> [G4_A_150_TISSUE,G4_ACETONE,G4_ACETYLENE,G4_ADENINE,G4_ADIPOSE_TISSUE_ICRP,G4_AIR,G4_ALANINE,G4_ALUMINUM_OXIDE,G4_AMBER,G4_AMMONIA,G4_ANILINE,G4_ANTHRACENE,G4_B_100_BONE,G4_BAKELITE,G4_BARIUM_FLUORIDE,G4_BARIUM_SULFATE,G4_BENZENE,G4_BERYLLIUM_OXIDE,G4_BGO,G4_BLOOD_ICRP,G4_BONE_COMPACT_ICRU,G4_BONE_CORTICAL_ICRP,G4_BORON_CARBIDE,G4_BORON_OXIDE,G4_BRAIN_ICRP,G4_BUTANE,G4_N_BUTYL_ALCOHOL,G4_C_552,+152 more]
FEATURE [App::DocumentObjectGroupPython] H_element113  label="H_element : 062"  # scripted group (container) (typed FeaturePython)
  n = 1
  ref = H_element
FEATURE [App::DocumentObjectGroupPython] G4_H  # scripted group (container) (typed FeaturePython)
  Dunit = g/cm3
  Dvalue = 8.3748e-05
  Group = -> [H_element113]
  conduct = 2
  density = 1
  expand = 3
  formula = H
  name = G4_H
  specific = 4
FEATURE [App::DocumentObjectGroupPython] He_element001  label="He_element : 1"  # scripted group (container) (typed FeaturePython)
  n = 1
  ref = He_element
FEATURE [App::DocumentObjectGroupPython] G4_He  # scripted group (container) (typed FeaturePython)
  Dunit = g/cm3
  Dvalue = 0.000166322
  Group = -> [He_element001]
  conduct = 2
  density = 1
  expand = 3
  formula = He
  name = G4_He
  specific = 4
FEATURE [App::DocumentObjectGroupPython] Li_element008  label="Li_element : 008"  # scripted group (container) (typed FeaturePython)
  n = 1
  ref = Li_element
FEATURE [App::DocumentObjectGroupPython] G4_Li  # scripted group (container) (typed FeaturePython)
  Dunit = g/cm3
  Dvalue = 0.534
  Group = -> [Li_element008]
  conduct = 2
  density = 1
  expand = 3
  formula = Li
  name = G4_Li
  specific = 4
FEATURE [App::DocumentObjectGroupPython] Be_element002  label="Be_element : 002"  # scripted group (container) (typed FeaturePython)
  n = 1
  ref = Be_element
FEATURE [App::DocumentObjectGroupPython] G4_Be  # scripted group (container) (typed FeaturePython)
  Dunit = g/cm3
  Dvalue = 1.848
  Group = -> [Be_element002]
  conduct = 2
  density = 1
  expand = 3
  formula = Be
  name = G4_Be
  specific = 4
FEATURE [App::DocumentObjectGroupPython] B_element007  label="B_element : 007"  # scripted group (container) (typed FeaturePython)
  n = 1
  ref = B_element
FEATURE [App::DocumentObjectGroupPython] G4_B  # scripted group (container) (typed FeaturePython)
  Dunit = g/cm3
  Dvalue = 2.37
  Group = -> [B_element007]
  conduct = 2
  density = 1
  expand = 3
  formula = B
  name = G4_B
  specific = 4
FEATURE [App::DocumentObjectGroupPython] C_element124  label="C_element : 070"  # scripted group (container) (typed FeaturePython)
  n = 1
  ref = C_element
FEATURE [App::DocumentObjectGroupPython] G4_C  # scripted group (container) (typed FeaturePython)
  Dunit = g/cm3
  Dvalue = 2
  Group = -> [C_element124]
  conduct = 2
  density = 1
  expand = 3
  formula = C
  name = G4_C
  specific = 4
FEATURE [App::DocumentObjectGroupPython] N_element048  label="N_element : 021"  # scripted group (container) (typed FeaturePython)
  n = 1
  ref = N_element
FEATURE [App::DocumentObjectGroupPython] G4_N  # scripted group (container) (typed FeaturePython)
  Dunit = g/cm3
  Dvalue = 0.0011652
  Group = -> [N_element048]
  conduct = 2
  density = 1
  expand = 3
  formula = N
  name = G4_N
  specific = 4
FEATURE [App::DocumentObjectGroupPython] O_element105  label="O_element : 059"  # scripted group (container) (typed FeaturePython)
  n = 1
  ref = O_element
FEATURE [App::DocumentObjectGroupPython] G4_O  # scripted group (container) (typed FeaturePython)
  Dunit = g/cm3
  Dvalue = 0.00133151
  Group = -> [O_element105]
  conduct = 2
  density = 1
  expand = 3
  formula = O
  name = G4_O
  specific = 4
FEATURE [App::DocumentObjectGroupPython] F_element019  label="F_element : 008"  # scripted group (container) (typed FeaturePython)
  n = 1
  ref = F_element
FEATURE [App::DocumentObjectGroupPython] G4_F  # scripted group (container) (typed FeaturePython)
  Dunit = g/cm3
  Dvalue = 0.00158029
  Group = -> [F_element019]
  conduct = 2
  density = 1
  expand = 3
  formula = F
  name = G4_F
  specific = 4
FEATURE [App::DocumentObjectGroupPython] Ne_element001  label="Ne_element : 1"  # scripted group (container) (typed FeaturePython)
  n = 1
  ref = Ne_element
FEATURE [App::DocumentObjectGroupPython] G4_Ne  # scripted group (container) (typed FeaturePython)
  Dunit = g/cm3
  Dvalue = 0.000838505
  Group = -> [Ne_element001]
  conduct = 2
  density = 1
  expand = 3
  formula = Ne
  name = G4_Ne
  specific = 4
FEATURE [App::DocumentObjectGroupPython] Na_element020  label="Na_element : 005"  # scripted group (container) (typed FeaturePython)
  n = 1
  ref = Na_element
FEATURE [App::DocumentObjectGroupPython] G4_Na  # scripted group (container) (typed FeaturePython)
  Dunit = g/cm3
  Dvalue = 0.971
  Group = -> [Na_element020]
  conduct = 2
  density = 1
  expand = 3
  formula = Na
  name = G4_Na
  specific = 4
FEATURE [App::DocumentObjectGroupPython] Mg_element011  label="Mg_element : 005"  # scripted group (container) (typed FeaturePython)
  n = 1
  ref = Mg_element
FEATURE [App::DocumentObjectGroupPython] G4_Mg  # scripted group (container) (typed FeaturePython)
  Dunit = g/cm3
  Dvalue = 1.74
  Group = -> [Mg_element011]
  conduct = 2
  density = 1
  expand = 3
  formula = Mg
  name = G4_Mg
  specific = 4
FEATURE [App::DocumentObjectGroupPython] Al_element004  label="Al_element : 1"  # scripted group (container) (typed FeaturePython)
  n = 1
  ref = Al_element
FEATURE [App::DocumentObjectGroupPython] G4_Al  # scripted group (container) (typed FeaturePython)
  Dunit = g/cm3
  Dvalue = 2.699
  Group = -> [Al_element004]
  conduct = 2
  density = 1
  expand = 3
  formula = Al
  name = G4_Al
  specific = 4
FEATURE [App::DocumentObjectGroupPython] Si_element007  label="Si_element : 002"  # scripted group (container) (typed FeaturePython)
  n = 1
  ref = Si_element
FEATURE [App::DocumentObjectGroupPython] G4_Si  # scripted group (container) (typed FeaturePython)
  Dunit = g/cm3
  Dvalue = 2.33
  Group = -> [Si_element007]
  conduct = 2
  density = 1
  expand = 3
  formula = Si
  name = G4_Si
  specific = 4
FEATURE [App::DocumentObjectGroupPython] P_element013  label="P_element : 002"  # scripted group (container) (typed FeaturePython)
  n = 1
  ref = P_element
FEATURE [App::DocumentObjectGroupPython] G4_P  # scripted group (container) (typed FeaturePython)
  Dunit = g/cm3
  Dvalue = 2.2
  Group = -> [P_element013]
  conduct = 2
  density = 1
  expand = 3
  formula = P
  name = G4_P
  specific = 4
FEATURE [App::DocumentObjectGroupPython] S_element023  label="S_element : 007"  # scripted group (container) (typed FeaturePython)
  n = 1
  ref = S_element
FEATURE [App::DocumentObjectGroupPython] G4_S  # scripted group (container) (typed FeaturePython)
  Dunit = g/cm3
  Dvalue = 2
  Group = -> [S_element023]
  conduct = 2
  density = 1
  expand = 3
  formula = S
  name = G4_S
  specific = 4
FEATURE [App::DocumentObjectGroupPython] Cl_element029  label="Cl_element : 015"  # scripted group (container) (typed FeaturePython)
  n = 1
  ref = Cl_element
FEATURE [App::DocumentObjectGroupPython] G4_Cl  # scripted group (container) (typed FeaturePython)
  Dunit = g/cm3
  Dvalue = 0.00299473
  Group = -> [Cl_element029]
  conduct = 2
  density = 1
  expand = 3
  formula = Cl
  name = G4_Cl
  specific = 4
FEATURE [App::DocumentObjectGroupPython] Ar_element002  label="Ar_element : 1"  # scripted group (container) (typed FeaturePython)
  n = 1
  ref = Ar_element
FEATURE [App::DocumentObjectGroupPython] G4_Ar  # scripted group (container) (typed FeaturePython)
  Dunit = g/cm3
  Dvalue = 0.00166201
  Group = -> [Ar_element002]
  conduct = 2
  density = 1
  expand = 3
  formula = Ar
  name = G4_Ar
  specific = 4
FEATURE [App::DocumentObjectGroupPython] K_element013  label="K_element : 003"  # scripted group (container) (typed FeaturePython)
  n = 1
  ref = K_element
FEATURE [App::DocumentObjectGroupPython] G4_K  # scripted group (container) (typed FeaturePython)
  Dunit = g/cm3
  Dvalue = 0.862
  Group = -> [K_element013]
  conduct = 2
  density = 1
  expand = 3
  formula = K
  name = G4_K
  specific = 4
FEATURE [App::DocumentObjectGroupPython] Ca_element014  label="Ca_element : 007"  # scripted group (container) (typed FeaturePython)
  n = 1
  ref = Ca_element
FEATURE [App::DocumentObjectGroupPython] G4_Ca  # scripted group (container) (typed FeaturePython)
  Dunit = g/cm3
  Dvalue = 1.55
  Group = -> [Ca_element014]
  conduct = 2
  density = 1
  expand = 3
  formula = Ca
  name = G4_Ca
  specific = 4
FEATURE [App::DocumentObjectGroupPython] Sc_element001  label="Sc_element : 1"  # scripted group (container) (typed FeaturePython)
  n = 1
  ref = Sc_element
FEATURE [App::DocumentObjectGroupPython] G4_Sc  # scripted group (container) (typed FeaturePython)
  Dunit = g/cm3
  Dvalue = 2.989
  Group = -> [Sc_element001]
  conduct = 2
  density = 1
  expand = 3
  formula = Sc
  name = G4_Sc
  specific = 4
FEATURE [App::DocumentObjectGroupPython] Ti_element004  label="Ti_element : 002"  # scripted group (container) (typed FeaturePython)
  n = 1
  ref = Ti_element
FEATURE [App::DocumentObjectGroupPython] G4_Ti  # scripted group (container) (typed FeaturePython)
  Dunit = g/cm3
  Dvalue = 4.54
  Group = -> [Ti_element004]
  conduct = 2
  density = 1
  expand = 3
  formula = Ti
  name = G4_Ti
  specific = 4
FEATURE [App::DocumentObjectGroupPython] V_element001  label="V_element : 1"  # scripted group (container) (typed FeaturePython)
  n = 1
  ref = V_element
FEATURE [App::DocumentObjectGroupPython] G4_V  # scripted group (container) (typed FeaturePython)
  Dunit = g/cm3
  Dvalue = 6.11
  Group = -> [V_element001]
  conduct = 2
  density = 1
  expand = 3
  formula = V
  name = G4_V
  specific = 4
FEATURE [App::DocumentObjectGroupPython] Cr_element001  label="Cr_element : 1"  # scripted group (container) (typed FeaturePython)
  n = 1
  ref = Cr_element
FEATURE [App::DocumentObjectGroupPython] G4_Cr  # scripted group (container) (typed FeaturePython)
  Dunit = g/cm3
  Dvalue = 7.18
  Group = -> [Cr_element001]
  conduct = 2
  density = 1
  expand = 3
  formula = Cr
  name = G4_Cr
  specific = 4
FEATURE [App::DocumentObjectGroupPython] Mn_element001  label="Mn_element : 1"  # scripted group (container) (typed FeaturePython)
  n = 1
  ref = Mn_element
FEATURE [App::DocumentObjectGroupPython] G4_Mn  # scripted group (container) (typed FeaturePython)
  Dunit = g/cm3
  Dvalue = 7.44
  Group = -> [Mn_element001]
  conduct = 2
  density = 1
  expand = 3
  formula = Mn
  name = G4_Mn
  specific = 4
FEATURE [App::DocumentObjectGroupPython] Fe_element007  label="Fe_element : 004"  # scripted group (container) (typed FeaturePython)
  n = 1
  ref = Fe_element
FEATURE [App::DocumentObjectGroupPython] G4_Fe  # scripted group (container) (typed FeaturePython)
  Dunit = g/cm3
  Dvalue = 7.874
  Group = -> [Fe_element007]
  conduct = 2
  density = 1
  expand = 3
  formula = Fe
  name = G4_Fe
  specific = 4
FEATURE [App::DocumentObjectGroupPython] Co_element001  label="Co_element : 1"  # scripted group (container) (typed FeaturePython)
  n = 1
  ref = Co_element
FEATURE [App::DocumentObjectGroupPython] G4_Co  # scripted group (container) (typed FeaturePython)
  Dunit = g/cm3
  Dvalue = 8.9
  Group = -> [Co_element001]
  conduct = 2
  density = 1
  expand = 3
  formula = Co
  name = G4_Co
  specific = 4
FEATURE [App::DocumentObjectGroupPython] Ni_element001  label="Ni_element : 1"  # scripted group (container) (typed FeaturePython)
  n = 1
  ref = Ni_element
FEATURE [App::DocumentObjectGroupPython] G4_Ni  # scripted group (container) (typed FeaturePython)
  Dunit = g/cm3
  Dvalue = 8.902
  Group = -> [Ni_element001]
  conduct = 2
  density = 1
  expand = 3
  formula = Ni
  name = G4_Ni
  specific = 4
FEATURE [App::DocumentObjectGroupPython] Cu_element001  label="Cu_element : 1"  # scripted group (container) (typed FeaturePython)
  n = 1
  ref = Cu_element
FEATURE [App::DocumentObjectGroupPython] G4_Cu  # scripted group (container) (typed FeaturePython)
  Dunit = g/cm3
  Dvalue = 8.96
  Group = -> [Cu_element001]
  conduct = 2
  density = 1
  expand = 3
  formula = Cu
  name = G4_Cu
  specific = 4
FEATURE [App::DocumentObjectGroupPython] Zn_element001  label="Zn_element : 1"  # scripted group (container) (typed FeaturePython)
  n = 1
  ref = Zn_element
FEATURE [App::DocumentObjectGroupPython] G4_Zn  # scripted group (container) (typed FeaturePython)
  Dunit = g/cm3
  Dvalue = 7.133
  Group = -> [Zn_element001]
  conduct = 2
  density = 1
  expand = 3
  formula = Zn
  name = G4_Zn
  specific = 4
FEATURE [App::DocumentObjectGroupPython] Ga_element002  label="Ga_element : 002"  # scripted group (container) (typed FeaturePython)
  n = 1
  ref = Ga_element
FEATURE [App::DocumentObjectGroupPython] G4_Ga  # scripted group (container) (typed FeaturePython)
  Dunit = g/cm3
  Dvalue = 5.904
  Group = -> [Ga_element002]
  conduct = 2
  density = 1
  expand = 3
  formula = Ga
  name = G4_Ga
  specific = 4
FEATURE [App::DocumentObjectGroupPython] Ge_element002  label="Ge_element : 1"  # scripted group (container) (typed FeaturePython)
  n = 1
  ref = Ge_element
FEATURE [App::DocumentObjectGroupPython] G4_Ge  # scripted group (container) (typed FeaturePython)
  Dunit = g/cm3
  Dvalue = 5.323
  Group = -> [Ge_element002]
  conduct = 2
  density = 1
  expand = 3
  formula = Ge
  name = G4_Ge
  specific = 4
FEATURE [App::DocumentObjectGroupPython] As_element003  label="As_element : 002"  # scripted group (container) (typed FeaturePython)
  n = 1
  ref = As_element
FEATURE [App::DocumentObjectGroupPython] G4_As  # scripted group (container) (typed FeaturePython)
  Dunit = g/cm3
  Dvalue = 5.73
  Group = -> [As_element003]
  conduct = 2
  density = 1
  expand = 3
  formula = As
  name = G4_As
  specific = 4
FEATURE [App::DocumentObjectGroupPython] Se_element001  label="Se_element : 1"  # scripted group (container) (typed FeaturePython)
  n = 1
  ref = Se_element
FEATURE [App::DocumentObjectGroupPython] G4_Se  # scripted group (container) (typed FeaturePython)
  Dunit = g/cm3
  Dvalue = 4.5
  Group = -> [Se_element001]
  conduct = 2
  density = 1
  expand = 3
  formula = Se
  name = G4_Se
  specific = 4
FEATURE [App::DocumentObjectGroupPython] Br_element007  label="Br_element : 004"  # scripted group (container) (typed FeaturePython)
  n = 1
  ref = Br_element
FEATURE [App::DocumentObjectGroupPython] G4_Br  # scripted group (container) (typed FeaturePython)
  Dunit = g/cm3
  Dvalue = 0.0070721
  Group = -> [Br_element007]
  conduct = 2
  density = 1
  expand = 3
  formula = Br
  name = G4_Br
  specific = 4
FEATURE [App::DocumentObjectGroupPython] Kr_element001  label="Kr_element : 1"  # scripted group (container) (typed FeaturePython)
  n = 1
  ref = Kr_element
FEATURE [App::DocumentObjectGroupPython] G4_Kr  # scripted group (container) (typed FeaturePython)
  Dunit = g/cm3
  Dvalue = 0.00347832
  Group = -> [Kr_element001]
  conduct = 2
  density = 1
  expand = 3
  formula = Kr
  name = G4_Kr
  specific = 4
FEATURE [App::DocumentObjectGroupPython] Rb_element001  label="Rb_element : 1"  # scripted group (container) (typed FeaturePython)
  n = 1
  ref = Rb_element
FEATURE [App::DocumentObjectGroupPython] G4_Rb  # scripted group (container) (typed FeaturePython)
  Dunit = g/cm3
  Dvalue = 1.532
  Group = -> [Rb_element001]
  conduct = 2
  density = 1
  expand = 3
  formula = Rb
  name = G4_Rb
  specific = 4
FEATURE [App::DocumentObjectGroupPython] Sr_element001  label="Sr_element : 1"  # scripted group (container) (typed FeaturePython)
  n = 1
  ref = Sr_element
FEATURE [App::DocumentObjectGroupPython] G4_Sr  # scripted group (container) (typed FeaturePython)
  Dunit = g/cm3
  Dvalue = 2.54
  Group = -> [Sr_element001]
  conduct = 2
  density = 1
  expand = 3
  formula = Sr
  name = G4_Sr
  specific = 4
FEATURE [App::DocumentObjectGroupPython] Y_element001  label="Y_element : 1"  # scripted group (container) (typed FeaturePython)
  n = 1
  ref = Y_element
FEATURE [App::DocumentObjectGroupPython] G4_Y  # scripted group (container) (typed FeaturePython)
  Dunit = g/cm3
  Dvalue = 4.469
  Group = -> [Y_element001]
  conduct = 2
  density = 1
  expand = 3
  formula = Y
  name = G4_Y
  specific = 4
FEATURE [App::DocumentObjectGroupPython] Zr_element001  label="Zr_element : 1"  # scripted group (container) (typed FeaturePython)
  n = 1
  ref = Zr_element
FEATURE [App::DocumentObjectGroupPython] G4_Zr  # scripted group (container) (typed FeaturePython)
  Dunit = g/cm3
  Dvalue = 6.506
  Group = -> [Zr_element001]
  conduct = 2
  density = 1
  expand = 3
  formula = Zr
  name = G4_Zr
  specific = 4
FEATURE [App::DocumentObjectGroupPython] Nb_element001  label="Nb_element : 1"  # scripted group (container) (typed FeaturePython)
  n = 1
  ref = Nb_element
FEATURE [App::DocumentObjectGroupPython] G4_Nb  # scripted group (container) (typed FeaturePython)
  Dunit = g/cm3
  Dvalue = 8.57
  Group = -> [Nb_element001]
  conduct = 2
  density = 1
  expand = 3
  formula = Nb
  name = G4_Nb
  specific = 4
FEATURE [App::DocumentObjectGroupPython] Mo_element001  label="Mo_element : 1"  # scripted group (container) (typed FeaturePython)
  n = 1
  ref = Mo_element
FEATURE [App::DocumentObjectGroupPython] G4_Mo  # scripted group (container) (typed FeaturePython)
  Dunit = g/cm3
  Dvalue = 10.22
  Group = -> [Mo_element001]
  conduct = 2
  density = 1
  expand = 3
  formula = Mo
  name = G4_Mo
  specific = 4
FEATURE [App::DocumentObjectGroupPython] Tc_element001  label="Tc_element : 1"  # scripted group (container) (typed FeaturePython)
  n = 1
  ref = Tc_element
FEATURE [App::DocumentObjectGroupPython] G4_Tc  # scripted group (container) (typed FeaturePython)
  Dunit = g/cm3
  Dvalue = 11.5
  Group = -> [Tc_element001]
  conduct = 2
  density = 1
  expand = 3
  formula = Tc
  name = G4_Tc
  specific = 4
FEATURE [App::DocumentObjectGroupPython] Ru_element001  label="Ru_element : 1"  # scripted group (container) (typed FeaturePython)
  n = 1
  ref = Ru_element
FEATURE [App::DocumentObjectGroupPython] G4_Ru  # scripted group (container) (typed FeaturePython)
  Dunit = g/cm3
  Dvalue = 12.41
  Group = -> [Ru_element001]
  conduct = 2
  density = 1
  expand = 3
  formula = Ru
  name = G4_Ru
  specific = 4
FEATURE [App::DocumentObjectGroupPython] Rh_element001  label="Rh_element : 1"  # scripted group (container) (typed FeaturePython)
  n = 1
  ref = Rh_element
FEATURE [App::DocumentObjectGroupPython] G4_Rh  # scripted group (container) (typed FeaturePython)
  Dunit = g/cm3
  Dvalue = 12.41
  Group = -> [Rh_element001]
  conduct = 2
  density = 1
  expand = 3
  formula = Rh
  name = G4_Rh
  specific = 4
FEATURE [App::DocumentObjectGroupPython] Pd_element001  label="Pd_element : 1"  # scripted group (container) (typed FeaturePython)
  n = 1
  ref = Pd_element
FEATURE [App::DocumentObjectGroupPython] G4_Pd  # scripted group (container) (typed FeaturePython)
  Dunit = g/cm3
  Dvalue = 12.02
  Group = -> [Pd_element001]
  conduct = 2
  density = 1
  expand = 3
  formula = Pd
  name = G4_Pd
  specific = 4
FEATURE [App::DocumentObjectGroupPython] Ag_element006  label="Ag_element : 004"  # scripted group (container) (typed FeaturePython)
  n = 1
  ref = Ag_element
FEATURE [App::DocumentObjectGroupPython] G4_Ag  # scripted group (container) (typed FeaturePython)
  Dunit = g/cm3
  Dvalue = 10.5
  Group = -> [Ag_element006]
  conduct = 2
  density = 1
  expand = 3
  formula = Ag
  name = G4_Ag
  specific = 4
FEATURE [App::DocumentObjectGroupPython] Cd_element003  label="Cd_element : 003"  # scripted group (container) (typed FeaturePython)
  n = 1
  ref = Cd_element
FEATURE [App::DocumentObjectGroupPython] G4_Cd  # scripted group (container) (typed FeaturePython)
  Dunit = g/cm3
  Dvalue = 8.65
  Group = -> [Cd_element003]
  conduct = 2
  density = 1
  expand = 3
  formula = Cd
  name = G4_Cd
  specific = 4
FEATURE [App::DocumentObjectGroupPython] In_element001  label="In_element : 1"  # scripted group (container) (typed FeaturePython)
  n = 1
  ref = In_element
FEATURE [App::DocumentObjectGroupPython] G4_In  # scripted group (container) (typed FeaturePython)
  Dunit = g/cm3
  Dvalue = 7.31
  Group = -> [In_element001]
  conduct = 2
  density = 1
  expand = 3
  formula = In
  name = G4_In
  specific = 4
FEATURE [App::DocumentObjectGroupPython] Sn_element001  label="Sn_element : 1"  # scripted group (container) (typed FeaturePython)
  n = 1
  ref = Sn_element
FEATURE [App::DocumentObjectGroupPython] G4_Sn  # scripted group (container) (typed FeaturePython)
  Dunit = g/cm3
  Dvalue = 7.31
  Group = -> [Sn_element001]
  conduct = 2
  density = 1
  expand = 3
  formula = Sn
  name = G4_Sn
  specific = 4
FEATURE [App::DocumentObjectGroupPython] Sb_element001  label="Sb_element : 1"  # scripted group (container) (typed FeaturePython)
  n = 1
  ref = Sb_element
FEATURE [App::DocumentObjectGroupPython] G4_Sb  # scripted group (container) (typed FeaturePython)
  Dunit = g/cm3
  Dvalue = 6.691
  Group = -> [Sb_element001]
  conduct = 2
  density = 1
  expand = 3
  formula = Sb
  name = G4_Sb
  specific = 4
FEATURE [App::DocumentObjectGroupPython] Te_element002  label="Te_element : 002"  # scripted group (container) (typed FeaturePython)
  n = 1
  ref = Te_element
FEATURE [App::DocumentObjectGroupPython] G4_Te  # scripted group (container) (typed FeaturePython)
  Dunit = g/cm3
  Dvalue = 6.24
  Group = -> [Te_element002]
  conduct = 2
  density = 1
  expand = 3
  formula = Te
  name = G4_Te
  specific = 4
FEATURE [App::DocumentObjectGroupPython] I_element010  label="I_element : 006"  # scripted group (container) (typed FeaturePython)
  n = 1
  ref = I_element
FEATURE [App::DocumentObjectGroupPython] G4_I  # scripted group (container) (typed FeaturePython)
  Dunit = g/cm3
  Dvalue = 4.93
  Group = -> [I_element010]
  conduct = 2
  density = 1
  expand = 3
  formula = I
  name = G4_I
  specific = 4
FEATURE [App::DocumentObjectGroupPython] Xe_element001  label="Xe_element : 1"  # scripted group (container) (typed FeaturePython)
  n = 1
  ref = Xe_element
FEATURE [App::DocumentObjectGroupPython] G4_Xe  # scripted group (container) (typed FeaturePython)
  Dunit = g/cm3
  Dvalue = 0.00548536
  Group = -> [Xe_element001]
  conduct = 2
  density = 1
  expand = 3
  formula = Xe
  name = G4_Xe
  specific = 4
FEATURE [App::DocumentObjectGroupPython] Cs_element003  label="Cs_element : 003"  # scripted group (container) (typed FeaturePython)
  n = 1
  ref = Cs_element
FEATURE [App::DocumentObjectGroupPython] G4_Cs  # scripted group (container) (typed FeaturePython)
  Dunit = g/cm3
  Dvalue = 1.873
  Group = -> [Cs_element003]
  conduct = 2
  density = 1
  expand = 3
  formula = Cs
  name = G4_Cs
  specific = 4
FEATURE [App::DocumentObjectGroupPython] Ba_element003  label="Ba_element : 003"  # scripted group (container) (typed FeaturePython)
  n = 1
  ref = Ba_element
FEATURE [App::DocumentObjectGroupPython] G4_Ba  # scripted group (container) (typed FeaturePython)
  Dunit = g/cm3
  Dvalue = 3.5
  Group = -> [Ba_element003]
  conduct = 2
  density = 1
  expand = 3
  formula = Ba
  name = G4_Ba
  specific = 4
FEATURE [App::DocumentObjectGroupPython] La_element003  label="La_element : 003"  # scripted group (container) (typed FeaturePython)
  n = 1
  ref = La_element
FEATURE [App::DocumentObjectGroupPython] G4_La  # scripted group (container) (typed FeaturePython)
  Dunit = g/cm3
  Dvalue = 6.154
  Group = -> [La_element003]
  conduct = 2
  density = 1
  expand = 3
  formula = La
  name = G4_La
  specific = 4
FEATURE [App::DocumentObjectGroupPython] Ce_element002  label="Ce_element : 1"  # scripted group (container) (typed FeaturePython)
  n = 1
  ref = Ce_element
FEATURE [App::DocumentObjectGroupPython] G4_Ce  # scripted group (container) (typed FeaturePython)
  Dunit = g/cm3
  Dvalue = 6.657
  Group = -> [Ce_element002]
  conduct = 2
  density = 1
  expand = 3
  formula = Ce
  name = G4_Ce
  specific = 4
FEATURE [App::DocumentObjectGroupPython] Pr_element001  label="Pr_element : 1"  # scripted group (container) (typed FeaturePython)
  n = 1
  ref = Pr_element
FEATURE [App::DocumentObjectGroupPython] G4_Pr  # scripted group (container) (typed FeaturePython)
  Dunit = g/cm3
  Dvalue = 6.71
  Group = -> [Pr_element001]
  conduct = 2
  density = 1
  expand = 3
  formula = Pr
  name = G4_Pr
  specific = 4
FEATURE [App::DocumentObjectGroupPython] Nd_element001  label="Nd_element : 1"  # scripted group (container) (typed FeaturePython)
  n = 1
  ref = Nd_element
FEATURE [App::DocumentObjectGroupPython] G4_Nd  # scripted group (container) (typed FeaturePython)
  Dunit = g/cm3
  Dvalue = 6.9
  Group = -> [Nd_element001]
  conduct = 2
  density = 1
  expand = 3
  formula = Nd
  name = G4_Nd
  specific = 4
FEATURE [App::DocumentObjectGroupPython] Pm_element001  label="Pm_element : 1"  # scripted group (container) (typed FeaturePython)
  n = 1
  ref = Pm_element
FEATURE [App::DocumentObjectGroupPython] G4_Pm  # scripted group (container) (typed FeaturePython)
  Dunit = g/cm3
  Dvalue = 7.22
  Group = -> [Pm_element001]
  conduct = 2
  density = 1
  expand = 3
  formula = Pm
  name = G4_Pm
  specific = 4
FEATURE [App::DocumentObjectGroupPython] Sm_element001  label="Sm_element : 1"  # scripted group (container) (typed FeaturePython)
  n = 1
  ref = Sm_element
FEATURE [App::DocumentObjectGroupPython] G4_Sm  # scripted group (container) (typed FeaturePython)
  Dunit = g/cm3
  Dvalue = 7.46
  Group = -> [Sm_element001]
  conduct = 2
  density = 1
  expand = 3
  formula = Sm
  name = G4_Sm
  specific = 4
FEATURE [App::DocumentObjectGroupPython] Eu_element001  label="Eu_element : 1"  # scripted group (container) (typed FeaturePython)
  n = 1
  ref = Eu_element
FEATURE [App::DocumentObjectGroupPython] G4_Eu  # scripted group (container) (typed FeaturePython)
  Dunit = g/cm3
  Dvalue = 5.243
  Group = -> [Eu_element001]
  conduct = 2
  density = 1
  expand = 3
  formula = Eu
  name = G4_Eu
  specific = 4
FEATURE [App::DocumentObjectGroupPython] Gd_element002  label="Gd_element : 1"  # scripted group (container) (typed FeaturePython)
  n = 1
  ref = Gd_element
FEATURE [App::DocumentObjectGroupPython] G4_Gd  # scripted group (container) (typed FeaturePython)
  Dunit = g/cm3
  Dvalue = 7.9004
  Group = -> [Gd_element002]
  conduct = 2
  density = 1
  expand = 3
  formula = Gd
  name = G4_Gd
  specific = 4
FEATURE [App::DocumentObjectGroupPython] Tb_element001  label="Tb_element : 1"  # scripted group (container) (typed FeaturePython)
  n = 1
  ref = Tb_element
FEATURE [App::DocumentObjectGroupPython] G4_Tb  # scripted group (container) (typed FeaturePython)
  Dunit = g/cm3
  Dvalue = 8.229
  Group = -> [Tb_element001]
  conduct = 2
  density = 1
  expand = 3
  formula = Tb
  name = G4_Tb
  specific = 4
FEATURE [App::DocumentObjectGroupPython] Dy_element001  label="Dy_element : 1"  # scripted group (container) (typed FeaturePython)
  n = 1
  ref = Dy_element
FEATURE [App::DocumentObjectGroupPython] G4_Dy  # scripted group (container) (typed FeaturePython)
  Dunit = g/cm3
  Dvalue = 8.55
  Group = -> [Dy_element001]
  conduct = 2
  density = 1
  expand = 3
  formula = Dy
  name = G4_Dy
  specific = 4
FEATURE [App::DocumentObjectGroupPython] Ho_element001  label="Ho_element : 1"  # scripted group (container) (typed FeaturePython)
  n = 1
  ref = Ho_element
FEATURE [App::DocumentObjectGroupPython] G4_Ho  # scripted group (container) (typed FeaturePython)
  Dunit = g/cm3
  Dvalue = 8.795
  Group = -> [Ho_element001]
  conduct = 2
  density = 1
  expand = 3
  formula = Ho
  name = G4_Ho
  specific = 4
FEATURE [App::DocumentObjectGroupPython] Er_element001  label="Er_element : 1"  # scripted group (container) (typed FeaturePython)
  n = 1
  ref = Er_element
FEATURE [App::DocumentObjectGroupPython] G4_Er  # scripted group (container) (typed FeaturePython)
  Dunit = g/cm3
  Dvalue = 9.066
  Group = -> [Er_element001]
  conduct = 2
  density = 1
  expand = 3
  formula = Er
  name = G4_Er
  specific = 4
FEATURE [App::DocumentObjectGroupPython] Tm_element001  label="Tm_element : 1"  # scripted group (container) (typed FeaturePython)
  n = 1
  ref = Tm_element
FEATURE [App::DocumentObjectGroupPython] G4_Tm  # scripted group (container) (typed FeaturePython)
  Dunit = g/cm3
  Dvalue = 9.321
  Group = -> [Tm_element001]
  conduct = 2
  density = 1
  expand = 3
  formula = Tm
  name = G4_Tm
  specific = 4
FEATURE [App::DocumentObjectGroupPython] Yb_element001  label="Yb_element : 1"  # scripted group (container) (typed FeaturePython)
  n = 1
  ref = Yb_element
FEATURE [App::DocumentObjectGroupPython] G4_Yb  # scripted group (container) (typed FeaturePython)
  Dunit = g/cm3
  Dvalue = 6.73
  Group = -> [Yb_element001]
  conduct = 2
  density = 1
  expand = 3
  formula = Yb
  name = G4_Yb
  specific = 4
FEATURE [App::DocumentObjectGroupPython] Lu_element001  label="Lu_element : 1"  # scripted group (container) (typed FeaturePython)
  n = 1
  ref = Lu_element
FEATURE [App::DocumentObjectGroupPython] G4_Lu  # scripted group (container) (typed FeaturePython)
  Dunit = g/cm3
  Dvalue = 9.84
  Group = -> [Lu_element001]
  conduct = 2
  density = 1
  expand = 3
  formula = Lu
  name = G4_Lu
  specific = 4
FEATURE [App::DocumentObjectGroupPython] Hf_element001  label="Hf_element : 1"  # scripted group (container) (typed FeaturePython)
  n = 1
  ref = Hf_element
FEATURE [App::DocumentObjectGroupPython] G4_Hf  # scripted group (container) (typed FeaturePython)
  Dunit = g/cm3
  Dvalue = 13.31
  Group = -> [Hf_element001]
  conduct = 2
  density = 1
  expand = 3
  formula = Hf
  name = G4_Hf
  specific = 4
FEATURE [App::DocumentObjectGroupPython] Ta_element001  label="Ta_element : 1"  # scripted group (container) (typed FeaturePython)
  n = 1
  ref = Ta_element
FEATURE [App::DocumentObjectGroupPython] G4_Ta  # scripted group (container) (typed FeaturePython)
  Dunit = g/cm3
  Dvalue = 16.654
  Group = -> [Ta_element001]
  conduct = 2
  density = 1
  expand = 3
  formula = Ta
  name = G4_Ta
  specific = 4
FEATURE [App::DocumentObjectGroupPython] W_element004  label="W_element : 004"  # scripted group (container) (typed FeaturePython)
  n = 1
  ref = W_element
FEATURE [App::DocumentObjectGroupPython] G4_W  # scripted group (container) (typed FeaturePython)
  Dunit = g/cm3
  Dvalue = 19.3
  Group = -> [W_element004]
  conduct = 2
  density = 1
  expand = 3
  formula = W
  name = G4_W
  specific = 4
FEATURE [App::DocumentObjectGroupPython] Re_element001  label="Re_element : 1"  # scripted group (container) (typed FeaturePython)
  n = 1
  ref = Re_element
FEATURE [App::DocumentObjectGroupPython] G4_Re  # scripted group (container) (typed FeaturePython)
  Dunit = g/cm3
  Dvalue = 21.02
  Group = -> [Re_element001]
  conduct = 2
  density = 1
  expand = 3
  formula = Re
  name = G4_Re
  specific = 4
FEATURE [App::DocumentObjectGroupPython] Os_element001  label="Os_element : 1"  # scripted group (container) (typed FeaturePython)
  n = 1
  ref = Os_element
FEATURE [App::DocumentObjectGroupPython] G4_Os  # scripted group (container) (typed FeaturePython)
  Dunit = g/cm3
  Dvalue = 22.57
  Group = -> [Os_element001]
  conduct = 2
  density = 1
  expand = 3
  formula = Os
  name = G4_Os
  specific = 4
FEATURE [App::DocumentObjectGroupPython] Ir_element001  label="Ir_element : 1"  # scripted group (container) (typed FeaturePython)
  n = 1
  ref = Ir_element
FEATURE [App::DocumentObjectGroupPython] G4_Ir  # scripted group (container) (typed FeaturePython)
  Dunit = g/cm3
  Dvalue = 22.42
  Group = -> [Ir_element001]
  conduct = 2
  density = 1
  expand = 3
  formula = Ir
  name = G4_Ir
  specific = 4
FEATURE [App::DocumentObjectGroupPython] Pt_element001  label="Pt_element : 1"  # scripted group (container) (typed FeaturePython)
  n = 1
  ref = Pt_element
FEATURE [App::DocumentObjectGroupPython] G4_Pt  # scripted group (container) (typed FeaturePython)
  Dunit = g/cm3
  Dvalue = 21.45
  Group = -> [Pt_element001]
  conduct = 2
  density = 1
  expand = 3
  formula = Pt
  name = G4_Pt
  specific = 4
FEATURE [App::DocumentObjectGroupPython] Au_element001  label="Au_element : 1"  # scripted group (container) (typed FeaturePython)
  n = 1
  ref = Au_element
FEATURE [App::DocumentObjectGroupPython] G4_Au  # scripted group (container) (typed FeaturePython)
  Dunit = g/cm3
  Dvalue = 19.32
  Group = -> [Au_element001]
  conduct = 2
  density = 1
  expand = 3
  formula = Au
  name = G4_Au
  specific = 4
FEATURE [App::DocumentObjectGroupPython] Hg_element002  label="Hg_element : 002"  # scripted group (container) (typed FeaturePython)
  n = 1
  ref = Hg_element
FEATURE [App::DocumentObjectGroupPython] G4_Hg  # scripted group (container) (typed FeaturePython)
  Dunit = g/cm3
  Dvalue = 13.546
  Group = -> [Hg_element002]
  conduct = 2
  density = 1
  expand = 3
  formula = Hg
  name = G4_Hg
  specific = 4
FEATURE [App::DocumentObjectGroupPython] Tl_element002  label="Tl_element : 002"  # scripted group (container) (typed FeaturePython)
  n = 1
  ref = Tl_element
FEATURE [App::DocumentObjectGroupPython] G4_Tl  # scripted group (container) (typed FeaturePython)
  Dunit = g/cm3
  Dvalue = 11.72
  Group = -> [Tl_element002]
  conduct = 2
  density = 1
  expand = 3
  formula = Tl
  name = G4_Tl
  specific = 4
FEATURE [App::DocumentObjectGroupPython] Pb_element003  label="Pb_element : 1"  # scripted group (container) (typed FeaturePython)
  n = 1
  ref = Pb_element
FEATURE [App::DocumentObjectGroupPython] G4_Pb  # scripted group (container) (typed FeaturePython)
  Dunit = g/cm3
  Dvalue = 11.35
  Group = -> [Pb_element003]
  conduct = 2
  density = 1
  expand = 3
  formula = Pb
  name = G4_Pb
  specific = 4
FEATURE [App::DocumentObjectGroupPython] Bi_element002  label="Bi_element : 1"  # scripted group (container) (typed FeaturePython)
  n = 1
  ref = Bi_element
FEATURE [App::DocumentObjectGroupPython] G4_Bi  # scripted group (container) (typed FeaturePython)
  Dunit = g/cm3
  Dvalue = 9.747
  Group = -> [Bi_element002]
  conduct = 2
  density = 1
  expand = 3
  formula = Bi
  name = G4_Bi
  specific = 4
FEATURE [App::DocumentObjectGroupPython] Po_element001  label="Po_element : 1"  # scripted group (container) (typed FeaturePython)
  n = 1
  ref = Po_element
FEATURE [App::DocumentObjectGroupPython] G4_Po  # scripted group (container) (typed FeaturePython)
  Dunit = g/cm3
  Dvalue = 9.32
  Group = -> [Po_element001]
  conduct = 2
  density = 1
  expand = 3
  formula = Po
  name = G4_Po
  specific = 4
FEATURE [App::DocumentObjectGroupPython] At_element001  label="At_element : 1"  # scripted group (container) (typed FeaturePython)
  n = 1
  ref = At_element
FEATURE [App::DocumentObjectGroupPython] G4_At  # scripted group (container) (typed FeaturePython)
  Dunit = g/cm3
  Dvalue = 9.32
  Group = -> [At_element001]
  conduct = 2
  density = 1
  expand = 3
  formula = At
  name = G4_At
  specific = 4
FEATURE [App::DocumentObjectGroupPython] Rn_element001  label="Rn_element : 1"  # scripted group (container) (typed FeaturePython)
  n = 1
  ref = Rn_element
FEATURE [App::DocumentObjectGroupPython] G4_Rn  # scripted group (container) (typed FeaturePython)
  Dunit = g/cm3
  Dvalue = 0.00900662
  Group = -> [Rn_element001]
  conduct = 2
  density = 1
  expand = 3
  formula = Rn
  name = G4_Rn
  specific = 4
FEATURE [App::DocumentObjectGroupPython] Fr_element001  label="Fr_element : 1"  # scripted group (container) (typed FeaturePython)
  n = 1
  ref = Fr_element
FEATURE [App::DocumentObjectGroupPython] G4_Fr  # scripted group (container) (typed FeaturePython)
  Dunit = g/cm3
  Dvalue = 1
  Group = -> [Fr_element001]
  conduct = 2
  density = 1
  expand = 3
  formula = Fr
  name = G4_Fr
  specific = 4
FEATURE [App::DocumentObjectGroupPython] Ra_element001  label="Ra_element : 1"  # scripted group (container) (typed FeaturePython)
  n = 1
  ref = Ra_element
FEATURE [App::DocumentObjectGroupPython] G4_Ra  # scripted group (container) (typed FeaturePython)
  Dunit = g/cm3
  Dvalue = 5
  Group = -> [Ra_element001]
  conduct = 2
  density = 1
  expand = 3
  formula = Ra
  name = G4_Ra
  specific = 4
FEATURE [App::DocumentObjectGroupPython] Ac_element001  label="Ac_element : 1"  # scripted group (container) (typed FeaturePython)
  n = 1
  ref = Ac_element
FEATURE [App::DocumentObjectGroupPython] G4_Ac  # scripted group (container) (typed FeaturePython)
  Dunit = g/cm3
  Dvalue = 10.07
  Group = -> [Ac_element001]
  conduct = 2
  density = 1
  expand = 3
  formula = Ac
  name = G4_Ac
  specific = 4
FEATURE [App::DocumentObjectGroupPython] Th_element001  label="Th_element : 1"  # scripted group (container) (typed FeaturePython)
  n = 1
  ref = Th_element
FEATURE [App::DocumentObjectGroupPython] G4_Th  # scripted group (container) (typed FeaturePython)
  Dunit = g/cm3
  Dvalue = 11.72
  Group = -> [Th_element001]
  conduct = 2
  density = 1
  expand = 3
  formula = Th
  name = G4_Th
  specific = 4
FEATURE [App::DocumentObjectGroupPython] Pa_element001  label="Pa_element : 1"  # scripted group (container) (typed FeaturePython)
  n = 1
  ref = Pa_element
FEATURE [App::DocumentObjectGroupPython] G4_Pa  # scripted group (container) (typed FeaturePython)
  Dunit = g/cm3
  Dvalue = 15.37
  Group = -> [Pa_element001]
  conduct = 2
  density = 1
  expand = 3
  formula = Pa
  name = G4_Pa
  specific = 4
FEATURE [App::DocumentObjectGroupPython] U_element004  label="U_element : 004"  # scripted group (container) (typed FeaturePython)
  n = 1
  ref = U_element
FEATURE [App::DocumentObjectGroupPython] G4_U  # scripted group (container) (typed FeaturePython)
  Dunit = g/cm3
  Dvalue = 18.95
  Group = -> [U_element004]
  conduct = 2
  density = 1
  expand = 3
  formula = U
  name = G4_U
  specific = 4
FEATURE [App::DocumentObjectGroupPython] Np_element001  label="Np_element : 1"  # scripted group (container) (typed FeaturePython)
  n = 1
  ref = Np_element
FEATURE [App::DocumentObjectGroupPython] G4_Np  # scripted group (container) (typed FeaturePython)
  Dunit = g/cm3
  Dvalue = 20.25
  Group = -> [Np_element001]
  conduct = 2
  density = 1
  expand = 3
  formula = Np
  name = G4_Np
  specific = 4
FEATURE [App::DocumentObjectGroupPython] Pu_element002  label="Pu_element : 002"  # scripted group (container) (typed FeaturePython)
  n = 1
  ref = Pu_element
FEATURE [App::DocumentObjectGroupPython] G4_Pu  # scripted group (container) (typed FeaturePython)
  Dunit = g/cm3
  Dvalue = 19.84
  Group = -> [Pu_element002]
  conduct = 2
  density = 1
  expand = 3
  formula = Pu
  name = G4_Pu
  specific = 4
FEATURE [App::DocumentObjectGroupPython] Am_element001  label="Am_element : 1"  # scripted group (container) (typed FeaturePython)
  n = 1
  ref = Am_element
FEATURE [App::DocumentObjectGroupPython] G4_Am  # scripted group (container) (typed FeaturePython)
  Dunit = g/cm3
  Dvalue = 13.67
  Group = -> [Am_element001]
  conduct = 2
  density = 1
  expand = 3
  formula = Am
  name = G4_Am
  specific = 4
FEATURE [App::DocumentObjectGroupPython] Cm_element001  label="Cm_element : 1"  # scripted group (container) (typed FeaturePython)
  n = 1
  ref = Cm_element
FEATURE [App::DocumentObjectGroupPython] G4_Cm  # scripted group (container) (typed FeaturePython)
  Dunit = g/cm3
  Dvalue = 13.51
  Group = -> [Cm_element001]
  conduct = 2
  density = 1
  expand = 3
  formula = Cm
  name = G4_Cm
  specific = 4
FEATURE [App::DocumentObjectGroupPython] Bk_element001  label="Bk_element : 1"  # scripted group (container) (typed FeaturePython)
  n = 1
  ref = Bk_element
FEATURE [App::DocumentObjectGroupPython] G4_Bk  # scripted group (container) (typed FeaturePython)
  Dunit = g/cm3
  Dvalue = 14
  Group = -> [Bk_element001]
  conduct = 2
  density = 1
  expand = 3
  formula = Bk
  name = G4_Bk
  specific = 4
FEATURE [App::DocumentObjectGroupPython] Cf_element001  label="Cf_element : 1"  # scripted group (container) (typed FeaturePython)
  n = 1
  ref = Cf_element
FEATURE [App::DocumentObjectGroupPython] G4_Cf  # scripted group (container) (typed FeaturePython)
  Dunit = g/cm3
  Dvalue = 10
  Group = -> [Cf_element001]
  conduct = 2
  density = 1
  expand = 3
  formula = Cf
  name = G4_Cf
  specific = 4
FEATURE [App::DocumentObjectGroupPython] Element  # scripted group (container) (typed FeaturePython)
  Group = -> [G4_H,G4_He,G4_Li,G4_Be,G4_B,G4_C,G4_N,G4_O,G4_F,G4_Ne,G4_Na,G4_Mg,G4_Al,G4_Si,G4_P,G4_S,G4_Cl,G4_Ar,G4_K,G4_Ca,G4_Sc,G4_Ti,G4_V,G4_Cr,G4_Mn,G4_Fe,G4_Co,G4_Ni,G4_Cu,G4_Zn,G4_Ga,G4_Ge,G4_As,G4_Se,G4_Br,G4_Kr,G4_Rb,G4_Sr,G4_Y,G4_Zr,G4_Nb,G4_Mo,G4_Tc,G4_Ru,G4_Rh,G4_Pd,G4_Ag,G4_Cd,G4_In,G4_Sn,G4_Sb,G4_Te,G4_I,G4_Xe,G4_Cs,G4_Ba,G4_La,G4_Ce,G4_Pr,G4_Nd,G4_Pm,G4_Sm,G4_Eu,G4_Gd,G4_Tb,G4_Dy,G4_Ho,G4_Er,+30 more]
FEATURE [App::DocumentObjectGroupPython] H_element114  label="H_element : 063"  # scripted group (container) (typed FeaturePython)
  n = 2
  ref = H_element
FEATURE [App::DocumentObjectGroupPython] G4_lH2  # scripted group (container) (typed FeaturePython)
  Dunit = g/cm3
  Dvalue = 0.0708
  Group = -> [H_element114]
  conduct = 2
  density = 1
  expand = 3
  formula = G4_lH2
  name = G4_lH2
  specific = 4
FEATURE [App::DocumentObjectGroupPython] N_element049  label="N_element : 022"  # scripted group (container) (typed FeaturePython)
  n = 2
  ref = N_element
FEATURE [App::DocumentObjectGroupPython] G4_lN2  # scripted group (container) (typed FeaturePython)
  Dunit = g/cm3
  Dvalue = 0.807
  Group = -> [N_element049]
  conduct = 2
  density = 1
  expand = 3
  formula = G4_lN2
  name = G4_lN2
  specific = 4
FEATURE [App::DocumentObjectGroupPython] O_element106  label="O_element : 060"  # scripted group (container) (typed FeaturePython)
  n = 2
  ref = O_element
FEATURE [App::DocumentObjectGroupPython] G4_lO2  # scripted group (container) (typed FeaturePython)
  Dunit = g/cm3
  Dvalue = 1.141
  Group = -> [O_element106]
  conduct = 2
  density = 1
  expand = 3
  formula = G4_lO2
  name = G4_lO2
  specific = 4
FEATURE [App::DocumentObjectGroupPython] Ar  label="Ar : 1"  # scripted group (container) (typed FeaturePython)
  n = 1
  ref = Ar
FEATURE [App::DocumentObjectGroupPython] G4_lAr  # scripted group (container) (typed FeaturePython)
  Dunit = g/cm3
  Dvalue = 1.396
  Group = -> [Ar]
  conduct = 2
  density = 1
  expand = 3
  formula = G4_lAr
  name = G4_lAr
  specific = 4
FEATURE [App::DocumentObjectGroupPython] Br  label="Br : 1"  # scripted group (container) (typed FeaturePython)
  n = 1
  ref = Br
FEATURE [App::DocumentObjectGroupPython] G4_lBr  # scripted group (container) (typed FeaturePython)
  Dunit = g/cm3
  Dvalue = 3.1028
  Group = -> [Br]
  conduct = 2
  density = 1
  expand = 3
  formula = G4_lBr
  name = G4_lBr
  specific = 4
FEATURE [App::DocumentObjectGroupPython] Kr  label="Kr : 1"  # scripted group (container) (typed FeaturePython)
  n = 1
  ref = Kr
FEATURE [App::DocumentObjectGroupPython] G4_lKr  # scripted group (container) (typed FeaturePython)
  Dunit = g/cm3
  Dvalue = 2.418
  Group = -> [Kr]
  conduct = 2
  density = 1
  expand = 3
  formula = G4_lKr
  name = G4_lKr
  specific = 4
FEATURE [App::DocumentObjectGroupPython] Xe  label="Xe : 1"  # scripted group (container) (typed FeaturePython)
  n = 1
  ref = Xe
FEATURE [App::DocumentObjectGroupPython] G4_lXe  # scripted group (container) (typed FeaturePython)
  Dunit = g/cm3
  Dvalue = 2.953
  Group = -> [Xe]
  conduct = 2
  density = 1
  expand = 3
  formula = G4_lXe
  name = G4_lXe
  specific = 4
FEATURE [App::DocumentObjectGroupPython] O_element107  label="O_element : 061"  # scripted group (container) (typed FeaturePython)
  n = 4
  ref = O_element
FEATURE [App::DocumentObjectGroupPython] Pb_element004  label="Pb_element : 002"  # scripted group (container) (typed FeaturePython)
  n = 1
  ref = Pb_element
FEATURE [App::DocumentObjectGroupPython] W_element005  label="W_element : 005"  # scripted group (container) (typed FeaturePython)
  n = 1
  ref = W_element
FEATURE [App::DocumentObjectGroupPython] G4_PbWO4  # scripted group (container) (typed FeaturePython)
  Dunit = g/cm3
  Dvalue = 8.28
  Group = -> [O_element107,Pb_element004,W_element005]
  conduct = 2
  density = 1
  expand = 3
  formula = G4_PbWO4
  name = G4_PbWO4
  specific = 4
FEATURE [App::DocumentObjectGroupPython] alactic  label="alactic : 1"  # scripted group (container) (typed FeaturePython)
  n = 1
  ref = alactic
FEATURE [App::DocumentObjectGroupPython] G4_Galactic  # scripted group (container) (typed FeaturePython)
  Dunit = g/cm3
  Dvalue = 0
  Group = -> [alactic]
  conduct = 2
  density = 1
  expand = 3
  formula = G4_Galactic
  name = G4_Galactic
  specific = 4
FEATURE [App::DocumentObjectGroupPython] RAPHITE_POROUS  label="RAPHITE_POROUS : 1"  # scripted group (container) (typed FeaturePython)
  n = 1
  ref = RAPHITE_POROUS
FEATURE [App::DocumentObjectGroupPython] G4_GRAPHITE_POROUS  # scripted group (container) (typed FeaturePython)
  Dunit = g/cm3
  Dvalue = 1.7
  Group = -> [RAPHITE_POROUS]
  conduct = 2
  density = 1
  expand = 3
  formula = G4_GRAPHITE_POROUS
  name = G4_GRAPHITE_POROUS
  specific = 4
FEATURE [App::DocumentObjectGroupPython] H_element115  label="H_element : 0.150"  # scripted group (container) (typed FeaturePython)
  n = 0.080538
FEATURE [App::DocumentObjectGroupPython] C_element125  label="C_element : 0.600"  # scripted group (container) (typed FeaturePython)
  n = 0.599848
FEATURE [App::DocumentObjectGroupPython] O_element108  label="O_element : 0.320"  # scripted group (container) (typed FeaturePython)
  n = 0.319614
FEATURE [App::DocumentObjectGroupPython] G4_LUCITE  # scripted group (container) (typed FeaturePython)
  Dunit = g/cm3
  Dvalue = 1.19
  Group = -> [H_element115,C_element125,O_element108]
  conduct = 2
  density = 1
  expand = 3
  formula = G4_LUCITE
  name = G4_LUCITE
  specific = 4
FEATURE [App::DocumentObjectGroupPython] Cu_element002  label="Cu_element : 62"  # scripted group (container) (typed FeaturePython)
  n = 62
  ref = Cu_element
FEATURE [App::DocumentObjectGroupPython] Zn_element002  label="Zn_element : 35"  # scripted group (container) (typed FeaturePython)
  n = 35
  ref = Zn_element
FEATURE [App::DocumentObjectGroupPython] Pb_element005  label="Pb_element : 3"  # scripted group (container) (typed FeaturePython)
  n = 3
  ref = Pb_element
FEATURE [App::DocumentObjectGroupPython] G4_BRASS  # scripted group (container) (typed FeaturePython)
  Dunit = g/cm3
  Dvalue = 8.52
  Group = -> [Cu_element002,Zn_element002,Pb_element005]
  conduct = 2
  density = 1
  expand = 3
  formula = G4_BRASS
  name = G4_BRASS
  specific = 4
FEATURE [App::DocumentObjectGroupPython] Cu_element003  label="Cu_element : 89"  # scripted group (container) (typed FeaturePython)
  n = 89
  ref = Cu_element
FEATURE [App::DocumentObjectGroupPython] Zn_element003  label="Zn_element : 9"  # scripted group (container) (typed FeaturePython)
  n = 9
  ref = Zn_element
FEATURE [App::DocumentObjectGroupPython] Pb_element006  label="Pb_element : 2"  # scripted group (container) (typed FeaturePython)
  n = 2
  ref = Pb_element
FEATURE [App::DocumentObjectGroupPython] G4_BRONZE  # scripted group (container) (typed FeaturePython)
  Dunit = g/cm3
  Dvalue = 8.82
  Group = -> [Cu_element003,Zn_element003,Pb_element006]
  conduct = 2
  density = 1
  expand = 3
  formula = G4_BRONZE
  name = G4_BRONZE
  specific = 4
FEATURE [App::DocumentObjectGroupPython] Fe_element008  label="Fe_element : 74"  # scripted group (container) (typed FeaturePython)
  n = 74
  ref = Fe_element
FEATURE [App::DocumentObjectGroupPython] Cr_element002  label="Cr_element : 18"  # scripted group (container) (typed FeaturePython)
  n = 18
  ref = Cr_element
FEATURE [App::DocumentObjectGroupPython] Ni_element002  label="Ni_element : 8"  # scripted group (container) (typed FeaturePython)
  n = 8
  ref = Ni_element
FEATURE [App::DocumentObjectGroupPython] G4_STAINLESS_STEEL  label="G4_STAINLESS-STEEL"  # scripted group (container) (typed FeaturePython)
  Dunit = g/cm3
  Dvalue = 8
  Group = -> [Fe_element008,Cr_element002,Ni_element002]
  conduct = 2
  density = 1
  expand = 3
  formula = G4_STAINLESS-STEEL
  name = G4_STAINLESS-STEEL
  specific = 4
FEATURE [App::DocumentObjectGroupPython] H_element116  label="H_element : 064"  # scripted group (container) (typed FeaturePython)
  n = 18
  ref = H_element
FEATURE [App::DocumentObjectGroupPython] C_element126  label="C_element : 071"  # scripted group (container) (typed FeaturePython)
  n = 12
  ref = C_element
FEATURE [App::DocumentObjectGroupPython] O_element109  label="O_element : 062"  # scripted group (container) (typed FeaturePython)
  n = 7
  ref = O_element
FEATURE [App::DocumentObjectGroupPython] G4_CR39  # scripted group (container) (typed FeaturePython)
  Dunit = g/cm3
  Dvalue = 1.32
  Group = -> [H_element116,C_element126,O_element109]
  conduct = 2
  density = 1
  expand = 3
  formula = G4_CR39
  name = G4_CR39
  specific = 4
FEATURE [App::DocumentObjectGroupPython] H_element117  label="H_element : 38"  # scripted group (container) (typed FeaturePython)
  n = 38
  ref = H_element
FEATURE [App::DocumentObjectGroupPython] C_element127  label="C_element : 072"  # scripted group (container) (typed FeaturePython)
  n = 18
  ref = C_element
FEATURE [App::DocumentObjectGroupPython] O_element110  label="O_element : 063"  # scripted group (container) (typed FeaturePython)
  n = 1
  ref = O_element
FEATURE [App::DocumentObjectGroupPython] G4_OCTADECANOL  # scripted group (container) (typed FeaturePython)
  Dunit = g/cm3
  Dvalue = 0.812
  Group = -> [H_element117,C_element127,O_element110]
  conduct = 2
  density = 1
  expand = 3
  formula = G4_OCTADECANOL
  name = G4_OCTADECANOL
  specific = 4
FEATURE [App::DocumentObjectGroupPython] HEP  # scripted group (container) (typed FeaturePython)
  Group = -> [G4_lH2,G4_lN2,G4_lO2,G4_lAr,G4_lBr,G4_lKr,G4_lXe,G4_PbWO4,G4_Galactic,G4_GRAPHITE_POROUS,G4_LUCITE,G4_BRASS,G4_BRONZE,G4_STAINLESS_STEEL,G4_CR39,G4_OCTADECANOL]
FEATURE [App::DocumentObjectGroupPython] C_element128  label="C_element : 073"  # scripted group (container) (typed FeaturePython)
  n = 14
  ref = C_element
FEATURE [App::DocumentObjectGroupPython] H_element118  label="H_element : 065"  # scripted group (container) (typed FeaturePython)
  n = 10
  ref = H_element
FEATURE [App::DocumentObjectGroupPython] O_element111  label="O_element : 064"  # scripted group (container) (typed FeaturePython)
  n = 2
  ref = O_element
FEATURE [App::DocumentObjectGroupPython] N_element050  label="N_element : 023"  # scripted group (container) (typed FeaturePython)
  n = 2
  ref = N_element
FEATURE [App::DocumentObjectGroupPython] G4_KEVLAR  # scripted group (container) (typed FeaturePython)
  Dunit = g/cm3
  Dvalue = 1.44
  Group = -> [C_element128,H_element118,O_element111,N_element050]
  conduct = 2
  density = 1
  expand = 3
  formula = G4_KEVLAR
  name = G4_KEVLAR
  specific = 4
FEATURE [App::DocumentObjectGroupPython] C_element129  label="C_element : 074"  # scripted group (container) (typed FeaturePython)
  n = 10
  ref = C_element
FEATURE [App::DocumentObjectGroupPython] H_element119  label="H_element : 066"  # scripted group (container) (typed FeaturePython)
  n = 8
  ref = H_element
FEATURE [App::DocumentObjectGroupPython] O_element112  label="O_element : 065"  # scripted group (container) (typed FeaturePython)
  n = 4
  ref = O_element
FEATURE [App::DocumentObjectGroupPython] G4_DACRON  # scripted group (container) (typed FeaturePython)
  Dunit = g/cm3
  Dvalue = 1.4
  Group = -> [C_element129,H_element119,O_element112]
  conduct = 2
  density = 1
  expand = 3
  formula = G4_DACRON
  name = G4_DACRON
  specific = 4
FEATURE [App::DocumentObjectGroupPython] C_element130  label="C_element : 075"  # scripted group (container) (typed FeaturePython)
  n = 4
  ref = C_element
FEATURE [App::DocumentObjectGroupPython] H_element120  label="H_element : 067"  # scripted group (container) (typed FeaturePython)
  n = 5
  ref = H_element
FEATURE [App::DocumentObjectGroupPython] Cl_element030  label="Cl_element : 016"  # scripted group (container) (typed FeaturePython)
  n = 1
  ref = Cl_element
FEATURE [App::DocumentObjectGroupPython] G4_NEOPRENE  # scripted group (container) (typed FeaturePython)
  Dunit = g/cm3
  Dvalue = 1.23
  Group = -> [C_element130,H_element120,Cl_element030]
  conduct = 2
  density = 1
  expand = 3
  formula = G4_NEOPRENE
  name = G4_NEOPRENE
  specific = 4
FEATURE [App::DocumentObjectGroupPython] Space  # scripted group (container) (typed FeaturePython)
  Group = -> [G4_KEVLAR,G4_DACRON,G4_NEOPRENE]
FEATURE [App::DocumentObjectGroupPython] H_element121  label="H_element : 068"  # scripted group (container) (typed FeaturePython)
  n = 5
  ref = H_element
FEATURE [App::DocumentObjectGroupPython] C_element131  label="C_element : 076"  # scripted group (container) (typed FeaturePython)
  n = 4
  ref = C_element
FEATURE [App::DocumentObjectGroupPython] N_element051  label="N_element : 3"  # scripted group (container) (typed FeaturePython)
  n = 3
  ref = N_element
FEATURE [App::DocumentObjectGroupPython] O_element113  label="O_element : 066"  # scripted group (container) (typed FeaturePython)
  n = 1
  ref = O_element
FEATURE [App::DocumentObjectGroupPython] G4_CYTOSINE  # scripted group (container) (typed FeaturePython)
  Dunit = g/cm3
  Dvalue = 1.55
  Group = -> [H_element121,C_element131,N_element051,O_element113]
  conduct = 2
  density = 1
  expand = 3
  formula = G4_CYTOSINE
  name = G4_CYTOSINE
  specific = 4
FEATURE [App::DocumentObjectGroupPython] H_element122  label="H_element : 069"  # scripted group (container) (typed FeaturePython)
  n = 6
  ref = H_element
FEATURE [App::DocumentObjectGroupPython] C_element132  label="C_element : 077"  # scripted group (container) (typed FeaturePython)
  n = 5
  ref = C_element
FEATURE [App::DocumentObjectGroupPython] N_element052  label="N_element : 024"  # scripted group (container) (typed FeaturePython)
  n = 2
  ref = N_element
FEATURE [App::DocumentObjectGroupPython] O_element114  label="O_element : 067"  # scripted group (container) (typed FeaturePython)
  n = 2
  ref = O_element
FEATURE [App::DocumentObjectGroupPython] G4_THYMINE  # scripted group (container) (typed FeaturePython)
  Dunit = g/cm3
  Dvalue = 1.23
  Group = -> [H_element122,C_element132,N_element052,O_element114]
  conduct = 2
  density = 1
  expand = 3
  formula = G4_THYMINE
  name = G4_THYMINE
  specific = 4
FEATURE [App::DocumentObjectGroupPython] H_element123  label="H_element : 070"  # scripted group (container) (typed FeaturePython)
  n = 4
  ref = H_element
FEATURE [App::DocumentObjectGroupPython] C_element133  label="C_element : 078"  # scripted group (container) (typed FeaturePython)
  n = 4
  ref = C_element
FEATURE [App::DocumentObjectGroupPython] N_element053  label="N_element : 025"  # scripted group (container) (typed FeaturePython)
  n = 2
  ref = N_element
FEATURE [App::DocumentObjectGroupPython] O_element115  label="O_element : 068"  # scripted group (container) (typed FeaturePython)
  n = 2
  ref = O_element
FEATURE [App::DocumentObjectGroupPython] G4_URACIL  # scripted group (container) (typed FeaturePython)
  Dunit = g/cm3
  Dvalue = 1.32
  Group = -> [H_element123,C_element133,N_element053,O_element115]
  conduct = 2
  density = 1
  expand = 3
  formula = G4_URACIL
  name = G4_URACIL
  specific = 4
FEATURE [App::DocumentObjectGroupPython] H_element124  label="H_element : 071"  # scripted group (container) (typed FeaturePython)
  n = 4
  ref = H_element
FEATURE [App::DocumentObjectGroupPython] C_element134  label="C_element : 079"  # scripted group (container) (typed FeaturePython)
  n = 5
  ref = C_element
FEATURE [App::DocumentObjectGroupPython] N_element054  label="N_element : 026"  # scripted group (container) (typed FeaturePython)
  n = 5
  ref = N_element
FEATURE [App::DocumentObjectGroupPython] G4_DNA_ADENINE  # scripted group (container) (typed FeaturePython)
  Dunit = g/cm3
  Dvalue = 1
  Group = -> [H_element124,C_element134,N_element054]
  conduct = 2
  density = 1
  expand = 3
  formula = G4_DNA_ADENINE
  name = G4_DNA_ADENINE
  specific = 4
FEATURE [App::DocumentObjectGroupPython] H_element125  label="H_element : 072"  # scripted group (container) (typed FeaturePython)
  n = 4
  ref = H_element
FEATURE [App::DocumentObjectGroupPython] C_element135  label="C_element : 080"  # scripted group (container) (typed FeaturePython)
  n = 5
  ref = C_element
FEATURE [App::DocumentObjectGroupPython] N_element055  label="N_element : 027"  # scripted group (container) (typed FeaturePython)
  n = 5
  ref = N_element
FEATURE [App::DocumentObjectGroupPython] O_element116  label="O_element : 069"  # scripted group (container) (typed FeaturePython)
  n = 1
  ref = O_element
FEATURE [App::DocumentObjectGroupPython] G4_DNA_GUANINE  # scripted group (container) (typed FeaturePython)
  Dunit = g/cm3
  Dvalue = 1
  Group = -> [H_element125,C_element135,N_element055,O_element116]
  conduct = 2
  density = 1
  expand = 3
  formula = G4_DNA_GUANINE
  name = G4_DNA_GUANINE
  specific = 4
FEATURE [App::DocumentObjectGroupPython] H_element126  label="H_element : 073"  # scripted group (container) (typed FeaturePython)
  n = 4
  ref = H_element
FEATURE [App::DocumentObjectGroupPython] C_element136  label="C_element : 081"  # scripted group (container) (typed FeaturePython)
  n = 4
  ref = C_element
FEATURE [App::DocumentObjectGroupPython] N_element056  label="N_element : 028"  # scripted group (container) (typed FeaturePython)
  n = 3
  ref = N_element
FEATURE [App::DocumentObjectGroupPython] O_element117  label="O_element : 070"  # scripted group (container) (typed FeaturePython)
  n = 1
  ref = O_element
FEATURE [App::DocumentObjectGroupPython] G4_DNA_CYTOSINE  # scripted group (container) (typed FeaturePython)
  Dunit = g/cm3
  Dvalue = 1
  Group = -> [H_element126,C_element136,N_element056,O_element117]
  conduct = 2
  density = 1
  expand = 3
  formula = G4_DNA_CYTOSINE
  name = G4_DNA_CYTOSINE
  specific = 4
FEATURE [App::DocumentObjectGroupPython] H_element127  label="H_element : 074"  # scripted group (container) (typed FeaturePython)
  n = 5
  ref = H_element
FEATURE [App::DocumentObjectGroupPython] C_element137  label="C_element : 082"  # scripted group (container) (typed FeaturePython)
  n = 5
  ref = C_element
FEATURE [App::DocumentObjectGroupPython] N_element057  label="N_element : 029"  # scripted group (container) (typed FeaturePython)
  n = 2
  ref = N_element
FEATURE [App::DocumentObjectGroupPython] O_element118  label="O_element : 071"  # scripted group (container) (typed FeaturePython)
  n = 2
  ref = O_element
FEATURE [App::DocumentObjectGroupPython] G4_DNA_THYMINE  # scripted group (container) (typed FeaturePython)
  Dunit = g/cm3
  Dvalue = 1
  Group = -> [H_element127,C_element137,N_element057,O_element118]
  conduct = 2
  density = 1
  expand = 3
  formula = G4_DNA_THYMINE
  name = G4_DNA_THYMINE
  specific = 4
FEATURE [App::DocumentObjectGroupPython] H_element128  label="H_element : 075"  # scripted group (container) (typed FeaturePython)
  n = 3
  ref = H_element
FEATURE [App::DocumentObjectGroupPython] C_element138  label="C_element : 083"  # scripted group (container) (typed FeaturePython)
  n = 4
  ref = C_element
FEATURE [App::DocumentObjectGroupPython] N_element058  label="N_element : 030"  # scripted group (container) (typed FeaturePython)
  n = 2
  ref = N_element
FEATURE [App::DocumentObjectGroupPython] O_element119  label="O_element : 072"  # scripted group (container) (typed FeaturePython)
  n = 2
  ref = O_element
FEATURE [App::DocumentObjectGroupPython] G4_DNA_URACIL  # scripted group (container) (typed FeaturePython)
  Dunit = g/cm3
  Dvalue = 1
  Group = -> [H_element128,C_element138,N_element058,O_element119]
  conduct = 2
  density = 1
  expand = 3
  formula = G4_DNA_URACIL
  name = G4_DNA_URACIL
  specific = 4
FEATURE [App::DocumentObjectGroupPython] H_element129  label="H_element : 076"  # scripted group (container) (typed FeaturePython)
  n = 10
  ref = H_element
FEATURE [App::DocumentObjectGroupPython] C_element139  label="C_element : 084"  # scripted group (container) (typed FeaturePython)
  n = 10
  ref = C_element
FEATURE [App::DocumentObjectGroupPython] N_element059  label="N_element : 031"  # scripted group (container) (typed FeaturePython)
  n = 5
  ref = N_element
FEATURE [App::DocumentObjectGroupPython] O_element120  label="O_element : 073"  # scripted group (container) (typed FeaturePython)
  n = 4
  ref = O_element
FEATURE [App::DocumentObjectGroupPython] G4_DNA_ADENOSINE  # scripted group (container) (typed FeaturePython)
  Dunit = g/cm3
  Dvalue = 1
  Group = -> [H_element129,C_element139,N_element059,O_element120]
  conduct = 2
  density = 1
  expand = 3
  formula = G4_DNA_ADENOSINE
  name = G4_DNA_ADENOSINE
  specific = 4
FEATURE [App::DocumentObjectGroupPython] H_element130  label="H_element : 077"  # scripted group (container) (typed FeaturePython)
  n = 10
  ref = H_element
FEATURE [App::DocumentObjectGroupPython] C_element140  label="C_element : 085"  # scripted group (container) (typed FeaturePython)
  n = 10
  ref = C_element
FEATURE [App::DocumentObjectGroupPython] N_element060  label="N_element : 032"  # scripted group (container) (typed FeaturePython)
  n = 5
  ref = N_element
FEATURE [App::DocumentObjectGroupPython] O_element121  label="O_element : 074"  # scripted group (container) (typed FeaturePython)
  n = 5
  ref = O_element
FEATURE [App::DocumentObjectGroupPython] G4_DNA_GUANOSINE  # scripted group (container) (typed FeaturePython)
  Dunit = g/cm3
  Dvalue = 1
  Group = -> [H_element130,C_element140,N_element060,O_element121]
  conduct = 2
  density = 1
  expand = 3
  formula = G4_DNA_GUANOSINE
  name = G4_DNA_GUANOSINE
  specific = 4
FEATURE [App::DocumentObjectGroupPython] H_element131  label="H_element : 078"  # scripted group (container) (typed FeaturePython)
  n = 10
  ref = H_element
FEATURE [App::DocumentObjectGroupPython] C_element141  label="C_element : 086"  # scripted group (container) (typed FeaturePython)
  n = 9
  ref = C_element
FEATURE [App::DocumentObjectGroupPython] N_element061  label="N_element : 033"  # scripted group (container) (typed FeaturePython)
  n = 3
  ref = N_element
FEATURE [App::DocumentObjectGroupPython] O_element122  label="O_element : 075"  # scripted group (container) (typed FeaturePython)
  n = 5
  ref = O_element
FEATURE [App::DocumentObjectGroupPython] G4_DNA_CYTIDINE  # scripted group (container) (typed FeaturePython)
  Dunit = g/cm3
  Dvalue = 1
  Group = -> [H_element131,C_element141,N_element061,O_element122]
  conduct = 2
  density = 1
  expand = 3
  formula = G4_DNA_CYTIDINE
  name = G4_DNA_CYTIDINE
  specific = 4
FEATURE [App::DocumentObjectGroupPython] H_element132  label="H_element : 079"  # scripted group (container) (typed FeaturePython)
  n = 9
  ref = H_element
FEATURE [App::DocumentObjectGroupPython] C_element142  label="C_element : 087"  # scripted group (container) (typed FeaturePython)
  n = 9
  ref = C_element
FEATURE [App::DocumentObjectGroupPython] N_element062  label="N_element : 034"  # scripted group (container) (typed FeaturePython)
  n = 2
  ref = N_element
FEATURE [App::DocumentObjectGroupPython] O_element123  label="O_element : 076"  # scripted group (container) (typed FeaturePython)
  n = 6
  ref = O_element
FEATURE [App::DocumentObjectGroupPython] G4_DNA_URIDINE  # scripted group (container) (typed FeaturePython)
  Dunit = g/cm3
  Dvalue = 1
  Group = -> [H_element132,C_element142,N_element062,O_element123]
  conduct = 2
  density = 1
  expand = 3
  formula = G4_DNA_URIDINE
  name = G4_DNA_URIDINE
  specific = 4
FEATURE [App::DocumentObjectGroupPython] H_element133  label="H_element : 080"  # scripted group (container) (typed FeaturePython)
  n = 11
  ref = H_element
FEATURE [App::DocumentObjectGroupPython] C_element143  label="C_element : 088"  # scripted group (container) (typed FeaturePython)
  n = 10
  ref = C_element
FEATURE [App::DocumentObjectGroupPython] N_element063  label="N_element : 035"  # scripted group (container) (typed FeaturePython)
  n = 2
  ref = N_element
FEATURE [App::DocumentObjectGroupPython] O_element124  label="O_element : 077"  # scripted group (container) (typed FeaturePython)
  n = 6
  ref = O_element
FEATURE [App::DocumentObjectGroupPython] G4_DNA_METHYLURIDINE  # scripted group (container) (typed FeaturePython)
  Dunit = g/cm3
  Dvalue = 1
  Group = -> [H_element133,C_element143,N_element063,O_element124]
  conduct = 2
  density = 1
  expand = 3
  formula = G4_DNA_METHYLURIDINE
  name = G4_DNA_METHYLURIDINE
  specific = 4
FEATURE [App::DocumentObjectGroupPython] P_element014  label="P_element : 003"  # scripted group (container) (typed FeaturePython)
  n = 1
  ref = P_element
FEATURE [App::DocumentObjectGroupPython] O_element125  label="O_element : 078"  # scripted group (container) (typed FeaturePython)
  n = 3
  ref = O_element
FEATURE [App::DocumentObjectGroupPython] G4_DNA_MONOPHOSPHATE  # scripted group (container) (typed FeaturePython)
  Dunit = g/cm3
  Dvalue = 1
  Group = -> [P_element014,O_element125]
  conduct = 2
  density = 1
  expand = 3
  formula = G4_DNA_MONOPHOSPHATE
  name = G4_DNA_MONOPHOSPHATE
  specific = 4
FEATURE [App::DocumentObjectGroupPython] H_element134  label="H_element : 081"  # scripted group (container) (typed FeaturePython)
  n = 10
  ref = H_element
FEATURE [App::DocumentObjectGroupPython] C_element144  label="C_element : 089"  # scripted group (container) (typed FeaturePython)
  n = 10
  ref = C_element
FEATURE [App::DocumentObjectGroupPython] N_element064  label="N_element : 036"  # scripted group (container) (typed FeaturePython)
  n = 5
  ref = N_element
FEATURE [App::DocumentObjectGroupPython] O_element126  label="O_element : 079"  # scripted group (container) (typed FeaturePython)
  n = 7
  ref = O_element
FEATURE [App::DocumentObjectGroupPython] P_element015  label="P_element : 004"  # scripted group (container) (typed FeaturePython)
  n = 1
  ref = P_element
FEATURE [App::DocumentObjectGroupPython] G4_DNA_A  # scripted group (container) (typed FeaturePython)
  Dunit = g/cm3
  Dvalue = 1
  Group = -> [H_element134,C_element144,N_element064,O_element126,P_element015]
  conduct = 2
  density = 1
  expand = 3
  formula = G4_DNA_A
  name = G4_DNA_A
  specific = 4
FEATURE [App::DocumentObjectGroupPython] H_element135  label="H_element : 082"  # scripted group (container) (typed FeaturePython)
  n = 10
  ref = H_element
FEATURE [App::DocumentObjectGroupPython] C_element145  label="C_element : 090"  # scripted group (container) (typed FeaturePython)
  n = 10
  ref = C_element
FEATURE [App::DocumentObjectGroupPython] N_element065  label="N_element : 037"  # scripted group (container) (typed FeaturePython)
  n = 5
  ref = N_element
FEATURE [App::DocumentObjectGroupPython] O_element127  label="O_element : 8"  # scripted group (container) (typed FeaturePython)
  n = 8
  ref = O_element
FEATURE [App::DocumentObjectGroupPython] P_element016  label="P_element : 005"  # scripted group (container) (typed FeaturePython)
  n = 1
  ref = P_element
FEATURE [App::DocumentObjectGroupPython] G4_DNA_G  # scripted group (container) (typed FeaturePython)
  Dunit = g/cm3
  Dvalue = 1
  Group = -> [H_element135,C_element145,N_element065,O_element127,P_element016]
  conduct = 2
  density = 1
  expand = 3
  formula = G4_DNA_G
  name = G4_DNA_G
  specific = 4
FEATURE [App::DocumentObjectGroupPython] H_element136  label="H_element : 083"  # scripted group (container) (typed FeaturePython)
  n = 10
  ref = H_element
FEATURE [App::DocumentObjectGroupPython] C_element146  label="C_element : 091"  # scripted group (container) (typed FeaturePython)
  n = 9
  ref = C_element
FEATURE [App::DocumentObjectGroupPython] N_element066  label="N_element : 038"  # scripted group (container) (typed FeaturePython)
  n = 3
  ref = N_element
FEATURE [App::DocumentObjectGroupPython] O_element128  label="O_element : 080"  # scripted group (container) (typed FeaturePython)
  n = 8
  ref = O_element
FEATURE [App::DocumentObjectGroupPython] P_element017  label="P_element : 006"  # scripted group (container) (typed FeaturePython)
  n = 1
  ref = P_element
FEATURE [App::DocumentObjectGroupPython] G4_DNA_C  # scripted group (container) (typed FeaturePython)
  Dunit = g/cm3
  Dvalue = 1
  Group = -> [H_element136,C_element146,N_element066,O_element128,P_element017]
  conduct = 2
  density = 1
  expand = 3
  formula = G4_DNA_C
  name = G4_DNA_C
  specific = 4
FEATURE [App::DocumentObjectGroupPython] H_element137  label="H_element : 084"  # scripted group (container) (typed FeaturePython)
  n = 9
  ref = H_element
FEATURE [App::DocumentObjectGroupPython] C_element147  label="C_element : 092"  # scripted group (container) (typed FeaturePython)
  n = 9
  ref = C_element
FEATURE [App::DocumentObjectGroupPython] N_element067  label="N_element : 039"  # scripted group (container) (typed FeaturePython)
  n = 2
  ref = N_element
FEATURE [App::DocumentObjectGroupPython] O_element129  label="O_element : 9"  # scripted group (container) (typed FeaturePython)
  n = 9
  ref = O_element
FEATURE [App::DocumentObjectGroupPython] P_element018  label="P_element : 007"  # scripted group (container) (typed FeaturePython)
  n = 1
  ref = P_element
FEATURE [App::DocumentObjectGroupPython] G4_DNA_U  # scripted group (container) (typed FeaturePython)
  Dunit = g/cm3
  Dvalue = 1
  Group = -> [H_element137,C_element147,N_element067,O_element129,P_element018]
  conduct = 2
  density = 1
  expand = 3
  formula = G4_DNA_U
  name = G4_DNA_U
  specific = 4
FEATURE [App::DocumentObjectGroupPython] H_element138  label="H_element : 085"  # scripted group (container) (typed FeaturePython)
  n = 11
  ref = H_element
FEATURE [App::DocumentObjectGroupPython] C_element148  label="C_element : 093"  # scripted group (container) (typed FeaturePython)
  n = 10
  ref = C_element
FEATURE [App::DocumentObjectGroupPython] N_element068  label="N_element : 040"  # scripted group (container) (typed FeaturePython)
  n = 2
  ref = N_element
FEATURE [App::DocumentObjectGroupPython] O_element130  label="O_element : 081"  # scripted group (container) (typed FeaturePython)
  n = 9
  ref = O_element
FEATURE [App::DocumentObjectGroupPython] P_element019  label="P_element : 008"  # scripted group (container) (typed FeaturePython)
  n = 1
  ref = P_element
FEATURE [App::DocumentObjectGroupPython] G4_DNA_MU  # scripted group (container) (typed FeaturePython)
  Dunit = g/cm3
  Dvalue = 1
  Group = -> [H_element138,C_element148,N_element068,O_element130,P_element019]
  conduct = 2
  density = 1
  expand = 3
  formula = G4_DNA_MU
  name = G4_DNA_MU
  specific = 4
FEATURE [App::DocumentObjectGroupPython] BioChemical  # scripted group (container) (typed FeaturePython)
  Group = -> [G4_CYTOSINE,G4_THYMINE,G4_URACIL,G4_DNA_ADENINE,G4_DNA_GUANINE,G4_DNA_CYTOSINE,G4_DNA_THYMINE,G4_DNA_URACIL,G4_DNA_ADENOSINE,G4_DNA_GUANOSINE,G4_DNA_CYTIDINE,G4_DNA_URIDINE,G4_DNA_METHYLURIDINE,G4_DNA_MONOPHOSPHATE,G4_DNA_A,G4_DNA_G,G4_DNA_C,G4_DNA_U,G4_DNA_MU]
FEATURE [App::DocumentObjectGroupPython] G4Materials  # scripted group (container) (typed FeaturePython)
  Group = -> [NIST,Element,HEP,Space,BioChemical]
  version = 1
FEATURE [App::DocumentObjectGroupPython] Geant4  # scripted group (container) (typed FeaturePython)
  Group = -> [G4Isotopes,G4Elements,G4Materials]
FEATURE [App::DocumentObjectGroupPython] Materials  # scripted group (container) (typed FeaturePython)
  Group = -> [Geant4]
FEATURE [Part::FeaturePython] GDMLBox_WorldBox  # WARN: FeaturePython — macro-defined, semantics opaque (R4)
  lunit = 2
  material = 5
  x = 273
  y = 273
  z = 130
FEATURE [Part::FeaturePython] GDMLBox_Box  # WARN: FeaturePython — macro-defined, semantics opaque (R4)
  Placement = pos=(20,0,0) rot=(0,0,1;0rad)
  lunit = 2
  material = 0
  x = 10
  y = 10
  z = 10
FEATURE [App::Part] LV_Box
  Group = -> [GDMLBox_Box]
  Origin = -> Origin002
FEATURE [Part::FeaturePython] Array  # Draft array (typed FeaturePython)
  AlwaysSyncPlacement = false
  Angle = 180
  ArrayType = 1
  Axis = (0,0,1)
  Base = -> LV_Box
  Center = (0,0,0)
  Count = 5
  ExpandArray = false
  Fuse = false
  IntervalAxis = (0,0,0)
  IntervalX = (100,0,0)
  IntervalY = (0,100,0)
  IntervalZ = (0,0,100)
  NumberCircles = 3
  NumberPolar = 5
  NumberX = 2
  NumberY = 2
  NumberZ = 1
  PlacementList = 5 placements: [(0,0,0),(0,0,0),(0,0,0),(0,0,0),(0,0,0)]
  RadialDistance = 50
  ScaleList = (5) [(1,1,1),(1,1,1),(1,1,1),(1,1,1),(1,1,1)]
  Symmetry = 1
  TangentialDistance = 25
FEATURE [App::Part] Part  label="experiment"
  Group = -> [LV_Box,Array]
  Origin = -> Origin001
FEATURE [App::Part] worldVOL
  Group = -> [GDMLBox_WorldBox,Part]
  Origin = -> Origin
